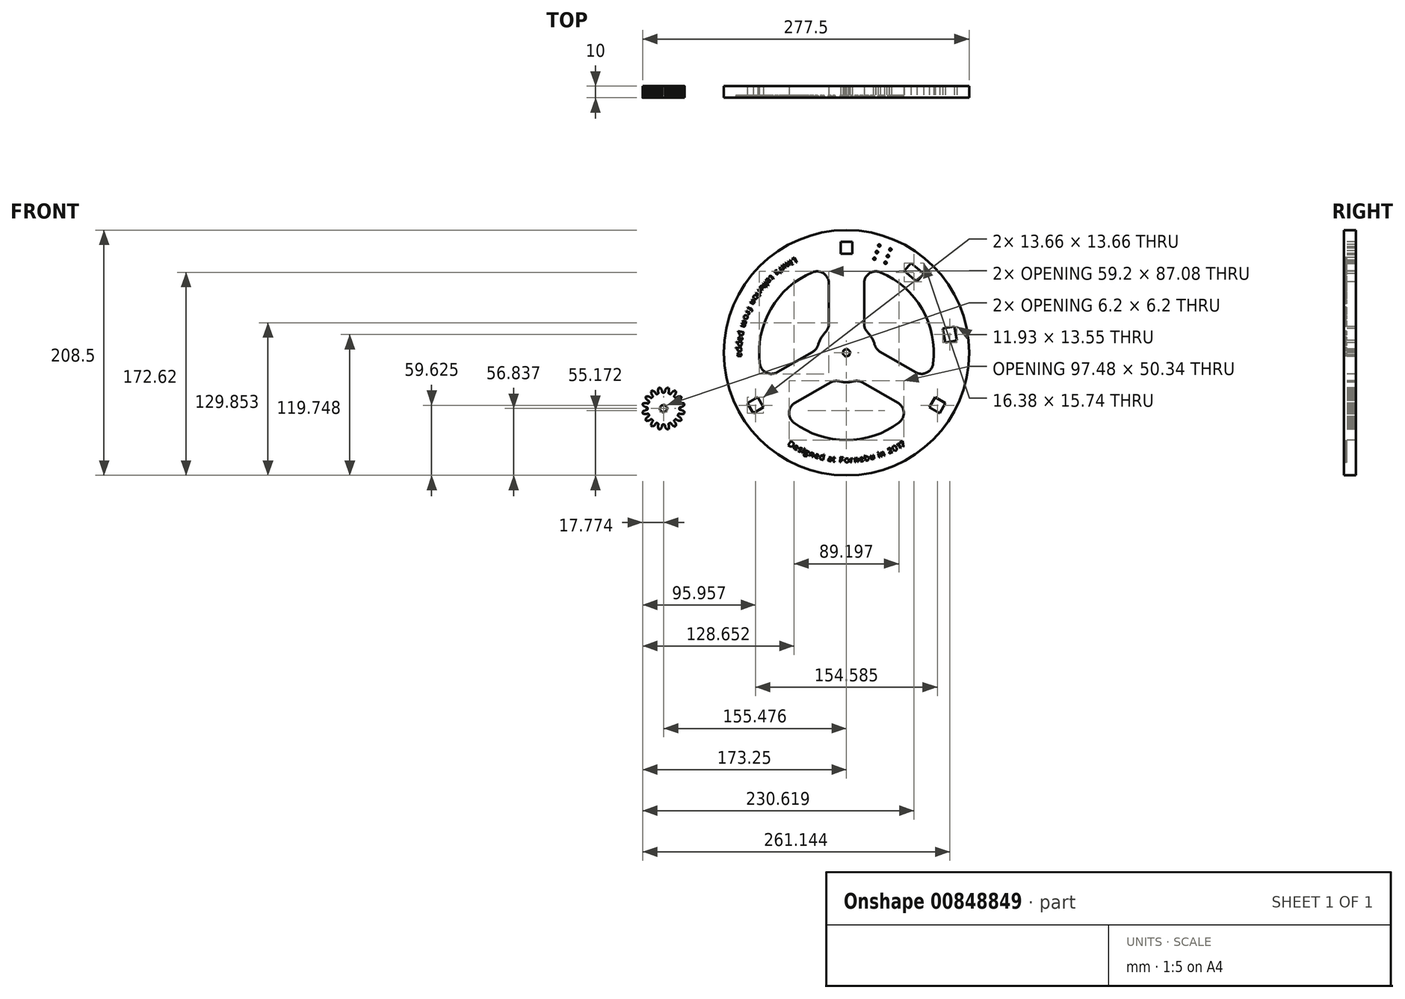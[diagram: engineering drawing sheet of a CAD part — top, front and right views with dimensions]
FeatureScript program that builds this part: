
annotation { "Feature Type Name" : "Feature", "Feature Type Description" : "" }
export const myFeature = defineFeature(function(context is Context, id is Id, definition is map)
    precondition{}
    {
        {
            var Q0;
            Q0=qCreatedBy(makeId("Front.planeOp"),FACE);
            var sketch = newSketch(context, id + "F0", { "sketchPlane" : qUnion([Q0])});
            skArc(sketch, "E0", {"start": v(15, 24.5) * mm, "mid": v(15.74, 20.72) * mm, "end": v(17.86, 17.5) * mm});
            skArc(sketch, "E1", {"start": v(24.08, 6.72) * mm, "mid": v(25.81, 3.28) * mm, "end": v(28.71, 0.74) * mm});
            skArc(sketch, "E2", {"start": v(28.9, 68.4) * mm, "mid": v(19.47, 67.52) * mm, "end": v(15, 59.19) * mm});
            skArc(sketch, "E3", {"start": v(58.76, -16.6) * mm, "mid": v(68.21, -16.9) * mm, "end": v(73.68, -9.18) * mm});
            skArc(sketch, "E4", {"start": v(-43.76, -42.58) * mm, "mid": v(-48.74, -50.62) * mm, "end": v(-44.79, -59.22) * mm});
            skArc(sketch, "E5", {"start": v(44.79, -59.22) * mm, "mid": v(48.74, -50.62) * mm, "end": v(43.76, -42.58) * mm});
            skArc(sketch, "E6", {"start": v(-6.22, -24.21) * mm, "mid": v(-10.07, -24) * mm, "end": v(-13.71, -25.24) * mm});
            skArc(sketch, "E7", {"start": v(-15, 59.19) * mm, "mid": v(-19.47, 67.52) * mm, "end": v(-28.9, 68.4) * mm});
            skArc(sketch, "E8", {"start": v(-17.86, 17.5) * mm, "mid": v(-15.74, 20.72) * mm, "end": v(-15, 24.5) * mm});
            skArc(sketch, "E9", {"start": v(-28.71, 0.74) * mm, "mid": v(-25.81, 3.28) * mm, "end": v(-24.08, 6.72) * mm});
            skArc(sketch, "E10", {"start": v(-73.68, -9.18) * mm, "mid": v(-68.21, -16.9) * mm, "end": v(-58.76, -16.6) * mm});
            skArc(sketch, "E11", {"start": v(-44.79, -59.22) * mm, "mid": v(0, -74.25) * mm, "end": v(44.79, -59.22) * mm});
            skArc(sketch, "E12", {"start": v(73.68, -9.18) * mm, "mid": v(64.3, 37.12) * mm, "end": v(28.9, 68.4) * mm});
            skArc(sketch, "E13", {"start": v(-3.1, 0) * mm, "mid": v(-3, -0.8) * mm, "end": v(-2.68, -1.55) * mm});
            skArc(sketch, "E14", {"start": v(-1.55, -2.68) * mm, "mid": v(-0.8, -3) * mm, "end": v(0, -3.1) * mm});
            skArc(sketch, "E15", {"start": v(1.55, -2.68) * mm, "mid": v(2.2, -2.2) * mm, "end": v(2.68, -1.55) * mm});
            skArc(sketch, "E16", {"start": v(3.1, 0) * mm, "mid": v(3, 0.8) * mm, "end": v(2.68, 1.55) * mm});
            skArc(sketch, "E17", {"start": v(2.51, 1.45) * mm, "mid": v(2.05, 2.05) * mm, "end": v(1.45, 2.51) * mm});
            skArc(sketch, "E18", {"start": v(0, -2.9) * mm, "mid": v(0.75, -2.8) * mm, "end": v(1.45, -2.51) * mm});
            skArc(sketch, "E19", {"start": v(1.55, 2.68) * mm, "mid": v(0.8, 3) * mm, "end": v(0, 3.1) * mm});
            skArc(sketch, "E20", {"start": v(-2.51, 1.45) * mm, "mid": v(-2.8, 0.75) * mm, "end": v(-2.9, 0) * mm});
            skArc(sketch, "E21", {"start": v(-2.51, -1.45) * mm, "mid": v(-2.05, -2.05) * mm, "end": v(-1.45, -2.51) * mm});
            skArc(sketch, "E22", {"start": v(2.51, -1.45) * mm, "mid": v(2.8, -0.75) * mm, "end": v(2.9, 0) * mm});
            skLineSegment(sketch, "E23", {"start": v(1.45, 2.51) * mm, "end": v(1.55, 2.68) * mm});
            skLineSegment(sketch, "E24", {"start": v(2.51, 1.45) * mm, "end": v(2.68, 1.55) * mm});
            skLineSegment(sketch, "E25", {"start": v(2.9, 0) * mm, "end": v(3.1, 0) * mm});
            skLineSegment(sketch, "E26", {"start": v(1.45, -2.51) * mm, "end": v(1.55, -2.68) * mm});
            skLineSegment(sketch, "E27", {"start": v(13.71, -25.24) * mm, "end": v(43.76, -42.58) * mm});
            skLineSegment(sketch, "E28", {"start": v(-13.71, -25.24) * mm, "end": v(-43.76, -42.58) * mm});
            skLineSegment(sketch, "E29", {"start": v(-28.71, 0.74) * mm, "end": v(-58.76, -16.6) * mm});
            skCircle(sketch, "E30", {"center": v(27.88, 91.22) * mm, "radius": 1 * mm});
            skLineSegment(sketch, "E31", {"start": v(70.46, -46.46) * mm, "end": v(75.46, -37.8) * mm});
            skLineSegment(sketch, "E32", {"start": v(70.46, -46.46) * mm, "end": v(79.12, -51.46) * mm});
            skLineSegment(sketch, "E33", {"start": v(75.46, -37.8) * mm, "end": v(84.12, -42.8) * mm});
            skCircle(sketch, "E34", {"center": v(37.28, 87.8) * mm, "radius": 1 * mm});
            skLineSegment(sketch, "E35", {"start": v(79.12, -51.46) * mm, "end": v(84.12, -42.8) * mm});
            skLineSegment(sketch, "E36", {"start": v(-70.46, -46.46) * mm, "end": v(-79.12, -51.46) * mm});
            skLineSegment(sketch, "E37", {"start": v(2.51, -1.45) * mm, "end": v(2.68, -1.55) * mm});
            skCircle(sketch, "E38", {"center": v(35.22, 82.16) * mm, "radius": 1 * mm});
            skLineSegment(sketch, "E39", {"start": v(-75.46, -37.8) * mm, "end": v(-84.12, -42.8) * mm});
            skLineSegment(sketch, "E40", {"start": v(-84.12, -42.8) * mm, "end": v(-79.12, -51.46) * mm});
            skLineSegment(sketch, "E41", {"start": v(-5, 84.25) * mm, "end": v(-5, 94.25) * mm});
            skArc(sketch, "E42", {"start": v(13.71, -25.24) * mm, "mid": v(10.07, -24) * mm, "end": v(6.22, -24.21) * mm});
            skCircle(sketch, "E43", {"center": v(33.17, 76.52) * mm, "radius": 1 * mm});
            skArc(sketch, "E44", {"start": v(-1.55, 2.68) * mm, "mid": v(-2.2, 2.2) * mm, "end": v(-2.68, 1.55) * mm});
            skCircle(sketch, "E45", {"center": v(0, 0) * mm, "radius": 104.25 * mm});
            skLineSegment(sketch, "E46", {"start": v(28.71, 0.74) * mm, "end": v(58.76, -16.6) * mm});
            skArc(sketch, "E47", {"start": v(-17.86, 17.5) * mm, "mid": v(-21.65, 12.5) * mm, "end": v(-24.08, 6.72) * mm});
            skArc(sketch, "E48", {"start": v(-28.9, 68.4) * mm, "mid": v(-64.3, 37.12) * mm, "end": v(-73.68, -9.18) * mm});
            skArc(sketch, "E49", {"start": v(0, 2.9) * mm, "mid": v(-0.75, 2.8) * mm, "end": v(-1.45, 2.51) * mm});
            skLineSegment(sketch, "E50", {"start": v(-75.46, -37.8) * mm, "end": v(-70.46, -46.46) * mm});
            skCircle(sketch, "E51", {"center": v(23.77, 79.94) * mm, "radius": 1 * mm});
            skLineSegment(sketch, "E52", {"start": v(15, 24.5) * mm, "end": v(15, 59.19) * mm});
            skLineSegment(sketch, "E53", {"start": v(-15, 24.5) * mm, "end": v(-15, 59.19) * mm});
            skLineSegment(sketch, "E54", {"start": v(5, 84.25) * mm, "end": v(-5, 84.25) * mm});
            skCircle(sketch, "E55", {"center": v(25.83, 85.58) * mm, "radius": 1 * mm});
            skLineSegment(sketch, "E56", {"start": v(5, 94.25) * mm, "end": v(-5, 94.25) * mm});
            skLineSegment(sketch, "E57", {"start": v(5, 84.25) * mm, "end": v(5, 94.25) * mm});
            skLineSegment(sketch, "E58", {"start": v(59.9, 60.5) * mm, "end": v(49.18, 69.5) * mm});
            skLineSegment(sketch, "E59", {"start": v(49.18, 69.5) * mm, "end": v(54.83, 76.24) * mm});
            skLineSegment(sketch, "E60", {"start": v(54.83, 76.24) * mm, "end": v(65.56, 67.24) * mm});
            skLineSegment(sketch, "E61", {"start": v(65.56, 67.24) * mm, "end": v(59.9, 60.5) * mm});
            skLineSegment(sketch, "E62", {"start": v(81.93, 20.54) * mm, "end": v(84.01, 8.72) * mm});
            skLineSegment(sketch, "E63", {"start": v(84.01, 8.72) * mm, "end": v(93.86, 10.46) * mm});
            skLineSegment(sketch, "E64", {"start": v(93.86, 10.46) * mm, "end": v(91.78, 22.28) * mm});
            skLineSegment(sketch, "E65", {"start": v(91.78, 22.28) * mm, "end": v(81.93, 20.54) * mm});
            skArc(sketch, "E66", {"start": v(-6.22, -24.21) * mm, "mid": v(0, -25) * mm, "end": v(6.22, -24.21) * mm});
            skArc(sketch, "E67", {"start": v(24.08, 6.72) * mm, "mid": v(21.65, 12.5) * mm, "end": v(17.86, 17.5) * mm});
            skLineSegment(sketch, "E68", {"start": v(0, 2.9) * mm, "end": v(0, 3.1) * mm});
            skLineSegment(sketch, "E69", {"start": v(-1.45, 2.51) * mm, "end": v(-1.55, 2.68) * mm});
            skLineSegment(sketch, "E70", {"start": v(-2.51, 1.45) * mm, "end": v(-2.68, 1.55) * mm});
            skLineSegment(sketch, "E71", {"start": v(-2.9, 0) * mm, "end": v(-3.1, 0) * mm});
            skLineSegment(sketch, "E72", {"start": v(-2.51, -1.45) * mm, "end": v(-2.68, -1.55) * mm});
            skLineSegment(sketch, "E73", {"start": v(-1.45, -2.51) * mm, "end": v(-1.55, -2.68) * mm});
            skLineSegment(sketch, "E74", {"start": v(0, -2.9) * mm, "end": v(0, -3.1) * mm});
            skLineSegment(sketch, "E75", {"start": v(-165.23, -35.88) * mm, "end": v(-165.3, -35.76) * mm});
            skLineSegment(sketch, "E76", {"start": v(-165.08, -36.06) * mm, "end": v(-165.23, -35.88) * mm});
            skLineSegment(sketch, "E77", {"start": v(-164.7, -36.5) * mm, "end": v(-165.08, -36.06) * mm});
            skArc(sketch, "E78", {"start": v(-164.92, -32.09) * mm, "mid": v(-165.48, -32.45) * mm, "end": v(-166.02, -32.83) * mm});
            skLineSegment(sketch, "E79", {"start": v(-164.03, -32.56) * mm, "end": v(-164.92, -32.09) * mm});
            skLineSegment(sketch, "E80", {"start": v(-163.29, -33.08) * mm, "end": v(-164.03, -32.56) * mm});
            skLineSegment(sketch, "E81", {"start": v(-163.08, -33.24) * mm, "end": v(-163.29, -33.08) * mm});
            skLineSegment(sketch, "E82", {"start": v(-162.9, -33.41) * mm, "end": v(-163.08, -33.24) * mm});
            skLineSegment(sketch, "E83", {"start": v(-162.74, -33.57) * mm, "end": v(-162.9, -33.41) * mm});
            skLineSegment(sketch, "E84", {"start": v(-162.6, -33.73) * mm, "end": v(-162.74, -33.57) * mm});
            skLineSegment(sketch, "E85", {"start": v(-162.48, -33.87) * mm, "end": v(-162.6, -33.73) * mm});
            skLineSegment(sketch, "E86", {"start": v(-162.4, -34) * mm, "end": v(-162.48, -33.87) * mm});
            skLineSegment(sketch, "E87", {"start": v(-162.29, -34.2) * mm, "end": v(-162.4, -34) * mm});
            skLineSegment(sketch, "E88", {"start": v(-162.02, -34.7) * mm, "end": v(-162.29, -34.2) * mm});
            skArc(sketch, "E89", {"start": v(-162.02, -34.7) * mm, "mid": v(-161.57, -35.1) * mm, "end": v(-160.97, -35.08) * mm});
            skArc(sketch, "E90", {"start": v(-160.31, -34.8) * mm, "mid": v(-160.64, -34.94) * mm, "end": v(-160.97, -35.08) * mm});
            skArc(sketch, "E91", {"start": v(-160.31, -34.8) * mm, "mid": v(-159.87, -34.4) * mm, "end": v(-159.83, -33.8) * mm});
            skLineSegment(sketch, "E92", {"start": v(-159.93, -30.86) * mm, "end": v(-159.64, -29.9) * mm});
            skLineSegment(sketch, "E93", {"start": v(-160.1, -31.75) * mm, "end": v(-159.93, -30.86) * mm});
            skLineSegment(sketch, "E94", {"start": v(-160.11, -32.01) * mm, "end": v(-160.1, -31.75) * mm});
            skLineSegment(sketch, "E95", {"start": v(-160.13, -32.26) * mm, "end": v(-160.11, -32.01) * mm});
            skLineSegment(sketch, "E96", {"start": v(-160.13, -32.5) * mm, "end": v(-160.13, -32.26) * mm});
            skLineSegment(sketch, "E97", {"start": v(-160.12, -32.7) * mm, "end": v(-160.13, -32.5) * mm});
            skLineSegment(sketch, "E98", {"start": v(-160.1, -32.88) * mm, "end": v(-160.12, -32.7) * mm});
            skLineSegment(sketch, "E99", {"start": v(-160.07, -33.03) * mm, "end": v(-160.1, -32.88) * mm});
            skLineSegment(sketch, "E100", {"start": v(-160, -33.25) * mm, "end": v(-160.07, -33.03) * mm});
            skLineSegment(sketch, "E101", {"start": v(-159.83, -33.8) * mm, "end": v(-160, -33.25) * mm});
            skArc(sketch, "E102", {"start": v(-158.33, -29.64) * mm, "mid": v(-158.99, -29.76) * mm, "end": v(-159.64, -29.9) * mm});
            skLineSegment(sketch, "E103", {"start": v(-157.7, -30.42) * mm, "end": v(-158.33, -29.64) * mm});
            skLineSegment(sketch, "E104", {"start": v(-157.2, -31.18) * mm, "end": v(-157.7, -30.42) * mm});
            skLineSegment(sketch, "E105", {"start": v(-157.08, -31.41) * mm, "end": v(-157.2, -31.18) * mm});
            skLineSegment(sketch, "E106", {"start": v(-156.98, -31.63) * mm, "end": v(-157.08, -31.41) * mm});
            skLineSegment(sketch, "E107", {"start": v(-156.89, -31.85) * mm, "end": v(-156.98, -31.63) * mm});
            skLineSegment(sketch, "E108", {"start": v(-156.82, -32.04) * mm, "end": v(-156.89, -31.85) * mm});
            skLineSegment(sketch, "E109", {"start": v(-156.77, -32.22) * mm, "end": v(-156.82, -32.04) * mm});
            skLineSegment(sketch, "E110", {"start": v(-156.74, -32.36) * mm, "end": v(-156.77, -32.22) * mm});
            skLineSegment(sketch, "E111", {"start": v(-156.71, -32.6) * mm, "end": v(-156.74, -32.36) * mm});
            skLineSegment(sketch, "E112", {"start": v(-156.66, -33.17) * mm, "end": v(-156.71, -32.6) * mm});
            skArc(sketch, "E113", {"start": v(-156.66, -33.17) * mm, "mid": v(-156.4, -33.7) * mm, "end": v(-155.83, -33.92) * mm});
            skArc(sketch, "E114", {"start": v(-155.12, -33.92) * mm, "mid": v(-155.48, -33.91) * mm, "end": v(-155.83, -33.92) * mm});
            skArc(sketch, "E115", {"start": v(-155.12, -33.92) * mm, "mid": v(-154.56, -33.7) * mm, "end": v(-154.29, -33.17) * mm});
            skLineSegment(sketch, "E116", {"start": v(-153.26, -30.42) * mm, "end": v(-152.62, -29.64) * mm});
            skLineSegment(sketch, "E117", {"start": v(-153.75, -31.18) * mm, "end": v(-153.26, -30.42) * mm});
            skLineSegment(sketch, "E118", {"start": v(-153.87, -31.41) * mm, "end": v(-153.75, -31.18) * mm});
            skLineSegment(sketch, "E119", {"start": v(-153.97, -31.63) * mm, "end": v(-153.87, -31.41) * mm});
            skLineSegment(sketch, "E120", {"start": v(-154.06, -31.85) * mm, "end": v(-153.97, -31.63) * mm});
            skLineSegment(sketch, "E121", {"start": v(-154.13, -32.04) * mm, "end": v(-154.06, -31.85) * mm});
            skLineSegment(sketch, "E122", {"start": v(-154.18, -32.22) * mm, "end": v(-154.13, -32.04) * mm});
            skLineSegment(sketch, "E123", {"start": v(-154.22, -32.36) * mm, "end": v(-154.18, -32.22) * mm});
            skLineSegment(sketch, "E124", {"start": v(-154.24, -32.6) * mm, "end": v(-154.22, -32.36) * mm});
            skLineSegment(sketch, "E125", {"start": v(-154.29, -33.17) * mm, "end": v(-154.24, -32.6) * mm});
            skArc(sketch, "E126", {"start": v(-151.31, -29.9) * mm, "mid": v(-151.96, -29.76) * mm, "end": v(-152.62, -29.64) * mm});
            skLineSegment(sketch, "E127", {"start": v(-151.02, -30.86) * mm, "end": v(-151.31, -29.9) * mm});
            skLineSegment(sketch, "E128", {"start": v(-150.86, -31.75) * mm, "end": v(-151.02, -30.86) * mm});
            skLineSegment(sketch, "E129", {"start": v(-150.84, -32.01) * mm, "end": v(-150.86, -31.75) * mm});
            skLineSegment(sketch, "E130", {"start": v(-150.82, -32.26) * mm, "end": v(-150.84, -32.01) * mm});
            skLineSegment(sketch, "E131", {"start": v(-150.82, -32.5) * mm, "end": v(-150.82, -32.26) * mm});
            skLineSegment(sketch, "E132", {"start": v(-150.84, -32.7) * mm, "end": v(-150.82, -32.5) * mm});
            skLineSegment(sketch, "E133", {"start": v(-150.86, -32.88) * mm, "end": v(-150.84, -32.7) * mm});
            skLineSegment(sketch, "E134", {"start": v(-150.88, -33.03) * mm, "end": v(-150.86, -32.88) * mm});
            skLineSegment(sketch, "E135", {"start": v(-138.93, -51.87) * mm, "end": v(-137.96, -51.57) * mm});
            skArc(sketch, "E136", {"start": v(-137.96, -51.57) * mm, "mid": v(-137.82, -50.92) * mm, "end": v(-137.7, -50.27) * mm});
            skLineSegment(sketch, "E137", {"start": v(-141.23, -48.6) * mm, "end": v(-140.65, -48.65) * mm});
            skLineSegment(sketch, "E138", {"start": v(-140.65, -48.65) * mm, "end": v(-140.43, -48.67) * mm});
            skLineSegment(sketch, "E139", {"start": v(-140.43, -48.67) * mm, "end": v(-140.28, -48.7) * mm});
            skLineSegment(sketch, "E140", {"start": v(-140.28, -48.7) * mm, "end": v(-140.1, -48.76) * mm});
            skLineSegment(sketch, "E141", {"start": v(-140.1, -48.76) * mm, "end": v(-139.9, -48.83) * mm});
            skLineSegment(sketch, "E142", {"start": v(-139.9, -48.83) * mm, "end": v(-139.7, -48.91) * mm});
            skLineSegment(sketch, "E143", {"start": v(-139.7, -48.91) * mm, "end": v(-139.47, -49.02) * mm});
            skLineSegment(sketch, "E144", {"start": v(-139.47, -49.02) * mm, "end": v(-139.24, -49.14) * mm});
            skLineSegment(sketch, "E145", {"start": v(-139.24, -49.14) * mm, "end": v(-138.48, -49.63) * mm});
            skLineSegment(sketch, "E146", {"start": v(-138.48, -49.63) * mm, "end": v(-137.7, -50.27) * mm});
            skArc(sketch, "E147", {"start": v(-141.98, -47.77) * mm, "mid": v(-141.77, -48.33) * mm, "end": v(-141.23, -48.6) * mm});
            skArc(sketch, "E148", {"start": v(-141.98, -47.77) * mm, "mid": v(-141.98, -47.41) * mm, "end": v(-141.98, -47.06) * mm});
            skArc(sketch, "E149", {"start": v(-141.23, -46.23) * mm, "mid": v(-141.77, -46.5) * mm, "end": v(-141.98, -47.06) * mm});
            skLineSegment(sketch, "E150", {"start": v(-141.23, -46.23) * mm, "end": v(-140.65, -46.18) * mm});
            skLineSegment(sketch, "E151", {"start": v(-140.65, -46.18) * mm, "end": v(-140.43, -46.15) * mm});
            skLineSegment(sketch, "E152", {"start": v(-140.43, -46.15) * mm, "end": v(-140.28, -46.12) * mm});
            skLineSegment(sketch, "E153", {"start": v(-140.28, -46.12) * mm, "end": v(-140.1, -46.07) * mm});
            skLineSegment(sketch, "E154", {"start": v(-140.1, -46.07) * mm, "end": v(-139.9, -46) * mm});
            skLineSegment(sketch, "E155", {"start": v(-139.9, -46) * mm, "end": v(-139.7, -45.91) * mm});
            skLineSegment(sketch, "E156", {"start": v(-139.7, -45.91) * mm, "end": v(-139.47, -45.8) * mm});
            skLineSegment(sketch, "E157", {"start": v(-139.47, -45.8) * mm, "end": v(-139.24, -45.68) * mm});
            skLineSegment(sketch, "E158", {"start": v(-139.24, -45.68) * mm, "end": v(-138.48, -45.2) * mm});
            skLineSegment(sketch, "E159", {"start": v(-138.48, -45.2) * mm, "end": v(-137.7, -44.56) * mm});
            skArc(sketch, "E160", {"start": v(-137.7, -44.56) * mm, "mid": v(-137.82, -43.9) * mm, "end": v(-137.96, -43.25) * mm});
            skLineSegment(sketch, "E161", {"start": v(-141.86, -43.06) * mm, "end": v(-141.3, -42.88) * mm});
            skLineSegment(sketch, "E162", {"start": v(-141.3, -42.88) * mm, "end": v(-141.1, -42.82) * mm});
            skLineSegment(sketch, "E163", {"start": v(-141.1, -42.82) * mm, "end": v(-140.94, -42.8) * mm});
            skLineSegment(sketch, "E164", {"start": v(-140.94, -42.8) * mm, "end": v(-140.76, -42.77) * mm});
            skLineSegment(sketch, "E165", {"start": v(-140.76, -42.77) * mm, "end": v(-140.55, -42.76) * mm});
            skLineSegment(sketch, "E166", {"start": v(-140.55, -42.76) * mm, "end": v(-140.32, -42.76) * mm});
            skLineSegment(sketch, "E167", {"start": v(-140.32, -42.76) * mm, "end": v(-140.08, -42.77) * mm});
            skLineSegment(sketch, "E168", {"start": v(-140.08, -42.77) * mm, "end": v(-139.82, -42.8) * mm});
            skLineSegment(sketch, "E169", {"start": v(-139.82, -42.8) * mm, "end": v(-138.93, -42.96) * mm});
            skLineSegment(sketch, "E170", {"start": v(-138.93, -42.96) * mm, "end": v(-137.96, -43.25) * mm});
            skArc(sketch, "E171", {"start": v(-142.87, -42.58) * mm, "mid": v(-142.46, -43.02) * mm, "end": v(-141.86, -43.06) * mm});
            skArc(sketch, "E172", {"start": v(-142.87, -42.58) * mm, "mid": v(-143, -42.25) * mm, "end": v(-143.14, -41.92) * mm});
            skArc(sketch, "E173", {"start": v(-142.77, -40.87) * mm, "mid": v(-143.17, -41.32) * mm, "end": v(-143.14, -41.92) * mm});
            skLineSegment(sketch, "E174", {"start": v(-142.77, -40.87) * mm, "end": v(-142.25, -40.6) * mm});
            skLineSegment(sketch, "E175", {"start": v(-142.25, -40.6) * mm, "end": v(-142.05, -40.5) * mm});
            skLineSegment(sketch, "E176", {"start": v(-142.05, -40.5) * mm, "end": v(-141.93, -40.4) * mm});
            skLineSegment(sketch, "E177", {"start": v(-141.93, -40.4) * mm, "end": v(-141.8, -40.3) * mm});
            skLineSegment(sketch, "E178", {"start": v(-141.8, -40.3) * mm, "end": v(-141.64, -40.15) * mm});
            skLineSegment(sketch, "E179", {"start": v(-141.64, -40.15) * mm, "end": v(-141.47, -39.99) * mm});
            skLineSegment(sketch, "E180", {"start": v(-141.47, -39.99) * mm, "end": v(-141.3, -39.8) * mm});
            skLineSegment(sketch, "E181", {"start": v(-141.3, -39.8) * mm, "end": v(-141.14, -39.6) * mm});
            skLineSegment(sketch, "E182", {"start": v(-141.14, -39.6) * mm, "end": v(-140.62, -38.86) * mm});
            skLineSegment(sketch, "E183", {"start": v(-140.62, -38.86) * mm, "end": v(-140.15, -37.97) * mm});
            skArc(sketch, "E184", {"start": v(-140.15, -37.97) * mm, "mid": v(-140.5, -37.41) * mm, "end": v(-140.89, -36.87) * mm});
            skLineSegment(sketch, "E185", {"start": v(-144.57, -38.18) * mm, "end": v(-144.12, -37.8) * mm});
            skLineSegment(sketch, "E186", {"start": v(-144.12, -37.8) * mm, "end": v(-143.94, -37.66) * mm});
            skLineSegment(sketch, "E187", {"start": v(-143.94, -37.66) * mm, "end": v(-143.82, -37.58) * mm});
            skLineSegment(sketch, "E188", {"start": v(-143.82, -37.58) * mm, "end": v(-143.66, -37.5) * mm});
            skLineSegment(sketch, "E189", {"start": v(-143.66, -37.5) * mm, "end": v(-143.47, -37.4) * mm});
            skLineSegment(sketch, "E190", {"start": v(-143.47, -37.4) * mm, "end": v(-143.26, -37.32) * mm});
            skLineSegment(sketch, "E191", {"start": v(-143.26, -37.32) * mm, "end": v(-143.02, -37.23) * mm});
            skLineSegment(sketch, "E192", {"start": v(-143.02, -37.23) * mm, "end": v(-142.77, -37.16) * mm});
            skLineSegment(sketch, "E193", {"start": v(-142.77, -37.16) * mm, "end": v(-141.9, -36.96) * mm});
            skLineSegment(sketch, "E194", {"start": v(-141.9, -36.96) * mm, "end": v(-140.89, -36.87) * mm});
            skArc(sketch, "E195", {"start": v(-145.68, -38.12) * mm, "mid": v(-145.14, -38.37) * mm, "end": v(-144.57, -38.18) * mm});
            skArc(sketch, "E196", {"start": v(-145.68, -38.12) * mm, "mid": v(-145.93, -37.87) * mm, "end": v(-146.18, -37.62) * mm});
            skArc(sketch, "E197", {"start": v(-146.24, -36.5) * mm, "mid": v(-146.44, -37.07) * mm, "end": v(-146.18, -37.62) * mm});
            skLineSegment(sketch, "E198", {"start": v(-146.24, -36.5) * mm, "end": v(-145.87, -36.06) * mm});
            skLineSegment(sketch, "E199", {"start": v(-145.87, -36.06) * mm, "end": v(-145.73, -35.88) * mm});
            skLineSegment(sketch, "E200", {"start": v(-145.73, -35.88) * mm, "end": v(-145.65, -35.76) * mm});
            skLineSegment(sketch, "E201", {"start": v(-145.65, -35.76) * mm, "end": v(-145.56, -35.6) * mm});
            skLineSegment(sketch, "E202", {"start": v(-145.56, -35.6) * mm, "end": v(-145.47, -35.4) * mm});
            skLineSegment(sketch, "E203", {"start": v(-145.47, -35.4) * mm, "end": v(-145.38, -35.2) * mm});
            skLineSegment(sketch, "E204", {"start": v(-145.38, -35.2) * mm, "end": v(-145.3, -34.96) * mm});
            skLineSegment(sketch, "E205", {"start": v(-145.3, -34.96) * mm, "end": v(-145.22, -34.71) * mm});
            skLineSegment(sketch, "E206", {"start": v(-145.22, -34.71) * mm, "end": v(-145.03, -33.83) * mm});
            skLineSegment(sketch, "E207", {"start": v(-145.03, -33.83) * mm, "end": v(-144.93, -32.83) * mm});
            skArc(sketch, "E208", {"start": v(-144.93, -32.83) * mm, "mid": v(-145.48, -32.45) * mm, "end": v(-146.04, -32.09) * mm});
            skLineSegment(sketch, "E209", {"start": v(-148.93, -34.7) * mm, "end": v(-148.66, -34.2) * mm});
            skLineSegment(sketch, "E210", {"start": v(-148.66, -34.2) * mm, "end": v(-148.55, -34) * mm});
            skLineSegment(sketch, "E211", {"start": v(-148.55, -34) * mm, "end": v(-148.47, -33.87) * mm});
            skLineSegment(sketch, "E212", {"start": v(-148.47, -33.87) * mm, "end": v(-148.35, -33.73) * mm});
            skLineSegment(sketch, "E213", {"start": v(-148.35, -33.73) * mm, "end": v(-148.21, -33.57) * mm});
            skLineSegment(sketch, "E214", {"start": v(-148.21, -33.57) * mm, "end": v(-148.05, -33.41) * mm});
            skLineSegment(sketch, "E215", {"start": v(-148.05, -33.41) * mm, "end": v(-147.87, -33.24) * mm});
            skLineSegment(sketch, "E216", {"start": v(-147.87, -33.24) * mm, "end": v(-147.67, -33.08) * mm});
            skLineSegment(sketch, "E217", {"start": v(-147.67, -33.08) * mm, "end": v(-146.92, -32.56) * mm});
            skLineSegment(sketch, "E218", {"start": v(-146.92, -32.56) * mm, "end": v(-146.04, -32.09) * mm});
            skArc(sketch, "E219", {"start": v(-149.98, -35.08) * mm, "mid": v(-149.38, -35.1) * mm, "end": v(-148.93, -34.7) * mm});
            skArc(sketch, "E220", {"start": v(-149.98, -35.08) * mm, "mid": v(-150.3, -34.94) * mm, "end": v(-150.64, -34.8) * mm});
            skArc(sketch, "E221", {"start": v(-151.12, -33.8) * mm, "mid": v(-151.08, -34.4) * mm, "end": v(-150.64, -34.8) * mm});
            skLineSegment(sketch, "E222", {"start": v(-151.12, -33.8) * mm, "end": v(-150.94, -33.25) * mm});
            skLineSegment(sketch, "E223", {"start": v(-150.94, -33.25) * mm, "end": v(-150.88, -33.03) * mm});
            skLineSegment(sketch, "E224", {"start": v(-165.57, -35.2) * mm, "end": v(-165.65, -34.96) * mm});
            skLineSegment(sketch, "E225", {"start": v(-165.65, -34.96) * mm, "end": v(-165.73, -34.71) * mm});
            skLineSegment(sketch, "E226", {"start": v(-165.73, -34.71) * mm, "end": v(-165.92, -33.83) * mm});
            skLineSegment(sketch, "E227", {"start": v(-165.92, -33.83) * mm, "end": v(-166.02, -32.83) * mm});
            skArc(sketch, "E228", {"start": v(-164.77, -37.62) * mm, "mid": v(-164.52, -37.07) * mm, "end": v(-164.7, -36.5) * mm});
            skArc(sketch, "E229", {"start": v(-164.77, -37.62) * mm, "mid": v(-165.02, -37.87) * mm, "end": v(-165.27, -38.12) * mm});
            skArc(sketch, "E230", {"start": v(-166.39, -38.18) * mm, "mid": v(-165.82, -38.37) * mm, "end": v(-165.27, -38.12) * mm});
            skLineSegment(sketch, "E231", {"start": v(-166.39, -38.18) * mm, "end": v(-166.83, -37.8) * mm});
            skLineSegment(sketch, "E232", {"start": v(-166.83, -37.8) * mm, "end": v(-167, -37.66) * mm});
            skLineSegment(sketch, "E233", {"start": v(-167, -37.66) * mm, "end": v(-167.13, -37.58) * mm});
            skLineSegment(sketch, "E234", {"start": v(-167.13, -37.58) * mm, "end": v(-167.3, -37.5) * mm});
            skLineSegment(sketch, "E235", {"start": v(-167.3, -37.5) * mm, "end": v(-167.48, -37.4) * mm});
            skLineSegment(sketch, "E236", {"start": v(-167.48, -37.4) * mm, "end": v(-167.7, -37.32) * mm});
            skLineSegment(sketch, "E237", {"start": v(-167.7, -37.32) * mm, "end": v(-167.93, -37.23) * mm});
            skLineSegment(sketch, "E238", {"start": v(-167.93, -37.23) * mm, "end": v(-168.18, -37.16) * mm});
            skLineSegment(sketch, "E239", {"start": v(-168.18, -37.16) * mm, "end": v(-169.06, -36.96) * mm});
            skLineSegment(sketch, "E240", {"start": v(-169.06, -36.96) * mm, "end": v(-170.06, -36.87) * mm});
            skArc(sketch, "E241", {"start": v(-170.06, -36.87) * mm, "mid": v(-170.44, -37.41) * mm, "end": v(-170.8, -37.97) * mm});
            skLineSegment(sketch, "E242", {"start": v(-168.18, -40.87) * mm, "end": v(-168.7, -40.6) * mm});
            skLineSegment(sketch, "E243", {"start": v(-168.7, -40.6) * mm, "end": v(-168.9, -40.5) * mm});
            skLineSegment(sketch, "E244", {"start": v(-168.9, -40.5) * mm, "end": v(-169.02, -40.4) * mm});
            skLineSegment(sketch, "E245", {"start": v(-169.02, -40.4) * mm, "end": v(-169.16, -40.3) * mm});
            skLineSegment(sketch, "E246", {"start": v(-169.16, -40.3) * mm, "end": v(-169.32, -40.15) * mm});
            skLineSegment(sketch, "E247", {"start": v(-169.32, -40.15) * mm, "end": v(-169.48, -39.99) * mm});
            skLineSegment(sketch, "E248", {"start": v(-169.48, -39.99) * mm, "end": v(-169.64, -39.8) * mm});
            skLineSegment(sketch, "E249", {"start": v(-169.64, -39.8) * mm, "end": v(-169.81, -39.6) * mm});
            skLineSegment(sketch, "E250", {"start": v(-169.81, -39.6) * mm, "end": v(-170.33, -38.86) * mm});
            skLineSegment(sketch, "E251", {"start": v(-170.33, -38.86) * mm, "end": v(-170.8, -37.97) * mm});
            skArc(sketch, "E252", {"start": v(-167.8, -41.92) * mm, "mid": v(-167.78, -41.32) * mm, "end": v(-168.18, -40.87) * mm});
            skArc(sketch, "E253", {"start": v(-167.8, -41.92) * mm, "mid": v(-167.95, -42.25) * mm, "end": v(-168.08, -42.58) * mm});
            skArc(sketch, "E254", {"start": v(-169.09, -43.06) * mm, "mid": v(-168.49, -43.02) * mm, "end": v(-168.08, -42.58) * mm});
            skLineSegment(sketch, "E255", {"start": v(-169.09, -43.06) * mm, "end": v(-169.64, -42.88) * mm});
            skLineSegment(sketch, "E256", {"start": v(-169.64, -42.88) * mm, "end": v(-169.86, -42.82) * mm});
            skLineSegment(sketch, "E257", {"start": v(-169.86, -42.82) * mm, "end": v(-170, -42.8) * mm});
            skLineSegment(sketch, "E258", {"start": v(-170, -42.8) * mm, "end": v(-170.19, -42.77) * mm});
            skLineSegment(sketch, "E259", {"start": v(-170.19, -42.77) * mm, "end": v(-170.4, -42.76) * mm});
            skLineSegment(sketch, "E260", {"start": v(-170.4, -42.76) * mm, "end": v(-170.63, -42.76) * mm});
            skLineSegment(sketch, "E261", {"start": v(-170.63, -42.76) * mm, "end": v(-170.87, -42.77) * mm});
            skLineSegment(sketch, "E262", {"start": v(-170.87, -42.77) * mm, "end": v(-171.13, -42.8) * mm});
            skArc(sketch, "E263", {"start": v(-170.8, -56.85) * mm, "mid": v(-170.44, -57.41) * mm, "end": v(-170.06, -57.96) * mm});
            skLineSegment(sketch, "E264", {"start": v(-154.24, -62.24) * mm, "end": v(-154.22, -62.46) * mm});
            skLineSegment(sketch, "E265", {"start": v(-166.39, -56.65) * mm, "end": v(-166.83, -57.02) * mm});
            skLineSegment(sketch, "E266", {"start": v(-154.22, -62.46) * mm, "end": v(-154.18, -62.6) * mm});
            skLineSegment(sketch, "E267", {"start": v(-166.83, -57.02) * mm, "end": v(-167, -57.16) * mm});
            skLineSegment(sketch, "E268", {"start": v(-154.18, -62.6) * mm, "end": v(-154.13, -62.78) * mm});
            skLineSegment(sketch, "E269", {"start": v(-167, -57.16) * mm, "end": v(-167.13, -57.24) * mm});
            skLineSegment(sketch, "E270", {"start": v(-154.13, -62.78) * mm, "end": v(-154.06, -62.98) * mm});
            skLineSegment(sketch, "E271", {"start": v(-167.13, -57.24) * mm, "end": v(-167.3, -57.33) * mm});
            skLineSegment(sketch, "E272", {"start": v(-154.06, -62.98) * mm, "end": v(-153.97, -63.2) * mm});
            skLineSegment(sketch, "E273", {"start": v(-167.3, -57.33) * mm, "end": v(-167.48, -57.42) * mm});
            skLineSegment(sketch, "E274", {"start": v(-153.97, -63.2) * mm, "end": v(-153.87, -63.41) * mm});
            skLineSegment(sketch, "E275", {"start": v(-167.48, -57.42) * mm, "end": v(-167.7, -57.5) * mm});
            skLineSegment(sketch, "E276", {"start": v(-153.87, -63.41) * mm, "end": v(-153.75, -63.65) * mm});
            skLineSegment(sketch, "E277", {"start": v(-167.7, -57.5) * mm, "end": v(-167.93, -57.6) * mm});
            skLineSegment(sketch, "E278", {"start": v(-153.75, -63.65) * mm, "end": v(-153.26, -64.4) * mm});
            skLineSegment(sketch, "E279", {"start": v(-167.93, -57.6) * mm, "end": v(-168.18, -57.67) * mm});
            skLineSegment(sketch, "E280", {"start": v(-153.26, -64.4) * mm, "end": v(-152.62, -65.19) * mm});
            skLineSegment(sketch, "E281", {"start": v(-168.18, -57.67) * mm, "end": v(-169.06, -57.86) * mm});
            skArc(sketch, "E282", {"start": v(-152.62, -65.19) * mm, "mid": v(-151.96, -65.07) * mm, "end": v(-151.31, -64.93) * mm});
            skLineSegment(sketch, "E283", {"start": v(-169.06, -57.86) * mm, "end": v(-170.06, -57.96) * mm});
            skLineSegment(sketch, "E284", {"start": v(-151.12, -61.03) * mm, "end": v(-150.94, -61.58) * mm});
            skArc(sketch, "E285", {"start": v(-165.27, -56.7) * mm, "mid": v(-165.82, -56.45) * mm, "end": v(-166.39, -56.65) * mm});
            skLineSegment(sketch, "E286", {"start": v(-150.94, -61.58) * mm, "end": v(-150.88, -61.8) * mm});
            skArc(sketch, "E287", {"start": v(-165.27, -56.7) * mm, "mid": v(-165.02, -56.96) * mm, "end": v(-164.77, -57.2) * mm});
            skLineSegment(sketch, "E288", {"start": v(-150.88, -61.8) * mm, "end": v(-150.86, -61.94) * mm});
            skLineSegment(sketch, "E289", {"start": v(-150.86, -61.94) * mm, "end": v(-150.84, -62.13) * mm});
            skLineSegment(sketch, "E290", {"start": v(-150.84, -62.13) * mm, "end": v(-150.82, -62.34) * mm});
            skLineSegment(sketch, "E291", {"start": v(-150.82, -62.34) * mm, "end": v(-150.82, -62.57) * mm});
            skLineSegment(sketch, "E292", {"start": v(-150.82, -62.57) * mm, "end": v(-150.84, -62.81) * mm});
            skLineSegment(sketch, "E293", {"start": v(-150.84, -62.81) * mm, "end": v(-150.86, -63.07) * mm});
            skLineSegment(sketch, "E294", {"start": v(-150.86, -63.07) * mm, "end": v(-151.02, -63.96) * mm});
            skLineSegment(sketch, "E295", {"start": v(-151.02, -63.96) * mm, "end": v(-151.31, -64.93) * mm});
            skArc(sketch, "E296", {"start": v(-150.64, -60.02) * mm, "mid": v(-151.08, -60.43) * mm, "end": v(-151.12, -61.03) * mm});
            skArc(sketch, "E297", {"start": v(-150.64, -60.02) * mm, "mid": v(-150.3, -59.89) * mm, "end": v(-149.98, -59.75) * mm});
            skArc(sketch, "E298", {"start": v(-148.93, -60.12) * mm, "mid": v(-149.38, -59.72) * mm, "end": v(-149.98, -59.75) * mm});
            skArc(sketch, "E299", {"start": v(-157.99, -48.86) * mm, "mid": v(-157.53, -49.46) * mm, "end": v(-156.93, -49.92) * mm});
            skLineSegment(sketch, "E300", {"start": v(-148.93, -60.12) * mm, "end": v(-148.66, -60.63) * mm});
            skArc(sketch, "E301", {"start": v(-146.04, -62.74) * mm, "mid": v(-145.48, -62.38) * mm, "end": v(-144.93, -62) * mm});
            skLineSegment(sketch, "E302", {"start": v(-146.92, -62.26) * mm, "end": v(-146.04, -62.74) * mm});
            skLineSegment(sketch, "E303", {"start": v(-147.67, -61.75) * mm, "end": v(-146.92, -62.26) * mm});
            skLineSegment(sketch, "E304", {"start": v(-147.87, -61.58) * mm, "end": v(-147.67, -61.75) * mm});
            skLineSegment(sketch, "E305", {"start": v(-148.05, -61.42) * mm, "end": v(-147.87, -61.58) * mm});
            skLineSegment(sketch, "E306", {"start": v(-148.21, -61.25) * mm, "end": v(-148.05, -61.42) * mm});
            skLineSegment(sketch, "E307", {"start": v(-148.35, -61.1) * mm, "end": v(-148.21, -61.25) * mm});
            skLineSegment(sketch, "E308", {"start": v(-148.47, -60.96) * mm, "end": v(-148.35, -61.1) * mm});
            skLineSegment(sketch, "E309", {"start": v(-148.55, -60.83) * mm, "end": v(-148.47, -60.96) * mm});
            skLineSegment(sketch, "E310", {"start": v(-148.66, -60.63) * mm, "end": v(-148.55, -60.83) * mm});
            skLineSegment(sketch, "E311", {"start": v(-170.33, -55.96) * mm, "end": v(-170.8, -56.85) * mm});
            skLineSegment(sketch, "E312", {"start": v(-154.29, -61.66) * mm, "end": v(-154.24, -62.24) * mm});
            skLineSegment(sketch, "E313", {"start": v(-169.81, -55.22) * mm, "end": v(-170.33, -55.96) * mm});
            skArc(sketch, "E314", {"start": v(-154.29, -61.66) * mm, "mid": v(-154.56, -61.12) * mm, "end": v(-155.12, -60.9) * mm});
            skLineSegment(sketch, "E315", {"start": v(-169.64, -55.02) * mm, "end": v(-169.81, -55.22) * mm});
            skArc(sketch, "E316", {"start": v(-155.83, -60.9) * mm, "mid": v(-155.48, -60.91) * mm, "end": v(-155.12, -60.9) * mm});
            skLineSegment(sketch, "E317", {"start": v(-169.48, -54.84) * mm, "end": v(-169.64, -55.02) * mm});
            skArc(sketch, "E318", {"start": v(-155.83, -60.9) * mm, "mid": v(-156.4, -61.12) * mm, "end": v(-156.66, -61.66) * mm});
            skLineSegment(sketch, "E319", {"start": v(-169.32, -54.68) * mm, "end": v(-169.48, -54.84) * mm});
            skLineSegment(sketch, "E320", {"start": v(-169.16, -54.54) * mm, "end": v(-169.32, -54.68) * mm});
            skLineSegment(sketch, "E321", {"start": v(-169.02, -54.42) * mm, "end": v(-169.16, -54.54) * mm});
            skLineSegment(sketch, "E322", {"start": v(-168.9, -54.34) * mm, "end": v(-169.02, -54.42) * mm});
            skLineSegment(sketch, "E323", {"start": v(-168.7, -54.23) * mm, "end": v(-168.9, -54.34) * mm});
            skLineSegment(sketch, "E324", {"start": v(-168.18, -53.96) * mm, "end": v(-168.7, -54.23) * mm});
            skArc(sketch, "E325", {"start": v(-168.18, -53.96) * mm, "mid": v(-167.78, -53.5) * mm, "end": v(-167.8, -52.9) * mm});
            skArc(sketch, "E326", {"start": v(-168.08, -52.25) * mm, "mid": v(-167.95, -52.58) * mm, "end": v(-167.8, -52.9) * mm});
            skArc(sketch, "E327", {"start": v(-168.08, -52.25) * mm, "mid": v(-168.49, -51.8) * mm, "end": v(-169.09, -51.77) * mm});
            skLineSegment(sketch, "E328", {"start": v(-172.02, -51.87) * mm, "end": v(-172.99, -51.57) * mm});
            skLineSegment(sketch, "E329", {"start": v(-171.13, -52.03) * mm, "end": v(-172.02, -51.87) * mm});
            skLineSegment(sketch, "E330", {"start": v(-170.87, -52.05) * mm, "end": v(-171.13, -52.03) * mm});
            skLineSegment(sketch, "E331", {"start": v(-170.63, -52.06) * mm, "end": v(-170.87, -52.05) * mm});
            skLineSegment(sketch, "E332", {"start": v(-170.4, -52.06) * mm, "end": v(-170.63, -52.06) * mm});
            skLineSegment(sketch, "E333", {"start": v(-170.19, -52.05) * mm, "end": v(-170.4, -52.06) * mm});
            skLineSegment(sketch, "E334", {"start": v(-170, -52.03) * mm, "end": v(-170.19, -52.05) * mm});
            skLineSegment(sketch, "E335", {"start": v(-169.86, -52) * mm, "end": v(-170, -52.03) * mm});
            skLineSegment(sketch, "E336", {"start": v(-169.64, -51.94) * mm, "end": v(-169.86, -52) * mm});
            skLineSegment(sketch, "E337", {"start": v(-169.09, -51.77) * mm, "end": v(-169.64, -51.94) * mm});
            skArc(sketch, "E338", {"start": v(-173.25, -50.27) * mm, "mid": v(-173.13, -50.92) * mm, "end": v(-172.99, -51.57) * mm});
            skLineSegment(sketch, "E339", {"start": v(-172.47, -49.63) * mm, "end": v(-173.25, -50.27) * mm});
            skLineSegment(sketch, "E340", {"start": v(-171.7, -49.14) * mm, "end": v(-172.47, -49.63) * mm});
            skLineSegment(sketch, "E341", {"start": v(-157.7, -64.4) * mm, "end": v(-158.33, -65.19) * mm});
            skLineSegment(sketch, "E342", {"start": v(-139.82, -52.03) * mm, "end": v(-138.93, -51.87) * mm});
            skLineSegment(sketch, "E343", {"start": v(-157.2, -63.65) * mm, "end": v(-157.7, -64.4) * mm});
            skLineSegment(sketch, "E344", {"start": v(-140.08, -52.05) * mm, "end": v(-139.82, -52.03) * mm});
            skLineSegment(sketch, "E345", {"start": v(-157.08, -63.41) * mm, "end": v(-157.2, -63.65) * mm});
            skLineSegment(sketch, "E346", {"start": v(-140.32, -52.06) * mm, "end": v(-140.08, -52.05) * mm});
            skLineSegment(sketch, "E347", {"start": v(-156.98, -63.2) * mm, "end": v(-157.08, -63.41) * mm});
            skLineSegment(sketch, "E348", {"start": v(-140.55, -52.06) * mm, "end": v(-140.32, -52.06) * mm});
            skLineSegment(sketch, "E349", {"start": v(-143.02, -57.6) * mm, "end": v(-142.77, -57.67) * mm});
            skLineSegment(sketch, "E350", {"start": v(-163.29, -61.75) * mm, "end": v(-164.03, -62.26) * mm});
            skLineSegment(sketch, "E351", {"start": v(-170.84, -48.76) * mm, "end": v(-171.04, -48.83) * mm});
            skLineSegment(sketch, "E352", {"start": v(-156.89, -62.98) * mm, "end": v(-156.98, -63.2) * mm});
            skLineSegment(sketch, "E353", {"start": v(-140.76, -52.05) * mm, "end": v(-140.55, -52.06) * mm});
            skLineSegment(sketch, "E354", {"start": v(-143.26, -57.5) * mm, "end": v(-143.02, -57.6) * mm});
            skLineSegment(sketch, "E355", {"start": v(-163.08, -61.58) * mm, "end": v(-163.29, -61.75) * mm});
            skLineSegment(sketch, "E356", {"start": v(-170.67, -48.7) * mm, "end": v(-170.84, -48.76) * mm});
            skLineSegment(sketch, "E357", {"start": v(-156.82, -62.78) * mm, "end": v(-156.89, -62.98) * mm});
            skLineSegment(sketch, "E358", {"start": v(-140.94, -52.03) * mm, "end": v(-140.76, -52.05) * mm});
            skLineSegment(sketch, "E359", {"start": v(-143.47, -57.42) * mm, "end": v(-143.26, -57.5) * mm});
            skLineSegment(sketch, "E360", {"start": v(-162.9, -61.42) * mm, "end": v(-163.08, -61.58) * mm});
            skLineSegment(sketch, "E361", {"start": v(-170.52, -48.67) * mm, "end": v(-170.67, -48.7) * mm});
            skLineSegment(sketch, "E362", {"start": v(-156.77, -62.6) * mm, "end": v(-156.82, -62.78) * mm});
            skLineSegment(sketch, "E363", {"start": v(-141.1, -52) * mm, "end": v(-140.94, -52.03) * mm});
            skLineSegment(sketch, "E364", {"start": v(-143.66, -57.33) * mm, "end": v(-143.47, -57.42) * mm});
            skLineSegment(sketch, "E365", {"start": v(-162.74, -61.25) * mm, "end": v(-162.9, -61.42) * mm});
            skLineSegment(sketch, "E366", {"start": v(-170.3, -48.65) * mm, "end": v(-170.52, -48.67) * mm});
            skLineSegment(sketch, "E367", {"start": v(-156.74, -62.46) * mm, "end": v(-156.77, -62.6) * mm});
            skLineSegment(sketch, "E368", {"start": v(-141.3, -51.94) * mm, "end": v(-141.1, -52) * mm});
            skLineSegment(sketch, "E369", {"start": v(-143.82, -57.24) * mm, "end": v(-143.66, -57.33) * mm});
            skLineSegment(sketch, "E370", {"start": v(-162.6, -61.1) * mm, "end": v(-162.74, -61.25) * mm});
            skLineSegment(sketch, "E371", {"start": v(-169.72, -48.6) * mm, "end": v(-170.3, -48.65) * mm});
            skLineSegment(sketch, "E372", {"start": v(-156.71, -62.24) * mm, "end": v(-156.74, -62.46) * mm});
            skLineSegment(sketch, "E373", {"start": v(-141.86, -51.77) * mm, "end": v(-141.3, -51.94) * mm});
            skLineSegment(sketch, "E374", {"start": v(-143.94, -57.16) * mm, "end": v(-143.82, -57.24) * mm});
            skLineSegment(sketch, "E375", {"start": v(-162.48, -60.96) * mm, "end": v(-162.6, -61.1) * mm});
            skArc(sketch, "E376", {"start": v(-169.72, -48.6) * mm, "mid": v(-169.18, -48.33) * mm, "end": v(-168.97, -47.77) * mm});
            skLineSegment(sketch, "E377", {"start": v(-156.66, -61.66) * mm, "end": v(-156.71, -62.24) * mm});
            skArc(sketch, "E378", {"start": v(-141.86, -51.77) * mm, "mid": v(-142.46, -51.8) * mm, "end": v(-142.87, -52.25) * mm});
            skLineSegment(sketch, "E379", {"start": v(-144.12, -57.02) * mm, "end": v(-143.94, -57.16) * mm});
            skLineSegment(sketch, "E380", {"start": v(-162.4, -60.83) * mm, "end": v(-162.48, -60.96) * mm});
            skArc(sketch, "E381", {"start": v(-168.97, -47.06) * mm, "mid": v(-168.98, -47.41) * mm, "end": v(-168.97, -47.77) * mm});
            skArc(sketch, "E382", {"start": v(-159.64, -64.93) * mm, "mid": v(-158.99, -65.07) * mm, "end": v(-158.33, -65.19) * mm});
            skArc(sketch, "E383", {"start": v(-143.14, -52.9) * mm, "mid": v(-143, -52.58) * mm, "end": v(-142.87, -52.25) * mm});
            skLineSegment(sketch, "E384", {"start": v(-144.57, -56.65) * mm, "end": v(-144.12, -57.02) * mm});
            skLineSegment(sketch, "E385", {"start": v(-162.29, -60.63) * mm, "end": v(-162.4, -60.83) * mm});
            skArc(sketch, "E386", {"start": v(-168.97, -47.06) * mm, "mid": v(-169.18, -46.5) * mm, "end": v(-169.72, -46.23) * mm});
            skLineSegment(sketch, "E387", {"start": v(-159.93, -63.96) * mm, "end": v(-159.64, -64.93) * mm});
            skArc(sketch, "E388", {"start": v(-143.14, -52.9) * mm, "mid": v(-143.17, -53.5) * mm, "end": v(-142.77, -53.96) * mm});
            skArc(sketch, "E389", {"start": v(-144.57, -56.65) * mm, "mid": v(-145.14, -56.45) * mm, "end": v(-145.68, -56.7) * mm});
            skLineSegment(sketch, "E390", {"start": v(-162.02, -60.12) * mm, "end": v(-162.29, -60.63) * mm});
            skLineSegment(sketch, "E391", {"start": v(-172.47, -45.2) * mm, "end": v(-173.25, -44.56) * mm});
            skLineSegment(sketch, "E392", {"start": v(-160.1, -63.07) * mm, "end": v(-159.93, -63.96) * mm});
            skLineSegment(sketch, "E393", {"start": v(-140.62, -55.96) * mm, "end": v(-140.15, -56.85) * mm});
            skArc(sketch, "E394", {"start": v(-166.02, -62) * mm, "mid": v(-165.48, -62.38) * mm, "end": v(-164.92, -62.74) * mm});
            skLineSegment(sketch, "E395", {"start": v(-171.7, -45.68) * mm, "end": v(-172.47, -45.2) * mm});
            skLineSegment(sketch, "E396", {"start": v(-160.11, -62.81) * mm, "end": v(-160.1, -63.07) * mm});
            skLineSegment(sketch, "E397", {"start": v(-141.14, -55.22) * mm, "end": v(-140.62, -55.96) * mm});
            skArc(sketch, "E398", {"start": v(-146.18, -57.2) * mm, "mid": v(-145.93, -56.96) * mm, "end": v(-145.68, -56.7) * mm});
            skLineSegment(sketch, "E399", {"start": v(-165.92, -61) * mm, "end": v(-166.02, -62) * mm});
            skLineSegment(sketch, "E400", {"start": v(-171.48, -45.8) * mm, "end": v(-171.7, -45.68) * mm});
            skLineSegment(sketch, "E401", {"start": v(-160.13, -62.57) * mm, "end": v(-160.11, -62.81) * mm});
            skLineSegment(sketch, "E402", {"start": v(-141.3, -55.02) * mm, "end": v(-141.14, -55.22) * mm});
            skArc(sketch, "E403", {"start": v(-146.18, -57.2) * mm, "mid": v(-146.44, -57.75) * mm, "end": v(-146.24, -58.32) * mm});
            skLineSegment(sketch, "E404", {"start": v(-165.73, -60.11) * mm, "end": v(-165.92, -61) * mm});
            skLineSegment(sketch, "E405", {"start": v(-171.25, -45.91) * mm, "end": v(-171.48, -45.8) * mm});
            skLineSegment(sketch, "E406", {"start": v(-160.13, -62.34) * mm, "end": v(-160.13, -62.57) * mm});
            skLineSegment(sketch, "E407", {"start": v(-141.47, -54.84) * mm, "end": v(-141.3, -55.02) * mm});
            skLineSegment(sketch, "E408", {"start": v(-145.03, -61) * mm, "end": v(-144.93, -62) * mm});
            skLineSegment(sketch, "E409", {"start": v(-165.65, -59.86) * mm, "end": v(-165.73, -60.11) * mm});
            skLineSegment(sketch, "E410", {"start": v(-171.04, -46) * mm, "end": v(-171.25, -45.91) * mm});
            skLineSegment(sketch, "E411", {"start": v(-160.12, -62.13) * mm, "end": v(-160.13, -62.34) * mm});
            skLineSegment(sketch, "E412", {"start": v(-141.64, -54.68) * mm, "end": v(-141.47, -54.84) * mm});
            skLineSegment(sketch, "E413", {"start": v(-165.48, -35.4) * mm, "end": v(-165.57, -35.2) * mm});
            skLineSegment(sketch, "E414", {"start": v(-145.22, -60.11) * mm, "end": v(-145.03, -61) * mm});
            skLineSegment(sketch, "E415", {"start": v(-165.57, -59.63) * mm, "end": v(-165.65, -59.86) * mm});
            skLineSegment(sketch, "E416", {"start": v(-170.84, -46.07) * mm, "end": v(-171.04, -46) * mm});
            skLineSegment(sketch, "E417", {"start": v(-160.1, -61.94) * mm, "end": v(-160.12, -62.13) * mm});
            skLineSegment(sketch, "E418", {"start": v(-141.8, -54.54) * mm, "end": v(-141.64, -54.68) * mm});
            skLineSegment(sketch, "E419", {"start": v(-165.4, -35.6) * mm, "end": v(-165.48, -35.4) * mm});
            skLineSegment(sketch, "E420", {"start": v(-145.3, -59.86) * mm, "end": v(-145.22, -60.11) * mm});
            skLineSegment(sketch, "E421", {"start": v(-165.48, -59.42) * mm, "end": v(-165.57, -59.63) * mm});
            skLineSegment(sketch, "E422", {"start": v(-170.67, -46.12) * mm, "end": v(-170.84, -46.07) * mm});
            skLineSegment(sketch, "E423", {"start": v(-160.07, -61.8) * mm, "end": v(-160.1, -61.94) * mm});
            skLineSegment(sketch, "E424", {"start": v(-141.93, -54.42) * mm, "end": v(-141.8, -54.54) * mm});
            skLineSegment(sketch, "E425", {"start": v(-165.3, -35.76) * mm, "end": v(-165.4, -35.6) * mm});
            skLineSegment(sketch, "E426", {"start": v(-145.38, -59.63) * mm, "end": v(-145.3, -59.86) * mm});
            skLineSegment(sketch, "E427", {"start": v(-165.4, -59.23) * mm, "end": v(-165.48, -59.42) * mm});
            skLineSegment(sketch, "E428", {"start": v(-170.52, -46.15) * mm, "end": v(-170.67, -46.12) * mm});
            skLineSegment(sketch, "E429", {"start": v(-160, -61.58) * mm, "end": v(-160.07, -61.8) * mm});
            skLineSegment(sketch, "E430", {"start": v(-142.05, -54.34) * mm, "end": v(-141.93, -54.42) * mm});
            skLineSegment(sketch, "E431", {"start": v(-145.47, -59.42) * mm, "end": v(-145.38, -59.63) * mm});
            skLineSegment(sketch, "E432", {"start": v(-165.3, -59.07) * mm, "end": v(-165.4, -59.23) * mm});
            skLineSegment(sketch, "E433", {"start": v(-170.3, -46.18) * mm, "end": v(-170.52, -46.15) * mm});
            skLineSegment(sketch, "E434", {"start": v(-159.83, -61.03) * mm, "end": v(-160, -61.58) * mm});
            skLineSegment(sketch, "E435", {"start": v(-142.25, -54.23) * mm, "end": v(-142.05, -54.34) * mm});
            skLineSegment(sketch, "E436", {"start": v(-145.56, -59.23) * mm, "end": v(-145.47, -59.42) * mm});
            skLineSegment(sketch, "E437", {"start": v(-165.23, -58.95) * mm, "end": v(-165.3, -59.07) * mm});
            skLineSegment(sketch, "E438", {"start": v(-169.72, -46.23) * mm, "end": v(-170.3, -46.18) * mm});
            skArc(sketch, "E439", {"start": v(-159.83, -61.03) * mm, "mid": v(-159.87, -60.43) * mm, "end": v(-160.31, -60.02) * mm});
            skLineSegment(sketch, "E440", {"start": v(-142.77, -53.96) * mm, "end": v(-142.25, -54.23) * mm});
            skLineSegment(sketch, "E441", {"start": v(-145.65, -59.07) * mm, "end": v(-145.56, -59.23) * mm});
            skLineSegment(sketch, "E442", {"start": v(-165.08, -58.77) * mm, "end": v(-165.23, -58.95) * mm});
            skArc(sketch, "E443", {"start": v(-172.99, -43.25) * mm, "mid": v(-173.13, -43.9) * mm, "end": v(-173.25, -44.56) * mm});
            skArc(sketch, "E444", {"start": v(-160.97, -59.75) * mm, "mid": v(-160.64, -59.89) * mm, "end": v(-160.31, -60.02) * mm});
            skArc(sketch, "E445", {"start": v(-140.89, -57.96) * mm, "mid": v(-140.5, -57.41) * mm, "end": v(-140.15, -56.85) * mm});
            skLineSegment(sketch, "E446", {"start": v(-145.73, -58.95) * mm, "end": v(-145.65, -59.07) * mm});
            skLineSegment(sketch, "E447", {"start": v(-164.7, -58.32) * mm, "end": v(-165.08, -58.77) * mm});
            skLineSegment(sketch, "E448", {"start": v(-172.02, -42.96) * mm, "end": v(-172.99, -43.25) * mm});
            skArc(sketch, "E449", {"start": v(-160.97, -59.75) * mm, "mid": v(-161.57, -59.72) * mm, "end": v(-162.02, -60.12) * mm});
            skLineSegment(sketch, "E450", {"start": v(-141.9, -57.86) * mm, "end": v(-140.89, -57.96) * mm});
            skLineSegment(sketch, "E451", {"start": v(-145.87, -58.77) * mm, "end": v(-145.73, -58.95) * mm});
            skArc(sketch, "E452", {"start": v(-164.7, -58.32) * mm, "mid": v(-164.52, -57.75) * mm, "end": v(-164.77, -57.2) * mm});
            skLineSegment(sketch, "E453", {"start": v(-171.13, -42.8) * mm, "end": v(-172.02, -42.96) * mm});
            skLineSegment(sketch, "E454", {"start": v(-164.03, -62.26) * mm, "end": v(-164.92, -62.74) * mm});
            skLineSegment(sketch, "E455", {"start": v(-142.77, -57.67) * mm, "end": v(-141.9, -57.86) * mm});
            skLineSegment(sketch, "E456", {"start": v(-146.24, -58.32) * mm, "end": v(-145.87, -58.77) * mm});
            skLineSegment(sketch, "E457", {"start": v(-171.48, -49.02) * mm, "end": v(-171.7, -49.14) * mm});
            skLineSegment(sketch, "E458", {"start": v(-171.25, -48.91) * mm, "end": v(-171.48, -49.02) * mm});
            skLineSegment(sketch, "E459", {"start": v(-171.04, -48.83) * mm, "end": v(-171.25, -48.91) * mm});
            skLineSegment(sketch, "E460", {"start": v(-155.48, -50.31) * mm, "end": v(-155.48, -50.51) * mm});
            skLineSegment(sketch, "E461", {"start": v(-154.03, -49.92) * mm, "end": v(-153.93, -50.1) * mm});
            skLineSegment(sketch, "E462", {"start": v(-152.96, -48.86) * mm, "end": v(-152.8, -48.96) * mm});
            skLineSegment(sketch, "E463", {"start": v(-152.58, -47.41) * mm, "end": v(-152.38, -47.41) * mm});
            skLineSegment(sketch, "E464", {"start": v(-152.96, -45.96) * mm, "end": v(-152.8, -45.86) * mm});
            skLineSegment(sketch, "E465", {"start": v(-154.03, -44.9) * mm, "end": v(-153.93, -44.73) * mm});
            skArc(sketch, "E466", {"start": v(-152.96, -45.96) * mm, "mid": v(-153.43, -45.36) * mm, "end": v(-154.03, -44.9) * mm});
            skArc(sketch, "E467", {"start": v(-152.38, -47.41) * mm, "mid": v(-152.48, -46.61) * mm, "end": v(-152.8, -45.86) * mm});
            skArc(sketch, "E468", {"start": v(-152.96, -48.86) * mm, "mid": v(-152.67, -48.16) * mm, "end": v(-152.58, -47.41) * mm});
            skArc(sketch, "E469", {"start": v(-153.93, -50.1) * mm, "mid": v(-153.28, -49.6) * mm, "end": v(-152.8, -48.96) * mm});
            skArc(sketch, "E470", {"start": v(-155.48, -50.31) * mm, "mid": v(-154.73, -50.21) * mm, "end": v(-154.03, -49.92) * mm});
            skArc(sketch, "E471", {"start": v(-157.03, -50.1) * mm, "mid": v(-156.28, -50.4) * mm, "end": v(-155.48, -50.51) * mm});
            skArc(sketch, "E472", {"start": v(-158.58, -47.41) * mm, "mid": v(-158.47, -48.22) * mm, "end": v(-158.16, -48.96) * mm});
            skArc(sketch, "E473", {"start": v(-157.03, -44.73) * mm, "mid": v(-157.67, -45.22) * mm, "end": v(-158.16, -45.86) * mm});
            skArc(sketch, "E474", {"start": v(-157.99, -45.96) * mm, "mid": v(-158.28, -46.66) * mm, "end": v(-158.38, -47.41) * mm});
            skArc(sketch, "E475", {"start": v(-153.93, -44.73) * mm, "mid": v(-154.67, -44.42) * mm, "end": v(-155.48, -44.31) * mm});
            skArc(sketch, "E476", {"start": v(-155.48, -44.51) * mm, "mid": v(-156.23, -44.61) * mm, "end": v(-156.93, -44.9) * mm});
            skLineSegment(sketch, "E477", {"start": v(-155.48, -44.51) * mm, "end": v(-155.48, -44.31) * mm});
            skLineSegment(sketch, "E478", {"start": v(-156.93, -44.9) * mm, "end": v(-157.03, -44.73) * mm});
            skLineSegment(sketch, "E479", {"start": v(-157.99, -45.96) * mm, "end": v(-158.16, -45.86) * mm});
            skLineSegment(sketch, "E480", {"start": v(-158.38, -47.41) * mm, "end": v(-158.58, -47.41) * mm});
            skLineSegment(sketch, "E481", {"start": v(-157.99, -48.86) * mm, "end": v(-158.16, -48.96) * mm});
            skLineSegment(sketch, "E482", {"start": v(-156.93, -49.92) * mm, "end": v(-157.03, -50.1) * mm});
            skSolve(sketch);
        }
        {
            var Q0;
            Q0 = qSketchRegion(id + "F0", true);
            extrude(context, id + "F1", {"entities" : qUnion([Q0]), "oppositeDirection" : true, "depth" : 10 * mm, "offsetDistance" : 25 * mm});
        }
        {
            var Q0;
            Q0=qCreatedBy(makeId("Front.planeOp"),FACE);
            var sketch = newSketch(context, id + "F2", { "sketchPlane" : qUnion([Q0])});
            skLineSegment(sketch, "E483", {"start": v(-21.75, -87.57) * mm, "end": v(-21.17, -87.32) * mm});
            skLineSegment(sketch, "E484", {"start": v(-22.1, -87.97) * mm, "end": v(-21.75, -87.57) * mm});
            skLineSegment(sketch, "E485", {"start": v(-22.4, -88.73) * mm, "end": v(-22.1, -87.97) * mm});
            skLineSegment(sketch, "E486", {"start": v(-22.48, -89.38) * mm, "end": v(-22.4, -88.73) * mm});
            skLineSegment(sketch, "E487", {"start": v(-22.34, -90.06) * mm, "end": v(-22.48, -89.38) * mm});
            skLineSegment(sketch, "E488", {"start": v(-22.04, -90.44) * mm, "end": v(-22.34, -90.06) * mm});
            skLineSegment(sketch, "E489", {"start": v(-21.45, -90.73) * mm, "end": v(-22.04, -90.44) * mm});
            skLineSegment(sketch, "E490", {"start": v(-20.9, -90.76) * mm, "end": v(-21.45, -90.73) * mm});
            skLineSegment(sketch, "E491", {"start": v(-20.31, -90.48) * mm, "end": v(-20.9, -90.76) * mm});
            skLineSegment(sketch, "E492", {"start": v(-20.31, -90.48) * mm, "end": v(-20.28, -90.48) * mm});
            skLineSegment(sketch, "E493", {"start": v(-20.28, -90.48) * mm, "end": v(-20.32, -90.93) * mm});
            skLineSegment(sketch, "E494", {"start": v(-20.32, -90.93) * mm, "end": v(-19.92, -91.03) * mm});
            skLineSegment(sketch, "E495", {"start": v(-19.92, -91.03) * mm, "end": v(-18.83, -86.4) * mm});
            skLineSegment(sketch, "E496", {"start": v(-24.85, -89.32) * mm, "end": v(-24.36, -89.3) * mm});
            skLineSegment(sketch, "E497", {"start": v(-25.45, -89.22) * mm, "end": v(-24.85, -89.32) * mm});
            skLineSegment(sketch, "E498", {"start": v(-25.82, -89.05) * mm, "end": v(-25.45, -89.22) * mm});
            skLineSegment(sketch, "E499", {"start": v(-26.12, -88.7) * mm, "end": v(-25.82, -89.05) * mm});
            skLineSegment(sketch, "E500", {"start": v(-26.22, -88.34) * mm, "end": v(-26.12, -88.7) * mm});
            skLineSegment(sketch, "E501", {"start": v(-26.16, -87.76) * mm, "end": v(-26.22, -88.34) * mm});
            skLineSegment(sketch, "E502", {"start": v(-26.16, -87.76) * mm, "end": v(-23.95, -88.4) * mm});
            skLineSegment(sketch, "E503", {"start": v(-23.95, -88.4) * mm, "end": v(-23.86, -88.1) * mm});
            skLineSegment(sketch, "E504", {"start": v(-23.78, -87.55) * mm, "end": v(-23.86, -88.1) * mm});
            skLineSegment(sketch, "E505", {"start": v(-23.9, -86.95) * mm, "end": v(-23.78, -87.55) * mm});
            skLineSegment(sketch, "E506", {"start": v(-24.19, -86.57) * mm, "end": v(-23.9, -86.95) * mm});
            skLineSegment(sketch, "E507", {"start": v(-24.75, -86.27) * mm, "end": v(-24.19, -86.57) * mm});
            skLineSegment(sketch, "E508", {"start": v(-25.3, -86.21) * mm, "end": v(-24.75, -86.27) * mm});
            skLineSegment(sketch, "E509", {"start": v(-25.9, -86.43) * mm, "end": v(-25.3, -86.21) * mm});
            skLineSegment(sketch, "E510", {"start": v(-26.3, -86.82) * mm, "end": v(-25.9, -86.43) * mm});
            skLineSegment(sketch, "E511", {"start": v(-26.65, -87.56) * mm, "end": v(-26.3, -86.82) * mm});
            skLineSegment(sketch, "E512", {"start": v(-26.75, -88.2) * mm, "end": v(-26.65, -87.56) * mm});
            skLineSegment(sketch, "E513", {"start": v(-26.59, -88.88) * mm, "end": v(-26.75, -88.2) * mm});
            skLineSegment(sketch, "E514", {"start": v(-26.25, -89.3) * mm, "end": v(-26.59, -88.88) * mm});
            skLineSegment(sketch, "E515", {"start": v(-25.59, -89.64) * mm, "end": v(-26.25, -89.3) * mm});
            skLineSegment(sketch, "E516", {"start": v(-25.32, -89.7) * mm, "end": v(-25.59, -89.64) * mm});
            skLineSegment(sketch, "E517", {"start": v(-25.02, -89.75) * mm, "end": v(-25.32, -89.7) * mm});
            skLineSegment(sketch, "E518", {"start": v(-24.8, -89.76) * mm, "end": v(-25.02, -89.75) * mm});
            skLineSegment(sketch, "E519", {"start": v(-24.48, -89.73) * mm, "end": v(-24.8, -89.76) * mm});
            skLineSegment(sketch, "E520", {"start": v(-24.48, -89.73) * mm, "end": v(-24.36, -89.3) * mm});
            skLineSegment(sketch, "E521", {"start": v(-56.9, 72.66) * mm, "end": v(-57.3, 72.35) * mm});
            skLineSegment(sketch, "E522", {"start": v(-57.3, 72.35) * mm, "end": v(-55.23, 69.72) * mm});
            skLineSegment(sketch, "E523", {"start": v(-55.23, 69.72) * mm, "end": v(-54.84, 70.03) * mm});
            skLineSegment(sketch, "E524", {"start": v(-54.84, 70.03) * mm, "end": v(-56.9, 72.66) * mm});
            skLineSegment(sketch, "E525", {"start": v(-56.8, 69.1) * mm, "end": v(-55.87, 67.77) * mm});
            skLineSegment(sketch, "E526", {"start": v(-55.87, 67.77) * mm, "end": v(-55.43, 68.13) * mm});
            skLineSegment(sketch, "E527", {"start": v(-55.43, 68.13) * mm, "end": v(-56.54, 69.3) * mm});
            skLineSegment(sketch, "E528", {"start": v(-56.54, 69.3) * mm, "end": v(-56.8, 69.1) * mm});
            skLineSegment(sketch, "E529", {"start": v(-47.87, 78.88) * mm, "end": v(-48.3, 78.61) * mm});
            skLineSegment(sketch, "E530", {"start": v(-48.3, 78.61) * mm, "end": v(-46.56, 75.76) * mm});
            skLineSegment(sketch, "E531", {"start": v(-46.56, 75.76) * mm, "end": v(-46.13, 76.02) * mm});
            skLineSegment(sketch, "E532", {"start": v(-46.13, 76.02) * mm, "end": v(-47.87, 78.88) * mm});
            skLineSegment(sketch, "E533", {"start": v(-53.64, 73.42) * mm, "end": v(-55.2, 73.96) * mm});
            skLineSegment(sketch, "E534", {"start": v(-55.2, 73.96) * mm, "end": v(-55.66, 73.63) * mm});
            skLineSegment(sketch, "E535", {"start": v(-55.66, 73.63) * mm, "end": v(-53.66, 72.96) * mm});
            skLineSegment(sketch, "E536", {"start": v(-53.66, 72.96) * mm, "end": v(-53.64, 70.96) * mm});
            skLineSegment(sketch, "E537", {"start": v(-53.64, 70.96) * mm, "end": v(-53.18, 71.3) * mm});
            skLineSegment(sketch, "E538", {"start": v(-53.18, 71.3) * mm, "end": v(-53.22, 72.85) * mm});
            skLineSegment(sketch, "E539", {"start": v(-53.22, 72.85) * mm, "end": v(-51.75, 72.33) * mm});
            skLineSegment(sketch, "E540", {"start": v(-51.75, 72.33) * mm, "end": v(-51.29, 72.67) * mm});
            skLineSegment(sketch, "E541", {"start": v(-51.29, 72.67) * mm, "end": v(-53.19, 73.3) * mm});
            skLineSegment(sketch, "E542", {"start": v(-53.19, 73.3) * mm, "end": v(-53.2, 75.41) * mm});
            skLineSegment(sketch, "E543", {"start": v(-53.2, 75.41) * mm, "end": v(-53.67, 75.07) * mm});
            skLineSegment(sketch, "E544", {"start": v(-53.67, 75.07) * mm, "end": v(-53.64, 73.42) * mm});
            skLineSegment(sketch, "E545", {"start": v(-73.05, 51.95) * mm, "end": v(-72.51, 51.64) * mm});
            skLineSegment(sketch, "E546", {"start": v(-72.51, 51.64) * mm, "end": v(-72.27, 51.98) * mm});
            skLineSegment(sketch, "E547", {"start": v(-72.27, 51.98) * mm, "end": v(-75, 53.92) * mm});
            skLineSegment(sketch, "E548", {"start": v(-75, 53.92) * mm, "end": v(-75.3, 53.5) * mm});
            skLineSegment(sketch, "E549", {"start": v(-75.3, 53.5) * mm, "end": v(-73.83, 52.47) * mm});
            skLineSegment(sketch, "E550", {"start": v(-73.53, 52.19) * mm, "end": v(-73.83, 52.47) * mm});
            skLineSegment(sketch, "E551", {"start": v(-73.33, 51.76) * mm, "end": v(-73.53, 52.19) * mm});
            skLineSegment(sketch, "E552", {"start": v(-73.3, 51.4) * mm, "end": v(-73.33, 51.76) * mm});
            skLineSegment(sketch, "E553", {"start": v(-73.46, 51) * mm, "end": v(-73.3, 51.4) * mm});
            skLineSegment(sketch, "E554", {"start": v(-73.55, 50.88) * mm, "end": v(-73.46, 51) * mm});
            skLineSegment(sketch, "E555", {"start": v(-73.7, 50.73) * mm, "end": v(-73.55, 50.88) * mm});
            skLineSegment(sketch, "E556", {"start": v(-73.7, 50.73) * mm, "end": v(-73.37, 50.4) * mm});
            skLineSegment(sketch, "E557", {"start": v(-73.25, 50.52) * mm, "end": v(-73.37, 50.4) * mm});
            skLineSegment(sketch, "E558", {"start": v(-73.1, 50.7) * mm, "end": v(-73.25, 50.52) * mm});
            skLineSegment(sketch, "E559", {"start": v(-72.98, 50.94) * mm, "end": v(-73.1, 50.7) * mm});
            skLineSegment(sketch, "E560", {"start": v(-72.92, 51.28) * mm, "end": v(-72.98, 50.94) * mm});
            skLineSegment(sketch, "E561", {"start": v(-72.94, 51.56) * mm, "end": v(-72.92, 51.28) * mm});
            skLineSegment(sketch, "E562", {"start": v(-73.07, 51.93) * mm, "end": v(-72.94, 51.56) * mm});
            skLineSegment(sketch, "E563", {"start": v(-73.07, 51.93) * mm, "end": v(-73.05, 51.95) * mm});
            skLineSegment(sketch, "E564", {"start": v(-76.94, 51.12) * mm, "end": v(-77.23, 50.7) * mm});
            skLineSegment(sketch, "E565", {"start": v(-77.23, 50.7) * mm, "end": v(-74.44, 48.84) * mm});
            skLineSegment(sketch, "E566", {"start": v(-74.44, 48.84) * mm, "end": v(-74.16, 49.26) * mm});
            skLineSegment(sketch, "E567", {"start": v(-74.16, 49.26) * mm, "end": v(-76.94, 51.12) * mm});
            skLineSegment(sketch, "E568", {"start": v(-67.98, 61.81) * mm, "end": v(-68.18, 61.37) * mm});
            skLineSegment(sketch, "E569", {"start": v(-67.62, 62.3) * mm, "end": v(-67.98, 61.81) * mm});
            skLineSegment(sketch, "E570", {"start": v(-67.3, 62.56) * mm, "end": v(-67.62, 62.3) * mm});
            skLineSegment(sketch, "E571", {"start": v(-66.86, 62.68) * mm, "end": v(-67.3, 62.56) * mm});
            skLineSegment(sketch, "E572", {"start": v(-66.49, 62.6) * mm, "end": v(-66.86, 62.68) * mm});
            skLineSegment(sketch, "E573", {"start": v(-66, 62.28) * mm, "end": v(-66.49, 62.6) * mm});
            skLineSegment(sketch, "E574", {"start": v(-66, 62.28) * mm, "end": v(-67.57, 60.6) * mm});
            skLineSegment(sketch, "E575", {"start": v(-67.57, 60.6) * mm, "end": v(-67.33, 60.38) * mm});
            skLineSegment(sketch, "E576", {"start": v(-66.89, 60.06) * mm, "end": v(-67.33, 60.38) * mm});
            skLineSegment(sketch, "E577", {"start": v(-66.29, 59.9) * mm, "end": v(-66.89, 60.06) * mm});
            skLineSegment(sketch, "E578", {"start": v(-65.82, 59.98) * mm, "end": v(-66.29, 59.9) * mm});
            skLineSegment(sketch, "E579", {"start": v(-65.3, 60.35) * mm, "end": v(-65.82, 59.98) * mm});
            skLineSegment(sketch, "E580", {"start": v(-65, 60.8) * mm, "end": v(-65.3, 60.35) * mm});
            skLineSegment(sketch, "E581", {"start": v(-64.93, 61.46) * mm, "end": v(-65, 60.8) * mm});
            skLineSegment(sketch, "E582", {"start": v(-65.1, 61.99) * mm, "end": v(-64.93, 61.46) * mm});
            skLineSegment(sketch, "E583", {"start": v(-65.6, 62.63) * mm, "end": v(-65.1, 61.99) * mm});
            skLineSegment(sketch, "E584", {"start": v(-66.12, 63) * mm, "end": v(-65.6, 62.63) * mm});
            skLineSegment(sketch, "E585", {"start": v(-66.8, 63.17) * mm, "end": v(-66.12, 63) * mm});
            skLineSegment(sketch, "E586", {"start": v(-67.33, 63.06) * mm, "end": v(-66.8, 63.17) * mm});
            skLineSegment(sketch, "E587", {"start": v(-67.93, 62.62) * mm, "end": v(-67.33, 63.06) * mm});
            skLineSegment(sketch, "E588", {"start": v(-68.12, 62.4) * mm, "end": v(-67.93, 62.62) * mm});
            skLineSegment(sketch, "E589", {"start": v(-68.3, 62.16) * mm, "end": v(-68.12, 62.4) * mm});
            skLineSegment(sketch, "E590", {"start": v(-68.4, 61.96) * mm, "end": v(-68.3, 62.16) * mm});
            skLineSegment(sketch, "E591", {"start": v(-68.51, 61.67) * mm, "end": v(-68.4, 61.96) * mm});
            skLineSegment(sketch, "E592", {"start": v(-68.51, 61.67) * mm, "end": v(-68.18, 61.37) * mm});
            skLineSegment(sketch, "E593", {"start": v(-62.96, 63.42) * mm, "end": v(-63.65, 62.74) * mm});
            skLineSegment(sketch, "E594", {"start": v(-63.65, 62.74) * mm, "end": v(-63.37, 62.46) * mm});
            skLineSegment(sketch, "E595", {"start": v(-63.37, 62.46) * mm, "end": v(-62.68, 63.15) * mm});
            skLineSegment(sketch, "E596", {"start": v(-62.68, 63.15) * mm, "end": v(-62.13, 62.6) * mm});
            skLineSegment(sketch, "E597", {"start": v(-62.13, 62.6) * mm, "end": v(-61.93, 62.8) * mm});
            skLineSegment(sketch, "E598", {"start": v(-61.93, 62.8) * mm, "end": v(-62.28, 63.46) * mm});
            skLineSegment(sketch, "E599", {"start": v(-62.28, 63.46) * mm, "end": v(-62.08, 63.94) * mm});
            skLineSegment(sketch, "E600", {"start": v(-62.08, 63.94) * mm, "end": v(-62.26, 64.12) * mm});
            skLineSegment(sketch, "E601", {"start": v(-62.26, 64.12) * mm, "end": v(-62.6, 63.78) * mm});
            skLineSegment(sketch, "E602", {"start": v(-62.6, 63.78) * mm, "end": v(-64, 65.2) * mm});
            skLineSegment(sketch, "E603", {"start": v(-64.62, 65.56) * mm, "end": v(-64, 65.2) * mm});
            skLineSegment(sketch, "E604", {"start": v(-65.4, 65.24) * mm, "end": v(-64.62, 65.56) * mm});
            skLineSegment(sketch, "E605", {"start": v(-65.49, 65.15) * mm, "end": v(-65.4, 65.24) * mm});
            skLineSegment(sketch, "E606", {"start": v(-65.6, 65.02) * mm, "end": v(-65.49, 65.15) * mm});
            skLineSegment(sketch, "E607", {"start": v(-65.66, 64.9) * mm, "end": v(-65.6, 65.02) * mm});
            skLineSegment(sketch, "E608", {"start": v(-65.72, 64.8) * mm, "end": v(-65.66, 64.9) * mm});
            skLineSegment(sketch, "E609", {"start": v(-65.72, 64.8) * mm, "end": v(-65.45, 64.52) * mm});
            skLineSegment(sketch, "E610", {"start": v(-65.4, 64.59) * mm, "end": v(-65.45, 64.52) * mm});
            skLineSegment(sketch, "E611", {"start": v(-65.33, 64.7) * mm, "end": v(-65.4, 64.59) * mm});
            skLineSegment(sketch, "E612", {"start": v(-65.26, 64.78) * mm, "end": v(-65.33, 64.7) * mm});
            skLineSegment(sketch, "E613", {"start": v(-65.16, 64.89) * mm, "end": v(-65.26, 64.78) * mm});
            skLineSegment(sketch, "E614", {"start": v(-65, 65) * mm, "end": v(-65.16, 64.89) * mm});
            skLineSegment(sketch, "E615", {"start": v(-64.77, 65.05) * mm, "end": v(-65, 65) * mm});
            skLineSegment(sketch, "E616", {"start": v(-64.58, 65) * mm, "end": v(-64.77, 65.05) * mm});
            skLineSegment(sketch, "E617", {"start": v(-64.34, 64.82) * mm, "end": v(-64.58, 65) * mm});
            skLineSegment(sketch, "E618", {"start": v(-64.34, 64.82) * mm, "end": v(-62.96, 63.42) * mm});
            skLineSegment(sketch, "E619", {"start": v(-70.93, 59.12) * mm, "end": v(-71.26, 58.73) * mm});
            skLineSegment(sketch, "E620", {"start": v(-71.26, 58.73) * mm, "end": v(-67.62, 55.7) * mm});
            skLineSegment(sketch, "E621", {"start": v(-67.62, 55.7) * mm, "end": v(-67.3, 56.08) * mm});
            skLineSegment(sketch, "E622", {"start": v(-67.3, 56.08) * mm, "end": v(-70.93, 59.12) * mm});
            skLineSegment(sketch, "E623", {"start": v(-69.76, 60.5) * mm, "end": v(-70.1, 60.11) * mm});
            skLineSegment(sketch, "E624", {"start": v(-70.1, 60.11) * mm, "end": v(-66.5, 57) * mm});
            skLineSegment(sketch, "E625", {"start": v(-66.5, 57) * mm, "end": v(-66.18, 57.38) * mm});
            skLineSegment(sketch, "E626", {"start": v(-66.18, 57.38) * mm, "end": v(-69.76, 60.5) * mm});
            skLineSegment(sketch, "E627", {"start": v(-83, 34.11) * mm, "end": v(-82.4, 33.93) * mm});
            skLineSegment(sketch, "E628", {"start": v(-82.4, 33.93) * mm, "end": v(-82.24, 34.32) * mm});
            skLineSegment(sketch, "E629", {"start": v(-82.24, 34.32) * mm, "end": v(-85.33, 35.59) * mm});
            skLineSegment(sketch, "E630", {"start": v(-85.33, 35.59) * mm, "end": v(-85.52, 35.12) * mm});
            skLineSegment(sketch, "E631", {"start": v(-85.52, 35.12) * mm, "end": v(-83.86, 34.44) * mm});
            skLineSegment(sketch, "E632", {"start": v(-83.51, 34.23) * mm, "end": v(-83.86, 34.44) * mm});
            skLineSegment(sketch, "E633", {"start": v(-83.21, 33.86) * mm, "end": v(-83.51, 34.23) * mm});
            skLineSegment(sketch, "E634", {"start": v(-83.1, 33.52) * mm, "end": v(-83.21, 33.86) * mm});
            skLineSegment(sketch, "E635", {"start": v(-83.17, 33.1) * mm, "end": v(-83.1, 33.52) * mm});
            skLineSegment(sketch, "E636", {"start": v(-83.24, 32.96) * mm, "end": v(-83.17, 33.1) * mm});
            skLineSegment(sketch, "E637", {"start": v(-83.35, 32.77) * mm, "end": v(-83.24, 32.96) * mm});
            skLineSegment(sketch, "E638", {"start": v(-83.35, 32.77) * mm, "end": v(-82.95, 32.53) * mm});
            skLineSegment(sketch, "E639", {"start": v(-82.86, 32.67) * mm, "end": v(-82.95, 32.53) * mm});
            skLineSegment(sketch, "E640", {"start": v(-82.76, 32.88) * mm, "end": v(-82.86, 32.67) * mm});
            skLineSegment(sketch, "E641", {"start": v(-82.69, 33.14) * mm, "end": v(-82.76, 32.88) * mm});
            skLineSegment(sketch, "E642", {"start": v(-82.7, 33.48) * mm, "end": v(-82.69, 33.14) * mm});
            skLineSegment(sketch, "E643", {"start": v(-82.8, 33.75) * mm, "end": v(-82.7, 33.48) * mm});
            skLineSegment(sketch, "E644", {"start": v(-83, 34.09) * mm, "end": v(-82.8, 33.75) * mm});
            skLineSegment(sketch, "E645", {"start": v(-83, 34.09) * mm, "end": v(-83, 34.11) * mm});
            skLineSegment(sketch, "E646", {"start": v(-80.66, 36.55) * mm, "end": v(-80.94, 36.7) * mm});
            skLineSegment(sketch, "E647", {"start": v(-80.44, 36.33) * mm, "end": v(-80.66, 36.55) * mm});
            skLineSegment(sketch, "E648", {"start": v(-80.39, 36.14) * mm, "end": v(-80.44, 36.33) * mm});
            skLineSegment(sketch, "E649", {"start": v(-80.45, 35.86) * mm, "end": v(-80.39, 36.14) * mm});
            skLineSegment(sketch, "E650", {"start": v(-80.54, 35.69) * mm, "end": v(-80.45, 35.86) * mm});
            skLineSegment(sketch, "E651", {"start": v(-80.74, 35.45) * mm, "end": v(-80.54, 35.69) * mm});
            skLineSegment(sketch, "E652", {"start": v(-80.74, 35.45) * mm, "end": v(-80.42, 35.16) * mm});
            skLineSegment(sketch, "E653", {"start": v(-80.23, 35.4) * mm, "end": v(-80.42, 35.16) * mm});
            skLineSegment(sketch, "E654", {"start": v(-80.07, 35.68) * mm, "end": v(-80.23, 35.4) * mm});
            skLineSegment(sketch, "E655", {"start": v(-79.98, 36.45) * mm, "end": v(-80.07, 35.68) * mm});
            skLineSegment(sketch, "E656", {"start": v(-80.74, 37.17) * mm, "end": v(-79.98, 36.45) * mm});
            skLineSegment(sketch, "E657", {"start": v(-80.74, 37.17) * mm, "end": v(-80.91, 37.25) * mm});
            skLineSegment(sketch, "E658", {"start": v(-80.91, 37.25) * mm, "end": v(-80.83, 37.87) * mm});
            skLineSegment(sketch, "E659", {"start": v(-80.83, 37.87) * mm, "end": v(-81.04, 37.96) * mm});
            skLineSegment(sketch, "E660", {"start": v(-81.04, 37.96) * mm, "end": v(-81.29, 37.42) * mm});
            skLineSegment(sketch, "E661", {"start": v(-81.29, 37.42) * mm, "end": v(-83.97, 38.64) * mm});
            skLineSegment(sketch, "E662", {"start": v(-83.97, 38.64) * mm, "end": v(-84.18, 38.18) * mm});
            skLineSegment(sketch, "E663", {"start": v(-84.18, 38.18) * mm, "end": v(-81.5, 36.96) * mm});
            skLineSegment(sketch, "E664", {"start": v(-81.5, 36.96) * mm, "end": v(-81.85, 36.18) * mm});
            skLineSegment(sketch, "E665", {"start": v(-81.85, 36.18) * mm, "end": v(-81.5, 36.02) * mm});
            skLineSegment(sketch, "E666", {"start": v(-81.5, 36.02) * mm, "end": v(-81.14, 36.8) * mm});
            skLineSegment(sketch, "E667", {"start": v(-81.14, 36.8) * mm, "end": v(-80.94, 36.7) * mm});
            skLineSegment(sketch, "E668", {"start": v(-47.26, -74.98) * mm, "end": v(-49.58, -78.8) * mm});
            skLineSegment(sketch, "E669", {"start": v(-49.58, -78.8) * mm, "end": v(-48.52, -79.44) * mm});
            skLineSegment(sketch, "E670", {"start": v(-47.7, -79.8) * mm, "end": v(-48.52, -79.44) * mm});
            skLineSegment(sketch, "E671", {"start": v(-46.74, -79.83) * mm, "end": v(-47.7, -79.8) * mm});
            skLineSegment(sketch, "E672", {"start": v(-46.07, -79.52) * mm, "end": v(-46.74, -79.83) * mm});
            skLineSegment(sketch, "E673", {"start": v(-45.35, -78.7) * mm, "end": v(-46.07, -79.52) * mm});
            skLineSegment(sketch, "E674", {"start": v(-45.02, -77.94) * mm, "end": v(-45.35, -78.7) * mm});
            skLineSegment(sketch, "E675", {"start": v(-45, -77.03) * mm, "end": v(-45.02, -77.94) * mm});
            skLineSegment(sketch, "E676", {"start": v(-45.31, -76.38) * mm, "end": v(-45, -77.03) * mm});
            skLineSegment(sketch, "E677", {"start": v(-46.09, -75.7) * mm, "end": v(-45.31, -76.38) * mm});
            skLineSegment(sketch, "E678", {"start": v(-46.09, -75.7) * mm, "end": v(-47.26, -74.98) * mm});
            skLineSegment(sketch, "E679", {"start": v(-42.83, -82.16) * mm, "end": v(-42.34, -82.25) * mm});
            skLineSegment(sketch, "E680", {"start": v(-43.39, -81.94) * mm, "end": v(-42.83, -82.16) * mm});
            skLineSegment(sketch, "E681", {"start": v(-43.72, -81.7) * mm, "end": v(-43.39, -81.94) * mm});
            skLineSegment(sketch, "E682", {"start": v(-43.95, -81.3) * mm, "end": v(-43.72, -81.7) * mm});
            skLineSegment(sketch, "E683", {"start": v(-43.97, -80.92) * mm, "end": v(-43.95, -81.3) * mm});
            skLineSegment(sketch, "E684", {"start": v(-43.79, -80.37) * mm, "end": v(-43.97, -80.92) * mm});
            skLineSegment(sketch, "E685", {"start": v(-43.79, -80.37) * mm, "end": v(-41.76, -81.46) * mm});
            skLineSegment(sketch, "E686", {"start": v(-41.76, -81.46) * mm, "end": v(-41.6, -81.17) * mm});
            skLineSegment(sketch, "E687", {"start": v(-41.41, -80.66) * mm, "end": v(-41.6, -81.17) * mm});
            skLineSegment(sketch, "E688", {"start": v(-41.41, -80.04) * mm, "end": v(-41.41, -80.66) * mm});
            skLineSegment(sketch, "E689", {"start": v(-41.6, -79.61) * mm, "end": v(-41.41, -80.04) * mm});
            skLineSegment(sketch, "E690", {"start": v(-42.1, -79.2) * mm, "end": v(-41.6, -79.61) * mm});
            skLineSegment(sketch, "E691", {"start": v(-42.61, -79.03) * mm, "end": v(-42.1, -79.2) * mm});
            skLineSegment(sketch, "E692", {"start": v(-43.26, -79.12) * mm, "end": v(-42.61, -79.03) * mm});
            skLineSegment(sketch, "E693", {"start": v(-43.73, -79.42) * mm, "end": v(-43.26, -79.12) * mm});
            skLineSegment(sketch, "E694", {"start": v(-44.22, -80.06) * mm, "end": v(-43.73, -79.42) * mm});
            skLineSegment(sketch, "E695", {"start": v(-44.45, -80.66) * mm, "end": v(-44.22, -80.06) * mm});
            skLineSegment(sketch, "E696", {"start": v(-44.43, -81.37) * mm, "end": v(-44.45, -80.66) * mm});
            skLineSegment(sketch, "E697", {"start": v(-44.2, -81.85) * mm, "end": v(-44.43, -81.37) * mm});
            skLineSegment(sketch, "E698", {"start": v(-43.62, -82.32) * mm, "end": v(-44.2, -81.85) * mm});
            skLineSegment(sketch, "E699", {"start": v(-43.37, -82.45) * mm, "end": v(-43.62, -82.32) * mm});
            skLineSegment(sketch, "E700", {"start": v(-43.08, -82.55) * mm, "end": v(-43.37, -82.45) * mm});
            skLineSegment(sketch, "E701", {"start": v(-41.87, -80.29) * mm, "end": v(-41.87, -80.19) * mm});
            skLineSegment(sketch, "E702", {"start": v(-41.88, -80.4) * mm, "end": v(-41.87, -80.29) * mm});
            skLineSegment(sketch, "E703", {"start": v(-41.9, -80.5) * mm, "end": v(-41.88, -80.4) * mm});
            skLineSegment(sketch, "E704", {"start": v(-41.94, -80.6) * mm, "end": v(-41.9, -80.5) * mm});
            skLineSegment(sketch, "E705", {"start": v(-41.98, -80.72) * mm, "end": v(-41.94, -80.6) * mm});
            skLineSegment(sketch, "E706", {"start": v(-42.04, -80.84) * mm, "end": v(-41.98, -80.72) * mm});
            skLineSegment(sketch, "E707", {"start": v(-42.04, -80.84) * mm, "end": v(-43.58, -80.01) * mm});
            skLineSegment(sketch, "E708", {"start": v(-48.9, -78.68) * mm, "end": v(-47.05, -75.64) * mm});
            skLineSegment(sketch, "E709", {"start": v(-47.05, -75.64) * mm, "end": v(-46.4, -76.03) * mm});
            skLineSegment(sketch, "E710", {"start": v(-46.2, -76.16) * mm, "end": v(-46.4, -76.03) * mm});
            skLineSegment(sketch, "E711", {"start": v(-46.02, -76.3) * mm, "end": v(-46.2, -76.16) * mm});
            skLineSegment(sketch, "E712", {"start": v(-45.87, -76.45) * mm, "end": v(-46.02, -76.3) * mm});
            skLineSegment(sketch, "E713", {"start": v(-45.75, -76.6) * mm, "end": v(-45.87, -76.45) * mm});
            skLineSegment(sketch, "E714", {"start": v(-45.65, -76.76) * mm, "end": v(-45.75, -76.6) * mm});
            skLineSegment(sketch, "E715", {"start": v(-45.57, -76.92) * mm, "end": v(-45.65, -76.76) * mm});
            skLineSegment(sketch, "E716", {"start": v(-45.52, -77.08) * mm, "end": v(-45.57, -76.92) * mm});
            skLineSegment(sketch, "E717", {"start": v(-45.5, -77.26) * mm, "end": v(-45.52, -77.08) * mm});
            skLineSegment(sketch, "E718", {"start": v(-45.49, -77.45) * mm, "end": v(-45.5, -77.26) * mm});
            skLineSegment(sketch, "E719", {"start": v(-45.51, -77.64) * mm, "end": v(-45.49, -77.45) * mm});
            skLineSegment(sketch, "E720", {"start": v(-45.56, -77.83) * mm, "end": v(-45.51, -77.64) * mm});
            skLineSegment(sketch, "E721", {"start": v(-45.63, -78.03) * mm, "end": v(-45.56, -77.83) * mm});
            skLineSegment(sketch, "E722", {"start": v(-45.72, -78.23) * mm, "end": v(-45.63, -78.03) * mm});
            skLineSegment(sketch, "E723", {"start": v(-45.83, -78.43) * mm, "end": v(-45.72, -78.23) * mm});
            skLineSegment(sketch, "E724", {"start": v(-45.97, -78.64) * mm, "end": v(-45.83, -78.43) * mm});
            skLineSegment(sketch, "E725", {"start": v(-46.12, -78.83) * mm, "end": v(-45.97, -78.64) * mm});
            skLineSegment(sketch, "E726", {"start": v(-46.27, -78.99) * mm, "end": v(-46.12, -78.83) * mm});
            skLineSegment(sketch, "E727", {"start": v(-46.43, -79.11) * mm, "end": v(-46.27, -78.99) * mm});
            skLineSegment(sketch, "E728", {"start": v(-46.6, -79.21) * mm, "end": v(-46.43, -79.11) * mm});
            skLineSegment(sketch, "E729", {"start": v(-46.76, -79.3) * mm, "end": v(-46.6, -79.21) * mm});
            skLineSegment(sketch, "E730", {"start": v(-46.93, -79.34) * mm, "end": v(-46.76, -79.3) * mm});
            skLineSegment(sketch, "E731", {"start": v(-47.12, -79.37) * mm, "end": v(-46.93, -79.34) * mm});
            skLineSegment(sketch, "E732", {"start": v(-47.32, -79.38) * mm, "end": v(-47.12, -79.37) * mm});
            skLineSegment(sketch, "E733", {"start": v(-47.52, -79.35) * mm, "end": v(-47.32, -79.38) * mm});
            skLineSegment(sketch, "E734", {"start": v(-47.72, -79.3) * mm, "end": v(-47.52, -79.35) * mm});
            skLineSegment(sketch, "E735", {"start": v(-47.93, -79.23) * mm, "end": v(-47.72, -79.3) * mm});
            skLineSegment(sketch, "E736", {"start": v(-48.14, -79.13) * mm, "end": v(-47.93, -79.23) * mm});
            skLineSegment(sketch, "E737", {"start": v(-48.36, -79) * mm, "end": v(-48.14, -79.13) * mm});
            skLineSegment(sketch, "E738", {"start": v(-48.36, -79) * mm, "end": v(-48.9, -78.68) * mm});
            skLineSegment(sketch, "E739", {"start": v(-91, -1.86) * mm, "end": v(-90.97, -2.36) * mm});
            skLineSegment(sketch, "E740", {"start": v(-90.97, -2.36) * mm, "end": v(-91.27, -2.37) * mm});
            skLineSegment(sketch, "E741", {"start": v(-91.4, -2.36) * mm, "end": v(-91.27, -2.37) * mm});
            skLineSegment(sketch, "E742", {"start": v(-91.52, -2.35) * mm, "end": v(-91.4, -2.36) * mm});
            skLineSegment(sketch, "E743", {"start": v(-91.64, -2.32) * mm, "end": v(-91.52, -2.35) * mm});
            skLineSegment(sketch, "E744", {"start": v(-91.74, -2.28) * mm, "end": v(-91.64, -2.32) * mm});
            skLineSegment(sketch, "E745", {"start": v(-91.83, -2.23) * mm, "end": v(-91.74, -2.28) * mm});
            skLineSegment(sketch, "E746", {"start": v(-91.92, -2.17) * mm, "end": v(-91.83, -2.23) * mm});
            skLineSegment(sketch, "E747", {"start": v(-92, -2.1) * mm, "end": v(-91.92, -2.17) * mm});
            skLineSegment(sketch, "E748", {"start": v(-92.07, -2.02) * mm, "end": v(-92, -2.1) * mm});
            skLineSegment(sketch, "E749", {"start": v(-92.13, -1.93) * mm, "end": v(-92.07, -2.02) * mm});
            skLineSegment(sketch, "E750", {"start": v(-92.18, -1.83) * mm, "end": v(-92.13, -1.93) * mm});
            skLineSegment(sketch, "E751", {"start": v(-92.21, -1.73) * mm, "end": v(-92.18, -1.83) * mm});
            skLineSegment(sketch, "E752", {"start": v(-92.24, -1.61) * mm, "end": v(-92.21, -1.73) * mm});
            skLineSegment(sketch, "E753", {"start": v(-92.26, -1.5) * mm, "end": v(-92.24, -1.61) * mm});
            skLineSegment(sketch, "E754", {"start": v(-92.26, -1.36) * mm, "end": v(-92.26, -1.5) * mm});
            skLineSegment(sketch, "E755", {"start": v(-92.26, -1.28) * mm, "end": v(-92.26, -1.36) * mm});
            skLineSegment(sketch, "E756", {"start": v(-92.25, -1.2) * mm, "end": v(-92.26, -1.28) * mm});
            skLineSegment(sketch, "E757", {"start": v(-92.24, -1.13) * mm, "end": v(-92.25, -1.2) * mm});
            skLineSegment(sketch, "E758", {"start": v(-92.21, -1.04) * mm, "end": v(-92.24, -1.13) * mm});
            skLineSegment(sketch, "E759", {"start": v(-92.17, -0.97) * mm, "end": v(-92.21, -1.04) * mm});
            skLineSegment(sketch, "E760", {"start": v(-92.13, -0.9) * mm, "end": v(-92.17, -0.97) * mm});
            skLineSegment(sketch, "E761", {"start": v(-92.08, -0.85) * mm, "end": v(-92.13, -0.9) * mm});
            skLineSegment(sketch, "E762", {"start": v(-92.03, -0.81) * mm, "end": v(-92.08, -0.85) * mm});
            skLineSegment(sketch, "E763", {"start": v(-91.98, -0.78) * mm, "end": v(-92.03, -0.81) * mm});
            skLineSegment(sketch, "E764", {"start": v(-91.9, -0.75) * mm, "end": v(-91.98, -0.78) * mm});
            skLineSegment(sketch, "E765", {"start": v(-91.8, -0.73) * mm, "end": v(-91.9, -0.75) * mm});
            skLineSegment(sketch, "E766", {"start": v(-91.71, -0.73) * mm, "end": v(-91.8, -0.73) * mm});
            skLineSegment(sketch, "E767", {"start": v(-91.61, -0.73) * mm, "end": v(-91.71, -0.73) * mm});
            skLineSegment(sketch, "E768", {"start": v(-91.52, -0.75) * mm, "end": v(-91.61, -0.73) * mm});
            skLineSegment(sketch, "E769", {"start": v(-91.44, -0.78) * mm, "end": v(-91.52, -0.75) * mm});
            skLineSegment(sketch, "E770", {"start": v(-91.37, -0.81) * mm, "end": v(-91.44, -0.78) * mm});
            skLineSegment(sketch, "E771", {"start": v(-91.3, -0.86) * mm, "end": v(-91.37, -0.81) * mm});
            skLineSegment(sketch, "E772", {"start": v(-91.24, -0.92) * mm, "end": v(-91.3, -0.86) * mm});
            skLineSegment(sketch, "E773", {"start": v(-91.2, -0.99) * mm, "end": v(-91.24, -0.92) * mm});
            skLineSegment(sketch, "E774", {"start": v(-91.14, -1.07) * mm, "end": v(-91.2, -0.99) * mm});
            skLineSegment(sketch, "E775", {"start": v(-91.1, -1.17) * mm, "end": v(-91.14, -1.07) * mm});
            skLineSegment(sketch, "E776", {"start": v(-91.07, -1.29) * mm, "end": v(-91.1, -1.17) * mm});
            skLineSegment(sketch, "E777", {"start": v(-91.04, -1.4) * mm, "end": v(-91.07, -1.29) * mm});
            skLineSegment(sketch, "E778", {"start": v(-91.02, -1.54) * mm, "end": v(-91.04, -1.4) * mm});
            skLineSegment(sketch, "E779", {"start": v(-91, -1.7) * mm, "end": v(-91.02, -1.54) * mm});
            skLineSegment(sketch, "E780", {"start": v(-91, -1.86) * mm, "end": v(-91, -1.7) * mm});
            skLineSegment(sketch, "E781", {"start": v(-92.2, 2.97) * mm, "end": v(-92.2, 2.82) * mm});
            skLineSegment(sketch, "E782", {"start": v(-92.17, 3.1) * mm, "end": v(-92.2, 2.97) * mm});
            skLineSegment(sketch, "E783", {"start": v(-92.13, 3.22) * mm, "end": v(-92.17, 3.1) * mm});
            skLineSegment(sketch, "E784", {"start": v(-92.08, 3.32) * mm, "end": v(-92.13, 3.22) * mm});
            skLineSegment(sketch, "E785", {"start": v(-92.02, 3.41) * mm, "end": v(-92.08, 3.32) * mm});
            skLineSegment(sketch, "E786", {"start": v(-91.95, 3.5) * mm, "end": v(-92.02, 3.41) * mm});
            skLineSegment(sketch, "E787", {"start": v(-91.87, 3.56) * mm, "end": v(-91.95, 3.5) * mm});
            skLineSegment(sketch, "E788", {"start": v(-91.77, 3.62) * mm, "end": v(-91.87, 3.56) * mm});
            skLineSegment(sketch, "E789", {"start": v(-91.66, 3.67) * mm, "end": v(-91.77, 3.62) * mm});
            skLineSegment(sketch, "E790", {"start": v(-91.52, 3.71) * mm, "end": v(-91.66, 3.67) * mm});
            skLineSegment(sketch, "E791", {"start": v(-91.38, 3.74) * mm, "end": v(-91.52, 3.71) * mm});
            skLineSegment(sketch, "E792", {"start": v(-91.22, 3.75) * mm, "end": v(-91.38, 3.74) * mm});
            skLineSegment(sketch, "E793", {"start": v(-91.05, 3.76) * mm, "end": v(-91.22, 3.75) * mm});
            skLineSegment(sketch, "E794", {"start": v(-90.86, 3.76) * mm, "end": v(-91.05, 3.76) * mm});
            skLineSegment(sketch, "E795", {"start": v(-90.86, 3.76) * mm, "end": v(-90.74, 3.76) * mm});
            skLineSegment(sketch, "E796", {"start": v(-90.57, 3.74) * mm, "end": v(-90.74, 3.76) * mm});
            skLineSegment(sketch, "E797", {"start": v(-90.41, 3.72) * mm, "end": v(-90.57, 3.74) * mm});
            skLineSegment(sketch, "E798", {"start": v(-90.27, 3.69) * mm, "end": v(-90.41, 3.72) * mm});
            skLineSegment(sketch, "E799", {"start": v(-90.14, 3.65) * mm, "end": v(-90.27, 3.69) * mm});
            skLineSegment(sketch, "E800", {"start": v(-90.03, 3.6) * mm, "end": v(-90.14, 3.65) * mm});
            skLineSegment(sketch, "E801", {"start": v(-89.93, 3.55) * mm, "end": v(-90.03, 3.6) * mm});
            skLineSegment(sketch, "E802", {"start": v(-92.13, -2.38) * mm, "end": v(-92.13, -2.4) * mm});
            skLineSegment(sketch, "E803", {"start": v(-92.13, -2.4) * mm, "end": v(-92.6, -2.51) * mm});
            skLineSegment(sketch, "E804", {"start": v(-92.6, -2.51) * mm, "end": v(-92.6, -2.89) * mm});
            skLineSegment(sketch, "E805", {"start": v(-92.6, -2.89) * mm, "end": v(-90.32, -2.86) * mm});
            skLineSegment(sketch, "E806", {"start": v(-89.87, -2.8) * mm, "end": v(-90.32, -2.86) * mm});
            skLineSegment(sketch, "E807", {"start": v(-89.47, -2.56) * mm, "end": v(-89.87, -2.8) * mm});
            skLineSegment(sketch, "E808", {"start": v(-89.3, -2.25) * mm, "end": v(-89.47, -2.56) * mm});
            skLineSegment(sketch, "E809", {"start": v(-89.22, -1.67) * mm, "end": v(-89.3, -2.25) * mm});
            skLineSegment(sketch, "E810", {"start": v(-89.18, 2.93) * mm, "end": v(-89.17, 2.65) * mm});
            skLineSegment(sketch, "E811", {"start": v(-89.27, 3.25) * mm, "end": v(-89.18, 2.93) * mm});
            skLineSegment(sketch, "E812", {"start": v(-89.4, 3.47) * mm, "end": v(-89.27, 3.25) * mm});
            skLineSegment(sketch, "E813", {"start": v(-89.65, 3.72) * mm, "end": v(-89.4, 3.47) * mm});
            skLineSegment(sketch, "E814", {"start": v(-89.65, 3.72) * mm, "end": v(-89.65, 3.74) * mm});
            skLineSegment(sketch, "E815", {"start": v(-89.65, 3.74) * mm, "end": v(-89.19, 3.8) * mm});
            skLineSegment(sketch, "E816", {"start": v(-89.19, 3.8) * mm, "end": v(-89.17, 4.2) * mm});
            skLineSegment(sketch, "E817", {"start": v(-89.17, 4.2) * mm, "end": v(-94.01, 4.38) * mm});
            skLineSegment(sketch, "E818", {"start": v(-94.01, 4.38) * mm, "end": v(-94.03, 3.88) * mm});
            skLineSegment(sketch, "E819", {"start": v(-94.03, 3.88) * mm, "end": v(-92.66, 3.83) * mm});
            skLineSegment(sketch, "E820", {"start": v(-92.42, 3.82) * mm, "end": v(-92.66, 3.83) * mm});
            skLineSegment(sketch, "E821", {"start": v(-92.1, 3.84) * mm, "end": v(-92.42, 3.82) * mm});
            skLineSegment(sketch, "E822", {"start": v(-92.1, 3.84) * mm, "end": v(-92.1, 3.8) * mm});
            skLineSegment(sketch, "E823", {"start": v(-92.3, 3.63) * mm, "end": v(-92.1, 3.8) * mm});
            skLineSegment(sketch, "E824", {"start": v(-92.49, 3.37) * mm, "end": v(-92.3, 3.63) * mm});
            skLineSegment(sketch, "E825", {"start": v(-92.58, 3.12) * mm, "end": v(-92.49, 3.37) * mm});
            skLineSegment(sketch, "E826", {"start": v(-92.63, 2.77) * mm, "end": v(-92.58, 3.12) * mm});
            skLineSegment(sketch, "E827", {"start": v(-92.56, 2.25) * mm, "end": v(-92.63, 2.77) * mm});
            skLineSegment(sketch, "E828", {"start": v(-92.21, 1.74) * mm, "end": v(-92.56, 2.25) * mm});
            skLineSegment(sketch, "E829", {"start": v(-91.75, 1.47) * mm, "end": v(-92.21, 1.74) * mm});
            skLineSegment(sketch, "E830", {"start": v(-90.95, 1.32) * mm, "end": v(-91.75, 1.47) * mm});
            skLineSegment(sketch, "E831", {"start": v(-90.3, 1.37) * mm, "end": v(-90.95, 1.32) * mm});
            skLineSegment(sketch, "E832", {"start": v(-89.66, 1.64) * mm, "end": v(-90.3, 1.37) * mm});
            skLineSegment(sketch, "E833", {"start": v(-89.33, 2) * mm, "end": v(-89.66, 1.64) * mm});
            skLineSegment(sketch, "E834", {"start": v(-89.17, 2.65) * mm, "end": v(-89.33, 2) * mm});
            skLineSegment(sketch, "E835", {"start": v(-88.88, 7.6) * mm, "end": v(-88.88, 7.31) * mm});
            skLineSegment(sketch, "E836", {"start": v(-88.95, 7.91) * mm, "end": v(-88.88, 7.6) * mm});
            skLineSegment(sketch, "E837", {"start": v(-89.07, 8.14) * mm, "end": v(-88.95, 7.91) * mm});
            skLineSegment(sketch, "E838", {"start": v(-89.3, 8.4) * mm, "end": v(-89.07, 8.14) * mm});
            skLineSegment(sketch, "E839", {"start": v(-89.3, 8.4) * mm, "end": v(-89.3, 8.43) * mm});
            skLineSegment(sketch, "E840", {"start": v(-89.3, 8.43) * mm, "end": v(-88.84, 8.46) * mm});
            skLineSegment(sketch, "E841", {"start": v(-88.84, 8.46) * mm, "end": v(-88.8, 8.87) * mm});
            skLineSegment(sketch, "E842", {"start": v(-88.8, 8.87) * mm, "end": v(-93.63, 9.3) * mm});
            skLineSegment(sketch, "E843", {"start": v(-93.63, 9.3) * mm, "end": v(-93.67, 8.8) * mm});
            skLineSegment(sketch, "E844", {"start": v(-93.67, 8.8) * mm, "end": v(-92.3, 8.67) * mm});
            skLineSegment(sketch, "E845", {"start": v(-92.07, 8.65) * mm, "end": v(-92.3, 8.67) * mm});
            skLineSegment(sketch, "E846", {"start": v(-91.75, 8.66) * mm, "end": v(-92.07, 8.65) * mm});
            skLineSegment(sketch, "E847", {"start": v(-91.75, 8.66) * mm, "end": v(-91.75, 8.62) * mm});
            skLineSegment(sketch, "E848", {"start": v(-91.96, 8.46) * mm, "end": v(-91.75, 8.62) * mm});
            skLineSegment(sketch, "E849", {"start": v(-92.16, 8.2) * mm, "end": v(-91.96, 8.46) * mm});
            skLineSegment(sketch, "E850", {"start": v(-92.27, 7.96) * mm, "end": v(-92.16, 8.2) * mm});
            skLineSegment(sketch, "E851", {"start": v(-92.33, 7.62) * mm, "end": v(-92.27, 7.96) * mm});
            skLineSegment(sketch, "E852", {"start": v(-92.3, 7.1) * mm, "end": v(-92.33, 7.62) * mm});
            skLineSegment(sketch, "E853", {"start": v(-91.97, 6.56) * mm, "end": v(-92.3, 7.1) * mm});
            skLineSegment(sketch, "E854", {"start": v(-91.52, 6.27) * mm, "end": v(-91.97, 6.56) * mm});
            skLineSegment(sketch, "E855", {"start": v(-90.73, 6.08) * mm, "end": v(-91.52, 6.27) * mm});
            skLineSegment(sketch, "E856", {"start": v(-90.07, 6.1) * mm, "end": v(-90.73, 6.08) * mm});
            skLineSegment(sketch, "E857", {"start": v(-89.42, 6.33) * mm, "end": v(-90.07, 6.1) * mm});
            skLineSegment(sketch, "E858", {"start": v(-89.08, 6.68) * mm, "end": v(-89.42, 6.33) * mm});
            skLineSegment(sketch, "E859", {"start": v(-88.88, 7.31) * mm, "end": v(-89.08, 6.68) * mm});
            skLineSegment(sketch, "E860", {"start": v(-88.37, 11.95) * mm, "end": v(-88.4, 11.7) * mm});
            skLineSegment(sketch, "E861", {"start": v(-88.39, 12.29) * mm, "end": v(-88.37, 11.95) * mm});
            skLineSegment(sketch, "E862", {"start": v(-88.43, 12.55) * mm, "end": v(-88.39, 12.29) * mm});
            skLineSegment(sketch, "E863", {"start": v(-88.52, 12.85) * mm, "end": v(-88.43, 12.55) * mm});
            skLineSegment(sketch, "E864", {"start": v(-88.52, 12.85) * mm, "end": v(-88.93, 12.75) * mm});
            skLineSegment(sketch, "E865", {"start": v(-88.81, 12.29) * mm, "end": v(-88.93, 12.75) * mm});
            skLineSegment(sketch, "E866", {"start": v(-88.8, 11.78) * mm, "end": v(-88.81, 12.29) * mm});
            skLineSegment(sketch, "E867", {"start": v(-88.88, 11.5) * mm, "end": v(-88.8, 11.78) * mm});
            skLineSegment(sketch, "E868", {"start": v(-89.06, 11.27) * mm, "end": v(-88.88, 11.5) * mm});
            skLineSegment(sketch, "E869", {"start": v(-89.28, 11.18) * mm, "end": v(-89.06, 11.27) * mm});
            skLineSegment(sketch, "E870", {"start": v(-89.66, 11.18) * mm, "end": v(-89.28, 11.18) * mm});
            skLineSegment(sketch, "E871", {"start": v(-89.66, 11.18) * mm, "end": v(-89.87, 11.2) * mm});
            skLineSegment(sketch, "E872", {"start": v(-89.87, 11.2) * mm, "end": v(-89.8, 11.77) * mm});
            skLineSegment(sketch, "E873", {"start": v(-89.88, 12.9) * mm, "end": v(-89.8, 11.77) * mm});
            skLineSegment(sketch, "E874", {"start": v(-90.64, 13.52) * mm, "end": v(-89.88, 12.9) * mm});
            skLineSegment(sketch, "E875", {"start": v(-91.02, 13.52) * mm, "end": v(-90.64, 13.52) * mm});
            skLineSegment(sketch, "E876", {"start": v(-91.4, 13.34) * mm, "end": v(-91.02, 13.52) * mm});
            skLineSegment(sketch, "E877", {"start": v(-91.61, 13.08) * mm, "end": v(-91.4, 13.34) * mm});
            skLineSegment(sketch, "E878", {"start": v(-91.76, 12.6) * mm, "end": v(-91.61, 13.08) * mm});
            skLineSegment(sketch, "E879", {"start": v(-91.78, 12.3) * mm, "end": v(-91.76, 12.6) * mm});
            skLineSegment(sketch, "E880", {"start": v(-91.74, 11.98) * mm, "end": v(-91.78, 12.3) * mm});
            skLineSegment(sketch, "E881", {"start": v(-91.63, 11.74) * mm, "end": v(-91.74, 11.98) * mm});
            skLineSegment(sketch, "E882", {"start": v(-91.38, 11.43) * mm, "end": v(-91.63, 11.74) * mm});
            skLineSegment(sketch, "E883", {"start": v(-91.38, 11.43) * mm, "end": v(-91.38, 11.4) * mm});
            skLineSegment(sketch, "E884", {"start": v(-91.38, 11.4) * mm, "end": v(-91.87, 11.37) * mm});
            skLineSegment(sketch, "E885", {"start": v(-91.87, 11.37) * mm, "end": v(-91.92, 11) * mm});
            skLineSegment(sketch, "E886", {"start": v(-91.92, 11) * mm, "end": v(-89.66, 10.68) * mm});
            skLineSegment(sketch, "E887", {"start": v(-89.2, 10.67) * mm, "end": v(-89.66, 10.68) * mm});
            skLineSegment(sketch, "E888", {"start": v(-88.78, 10.85) * mm, "end": v(-89.2, 10.67) * mm});
            skLineSegment(sketch, "E889", {"start": v(-88.56, 11.14) * mm, "end": v(-88.78, 10.85) * mm});
            skLineSegment(sketch, "E890", {"start": v(-88.4, 11.7) * mm, "end": v(-88.56, 11.14) * mm});
            skLineSegment(sketch, "E891", {"start": v(-87.67, 16.24) * mm, "end": v(-87.7, 15.96) * mm});
            skLineSegment(sketch, "E892", {"start": v(-87.7, 16.57) * mm, "end": v(-87.67, 16.24) * mm});
            skLineSegment(sketch, "E893", {"start": v(-87.8, 16.8) * mm, "end": v(-87.7, 16.57) * mm});
            skLineSegment(sketch, "E894", {"start": v(-88.01, 17.09) * mm, "end": v(-87.8, 16.8) * mm});
            skLineSegment(sketch, "E895", {"start": v(-88.01, 17.09) * mm, "end": v(-88, 17.11) * mm});
            skLineSegment(sketch, "E896", {"start": v(-88, 17.11) * mm, "end": v(-87.54, 17.1) * mm});
            skLineSegment(sketch, "E897", {"start": v(-87.54, 17.1) * mm, "end": v(-87.47, 17.5) * mm});
            skLineSegment(sketch, "E898", {"start": v(-87.47, 17.5) * mm, "end": v(-92.23, 18.4) * mm});
            skLineSegment(sketch, "E899", {"start": v(-92.23, 18.4) * mm, "end": v(-92.32, 17.9) * mm});
            skLineSegment(sketch, "E900", {"start": v(-92.32, 17.9) * mm, "end": v(-90.97, 17.65) * mm});
            skLineSegment(sketch, "E901", {"start": v(-90.73, 17.61) * mm, "end": v(-90.97, 17.65) * mm});
            skLineSegment(sketch, "E902", {"start": v(-90.42, 17.58) * mm, "end": v(-90.73, 17.61) * mm});
            skLineSegment(sketch, "E903", {"start": v(-90.42, 17.58) * mm, "end": v(-90.42, 17.54) * mm});
            skLineSegment(sketch, "E904", {"start": v(-90.65, 17.4) * mm, "end": v(-90.42, 17.54) * mm});
            skLineSegment(sketch, "E905", {"start": v(-90.87, 17.17) * mm, "end": v(-90.65, 17.4) * mm});
            skLineSegment(sketch, "E906", {"start": v(-91, 16.94) * mm, "end": v(-90.87, 17.17) * mm});
            skLineSegment(sketch, "E907", {"start": v(-91.1, 16.6) * mm, "end": v(-91, 16.94) * mm});
            skLineSegment(sketch, "E908", {"start": v(-91.11, 16.08) * mm, "end": v(-91.1, 16.6) * mm});
            skLineSegment(sketch, "E909", {"start": v(-90.84, 15.52) * mm, "end": v(-91.11, 16.08) * mm});
            skLineSegment(sketch, "E910", {"start": v(-90.42, 15.18) * mm, "end": v(-90.84, 15.52) * mm});
            skLineSegment(sketch, "E911", {"start": v(-89.65, 14.92) * mm, "end": v(-90.42, 15.18) * mm});
            skLineSegment(sketch, "E912", {"start": v(-89, 14.87) * mm, "end": v(-89.65, 14.92) * mm});
            skLineSegment(sketch, "E913", {"start": v(-88.33, 15.04) * mm, "end": v(-89, 14.87) * mm});
            skLineSegment(sketch, "E914", {"start": v(-87.96, 15.35) * mm, "end": v(-88.33, 15.04) * mm});
            skLineSegment(sketch, "E915", {"start": v(-87.7, 15.96) * mm, "end": v(-87.96, 15.35) * mm});
            skLineSegment(sketch, "E916", {"start": v(-86.04, 23.29) * mm, "end": v(-86.1, 22.99) * mm});
            skLineSegment(sketch, "E917", {"start": v(-86.06, 23.65) * mm, "end": v(-86.04, 23.29) * mm});
            skLineSegment(sketch, "E918", {"start": v(-86.15, 23.9) * mm, "end": v(-86.06, 23.65) * mm});
            skLineSegment(sketch, "E919", {"start": v(-86.34, 24.18) * mm, "end": v(-86.15, 23.9) * mm});
            skLineSegment(sketch, "E920", {"start": v(-86.34, 24.18) * mm, "end": v(-86.33, 24.2) * mm});
            skLineSegment(sketch, "E921", {"start": v(-85.87, 24.4) * mm, "end": v(-86.33, 24.2) * mm});
            skLineSegment(sketch, "E922", {"start": v(-85.5, 25.03) * mm, "end": v(-85.87, 24.4) * mm});
            skLineSegment(sketch, "E923", {"start": v(-85.45, 25.3) * mm, "end": v(-85.5, 25.03) * mm});
            skLineSegment(sketch, "E924", {"start": v(-85.47, 25.63) * mm, "end": v(-85.45, 25.3) * mm});
            skLineSegment(sketch, "E925", {"start": v(-85.55, 25.87) * mm, "end": v(-85.47, 25.63) * mm});
            skLineSegment(sketch, "E926", {"start": v(-85.73, 26.13) * mm, "end": v(-85.55, 25.87) * mm});
            skLineSegment(sketch, "E927", {"start": v(-85.73, 26.13) * mm, "end": v(-85.72, 26.15) * mm});
            skLineSegment(sketch, "E928", {"start": v(-85.72, 26.15) * mm, "end": v(-85.26, 26.1) * mm});
            skLineSegment(sketch, "E929", {"start": v(-85.26, 26.1) * mm, "end": v(-85.15, 26.5) * mm});
            skLineSegment(sketch, "E930", {"start": v(-85.15, 26.5) * mm, "end": v(-88.36, 27.42) * mm});
            skLineSegment(sketch, "E931", {"start": v(-88.36, 27.42) * mm, "end": v(-88.5, 26.94) * mm});
            skLineSegment(sketch, "E932", {"start": v(-88.5, 26.94) * mm, "end": v(-86.81, 26.45) * mm});
            skLineSegment(sketch, "E933", {"start": v(-86.34, 26.27) * mm, "end": v(-86.81, 26.45) * mm});
            skLineSegment(sketch, "E934", {"start": v(-85.98, 25.98) * mm, "end": v(-86.34, 26.27) * mm});
            skLineSegment(sketch, "E935", {"start": v(-85.86, 25.7) * mm, "end": v(-85.98, 25.98) * mm});
            skLineSegment(sketch, "E936", {"start": v(-85.9, 25.23) * mm, "end": v(-85.86, 25.7) * mm});
            skLineSegment(sketch, "E937", {"start": v(-86.01, 24.97) * mm, "end": v(-85.9, 25.23) * mm});
            skLineSegment(sketch, "E938", {"start": v(-86.23, 24.77) * mm, "end": v(-86.01, 24.97) * mm});
            skLineSegment(sketch, "E939", {"start": v(-86.47, 24.72) * mm, "end": v(-86.23, 24.77) * mm});
            skLineSegment(sketch, "E940", {"start": v(-86.86, 24.78) * mm, "end": v(-86.47, 24.72) * mm});
            skLineSegment(sketch, "E941", {"start": v(-86.86, 24.78) * mm, "end": v(-88.95, 25.38) * mm});
            skLineSegment(sketch, "E942", {"start": v(-88.95, 25.38) * mm, "end": v(-89.09, 24.9) * mm});
            skLineSegment(sketch, "E943", {"start": v(-89.09, 24.9) * mm, "end": v(-87.3, 24.37) * mm});
            skLineSegment(sketch, "E944", {"start": v(-86.88, 24.2) * mm, "end": v(-87.3, 24.37) * mm});
            skLineSegment(sketch, "E945", {"start": v(-86.55, 23.93) * mm, "end": v(-86.88, 24.2) * mm});
            skLineSegment(sketch, "E946", {"start": v(-86.44, 23.64) * mm, "end": v(-86.55, 23.93) * mm});
            skLineSegment(sketch, "E947", {"start": v(-86.49, 23.18) * mm, "end": v(-86.44, 23.64) * mm});
            skLineSegment(sketch, "E948", {"start": v(-86.6, 22.92) * mm, "end": v(-86.49, 23.18) * mm});
            skLineSegment(sketch, "E949", {"start": v(-86.83, 22.72) * mm, "end": v(-86.6, 22.92) * mm});
            skLineSegment(sketch, "E950", {"start": v(-87.06, 22.67) * mm, "end": v(-86.83, 22.72) * mm});
            skLineSegment(sketch, "E951", {"start": v(-87.45, 22.73) * mm, "end": v(-87.06, 22.67) * mm});
            skLineSegment(sketch, "E952", {"start": v(-87.45, 22.73) * mm, "end": v(-89.54, 23.33) * mm});
            skLineSegment(sketch, "E953", {"start": v(-89.54, 23.33) * mm, "end": v(-89.68, 22.84) * mm});
            skLineSegment(sketch, "E954", {"start": v(-89.68, 22.84) * mm, "end": v(-87.58, 22.24) * mm});
            skLineSegment(sketch, "E955", {"start": v(-87.1, 22.15) * mm, "end": v(-87.58, 22.24) * mm});
            skLineSegment(sketch, "E956", {"start": v(-86.6, 22.25) * mm, "end": v(-87.1, 22.15) * mm});
            skLineSegment(sketch, "E957", {"start": v(-86.33, 22.49) * mm, "end": v(-86.6, 22.25) * mm});
            skLineSegment(sketch, "E958", {"start": v(-86.1, 22.99) * mm, "end": v(-86.33, 22.49) * mm});
            skLineSegment(sketch, "E959", {"start": v(-85.5, 31.88) * mm, "end": v(-85.06, 31.76) * mm});
            skLineSegment(sketch, "E960", {"start": v(-86, 31.9) * mm, "end": v(-85.5, 31.88) * mm});
            skLineSegment(sketch, "E961", {"start": v(-86.36, 31.82) * mm, "end": v(-86, 31.9) * mm});
            skLineSegment(sketch, "E962", {"start": v(-86.75, 31.6) * mm, "end": v(-86.36, 31.82) * mm});
            skLineSegment(sketch, "E963", {"start": v(-87, 31.34) * mm, "end": v(-86.75, 31.6) * mm});
            skLineSegment(sketch, "E964", {"start": v(-87.21, 30.92) * mm, "end": v(-87, 31.34) * mm});
            skLineSegment(sketch, "E965", {"start": v(-87.33, 30.34) * mm, "end": v(-87.21, 30.92) * mm});
            skLineSegment(sketch, "E966", {"start": v(-87.17, 29.7) * mm, "end": v(-87.33, 30.34) * mm});
            skLineSegment(sketch, "E967", {"start": v(-86.82, 29.27) * mm, "end": v(-87.17, 29.7) * mm});
            skLineSegment(sketch, "E968", {"start": v(-86.1, 28.87) * mm, "end": v(-86.82, 29.27) * mm});
            skLineSegment(sketch, "E969", {"start": v(-85.48, 28.73) * mm, "end": v(-86.1, 28.87) * mm});
            skLineSegment(sketch, "E970", {"start": v(-84.78, 28.84) * mm, "end": v(-85.48, 28.73) * mm});
            skLineSegment(sketch, "E971", {"start": v(-84.33, 29.12) * mm, "end": v(-84.78, 28.84) * mm});
            skLineSegment(sketch, "E972", {"start": v(-83.96, 29.73) * mm, "end": v(-84.33, 29.12) * mm});
            skLineSegment(sketch, "E973", {"start": v(-83.85, 30.3) * mm, "end": v(-83.96, 29.73) * mm});
            skLineSegment(sketch, "E974", {"start": v(-84, 30.95) * mm, "end": v(-83.85, 30.3) * mm});
            skLineSegment(sketch, "E975", {"start": v(-84.35, 31.37) * mm, "end": v(-84, 30.95) * mm});
            skLineSegment(sketch, "E976", {"start": v(-85.06, 31.76) * mm, "end": v(-84.35, 31.37) * mm});
            skLineSegment(sketch, "E977", {"start": v(-78.25, 42.47) * mm, "end": v(-78.37, 42.2) * mm});
            skLineSegment(sketch, "E978", {"start": v(-78.18, 42.81) * mm, "end": v(-78.25, 42.47) * mm});
            skLineSegment(sketch, "E979", {"start": v(-78.2, 43.08) * mm, "end": v(-78.18, 42.81) * mm});
            skLineSegment(sketch, "E980", {"start": v(-78.31, 43.38) * mm, "end": v(-78.2, 43.08) * mm});
            skLineSegment(sketch, "E981", {"start": v(-78.31, 43.38) * mm, "end": v(-78.3, 43.4) * mm});
            skLineSegment(sketch, "E982", {"start": v(-78.3, 43.4) * mm, "end": v(-77.86, 43.25) * mm});
            skLineSegment(sketch, "E983", {"start": v(-77.86, 43.25) * mm, "end": v(-77.66, 43.62) * mm});
            skLineSegment(sketch, "E984", {"start": v(-77.66, 43.62) * mm, "end": v(-80.6, 45.22) * mm});
            skLineSegment(sketch, "E985", {"start": v(-80.6, 45.22) * mm, "end": v(-80.84, 44.78) * mm});
            skLineSegment(sketch, "E986", {"start": v(-80.84, 44.78) * mm, "end": v(-79.3, 43.93) * mm});
            skLineSegment(sketch, "E987", {"start": v(-78.88, 43.65) * mm, "end": v(-79.3, 43.93) * mm});
            skLineSegment(sketch, "E988", {"start": v(-78.6, 43.27) * mm, "end": v(-78.88, 43.65) * mm});
            skLineSegment(sketch, "E989", {"start": v(-78.55, 42.94) * mm, "end": v(-78.6, 43.27) * mm});
            skLineSegment(sketch, "E990", {"start": v(-78.71, 42.46) * mm, "end": v(-78.55, 42.94) * mm});
            skLineSegment(sketch, "E991", {"start": v(-78.9, 42.2) * mm, "end": v(-78.71, 42.46) * mm});
            skLineSegment(sketch, "E992", {"start": v(-79.17, 42.05) * mm, "end": v(-78.9, 42.2) * mm});
            skLineSegment(sketch, "E993", {"start": v(-79.42, 42.04) * mm, "end": v(-79.17, 42.05) * mm});
            skLineSegment(sketch, "E994", {"start": v(-79.8, 42.18) * mm, "end": v(-79.42, 42.04) * mm});
            skLineSegment(sketch, "E995", {"start": v(-79.8, 42.18) * mm, "end": v(-81.7, 43.21) * mm});
            skLineSegment(sketch, "E996", {"start": v(-81.7, 43.21) * mm, "end": v(-81.94, 42.77) * mm});
            skLineSegment(sketch, "E997", {"start": v(-81.94, 42.77) * mm, "end": v(-80.02, 41.72) * mm});
            skLineSegment(sketch, "E998", {"start": v(-79.56, 41.54) * mm, "end": v(-80.02, 41.72) * mm});
            skLineSegment(sketch, "E999", {"start": v(-79.06, 41.54) * mm, "end": v(-79.56, 41.54) * mm});
            skLineSegment(sketch, "E1000", {"start": v(-78.73, 41.73) * mm, "end": v(-79.06, 41.54) * mm});
            skLineSegment(sketch, "E1001", {"start": v(-78.37, 42.2) * mm, "end": v(-78.73, 41.73) * mm});
            skLineSegment(sketch, "E1002", {"start": v(-77, 48.8) * mm, "end": v(-76.61, 48.6) * mm});
            skLineSegment(sketch, "E1003", {"start": v(-77.5, 48.92) * mm, "end": v(-77, 48.8) * mm});
            skLineSegment(sketch, "E1004", {"start": v(-77.86, 48.91) * mm, "end": v(-77.5, 48.92) * mm});
            skLineSegment(sketch, "E1005", {"start": v(-78.3, 48.78) * mm, "end": v(-77.86, 48.91) * mm});
            skLineSegment(sketch, "E1006", {"start": v(-78.58, 48.58) * mm, "end": v(-78.3, 48.78) * mm});
            skLineSegment(sketch, "E1007", {"start": v(-78.89, 48.2) * mm, "end": v(-78.58, 48.58) * mm});
            skLineSegment(sketch, "E1008", {"start": v(-79.12, 47.67) * mm, "end": v(-78.89, 48.2) * mm});
            skLineSegment(sketch, "E1009", {"start": v(-79.1, 47) * mm, "end": v(-79.12, 47.67) * mm});
            skLineSegment(sketch, "E1010", {"start": v(-78.84, 46.51) * mm, "end": v(-79.1, 47) * mm});
            skLineSegment(sketch, "E1011", {"start": v(-78.22, 45.98) * mm, "end": v(-78.84, 46.51) * mm});
            skLineSegment(sketch, "E1012", {"start": v(-58.96, 67.15) * mm, "end": v(-58.64, 67.37) * mm});
            skLineSegment(sketch, "E1013", {"start": v(-58.64, 67.37) * mm, "end": v(-58.4, 67.62) * mm});
            skLineSegment(sketch, "E1014", {"start": v(-58.4, 67.62) * mm, "end": v(-58.3, 67.81) * mm});
            skLineSegment(sketch, "E1015", {"start": v(-58.3, 67.81) * mm, "end": v(-58.3, 68.02) * mm});
            skLineSegment(sketch, "E1016", {"start": v(-58.3, 68.02) * mm, "end": v(-58.37, 68.17) * mm});
            skLineSegment(sketch, "E1017", {"start": v(-58.37, 68.17) * mm, "end": v(-58.48, 68.26) * mm});
            skLineSegment(sketch, "E1018", {"start": v(-58.48, 68.26) * mm, "end": v(-58.57, 68.3) * mm});
            skLineSegment(sketch, "E1019", {"start": v(-46.13, 74.96) * mm, "end": v(-46.2, 75.11) * mm});
            skLineSegment(sketch, "E1020", {"start": v(-46.2, 75.11) * mm, "end": v(-46.2, 75.22) * mm});
            skLineSegment(sketch, "E1021", {"start": v(-46.2, 75.22) * mm, "end": v(-46.13, 75.34) * mm});
            skLineSegment(sketch, "E1022", {"start": v(-46.13, 75.34) * mm, "end": v(-46.05, 75.4) * mm});
            skLineSegment(sketch, "E1023", {"start": v(-46.05, 75.4) * mm, "end": v(-45.93, 75.45) * mm});
            skLineSegment(sketch, "E1024", {"start": v(-45.93, 75.45) * mm, "end": v(-45.83, 75.44) * mm});
            skLineSegment(sketch, "E1025", {"start": v(-45.83, 75.44) * mm, "end": v(-45.7, 75.37) * mm});
            skLineSegment(sketch, "E1026", {"start": v(-45.7, 75.37) * mm, "end": v(-45.62, 75.27) * mm});
            skLineSegment(sketch, "E1027", {"start": v(-45.62, 75.27) * mm, "end": v(-45.56, 75.11) * mm});
            skLineSegment(sketch, "E1028", {"start": v(-45.56, 75.11) * mm, "end": v(-45.56, 75) * mm});
            skLineSegment(sketch, "E1029", {"start": v(-45.56, 75) * mm, "end": v(-45.62, 74.9) * mm});
            skLineSegment(sketch, "E1030", {"start": v(-45.62, 74.9) * mm, "end": v(-45.7, 74.83) * mm});
            skLineSegment(sketch, "E1031", {"start": v(-45.7, 74.83) * mm, "end": v(-45.83, 74.78) * mm});
            skLineSegment(sketch, "E1032", {"start": v(-45.83, 74.78) * mm, "end": v(-45.93, 74.79) * mm});
            skLineSegment(sketch, "E1033", {"start": v(-45.93, 74.79) * mm, "end": v(-46.05, 74.85) * mm});
            skLineSegment(sketch, "E1034", {"start": v(-46.05, 74.85) * mm, "end": v(-46.13, 74.96) * mm});
            skLineSegment(sketch, "E1035", {"start": v(-49.15, 74.04) * mm, "end": v(-49.68, 73.8) * mm});
            skLineSegment(sketch, "E1036", {"start": v(-49.68, 73.8) * mm, "end": v(-50.07, 73.78) * mm});
            skLineSegment(sketch, "E1037", {"start": v(-50.07, 73.78) * mm, "end": v(-50.51, 74.01) * mm});
            skLineSegment(sketch, "E1038", {"start": v(-50.51, 74.01) * mm, "end": v(-50.83, 74.4) * mm});
            skLineSegment(sketch, "E1039", {"start": v(-52.03, 76.22) * mm, "end": v(-50.83, 74.4) * mm});
            skLineSegment(sketch, "E1040", {"start": v(-51.6, 76.5) * mm, "end": v(-52.03, 76.22) * mm});
            skLineSegment(sketch, "E1041", {"start": v(-50.42, 74.7) * mm, "end": v(-51.6, 76.5) * mm});
            skLineSegment(sketch, "E1042", {"start": v(-50.42, 74.7) * mm, "end": v(-50.16, 74.4) * mm});
            skLineSegment(sketch, "E1043", {"start": v(-50.16, 74.4) * mm, "end": v(-49.93, 74.28) * mm});
            skLineSegment(sketch, "E1044", {"start": v(-49.93, 74.28) * mm, "end": v(-49.61, 74.3) * mm});
            skLineSegment(sketch, "E1045", {"start": v(-49.61, 74.3) * mm, "end": v(-49.33, 74.43) * mm});
            skLineSegment(sketch, "E1046", {"start": v(-49.33, 74.43) * mm, "end": v(-48.96, 74.78) * mm});
            skLineSegment(sketch, "E1047", {"start": v(-48.96, 74.78) * mm, "end": v(-48.85, 75.1) * mm});
            skLineSegment(sketch, "E1048", {"start": v(-48.85, 75.1) * mm, "end": v(-48.92, 75.56) * mm});
            skLineSegment(sketch, "E1049", {"start": v(-48.92, 75.56) * mm, "end": v(-49.16, 76) * mm});
            skLineSegment(sketch, "E1050", {"start": v(-50.12, 77.48) * mm, "end": v(-49.16, 76) * mm});
            skLineSegment(sketch, "E1051", {"start": v(-49.7, 77.75) * mm, "end": v(-50.12, 77.48) * mm});
            skLineSegment(sketch, "E1052", {"start": v(-47.86, 74.96) * mm, "end": v(-49.7, 77.75) * mm});
            skLineSegment(sketch, "E1053", {"start": v(-48.2, 74.73) * mm, "end": v(-47.86, 74.96) * mm});
            skLineSegment(sketch, "E1054", {"start": v(-48.52, 75.07) * mm, "end": v(-48.2, 74.73) * mm});
            skLineSegment(sketch, "E1055", {"start": v(-48.54, 75.06) * mm, "end": v(-48.52, 75.07) * mm});
            skLineSegment(sketch, "E1056", {"start": v(-48.54, 75.06) * mm, "end": v(-48.59, 74.74) * mm});
            skLineSegment(sketch, "E1057", {"start": v(-48.59, 74.74) * mm, "end": v(-48.7, 74.5) * mm});
            skLineSegment(sketch, "E1058", {"start": v(-48.7, 74.5) * mm, "end": v(-48.92, 74.22) * mm});
            skLineSegment(sketch, "E1059", {"start": v(-48.92, 74.22) * mm, "end": v(-49.15, 74.04) * mm});
            skLineSegment(sketch, "E1060", {"start": v(-73.04, 56.62) * mm, "end": v(-72.6, 57.03) * mm});
            skLineSegment(sketch, "E1061", {"start": v(-72.6, 57.03) * mm, "end": v(-72.25, 57.16) * mm});
            skLineSegment(sketch, "E1062", {"start": v(-72.25, 57.16) * mm, "end": v(-71.76, 57.1) * mm});
            skLineSegment(sketch, "E1063", {"start": v(-71.76, 57.1) * mm, "end": v(-71.33, 56.83) * mm});
            skLineSegment(sketch, "E1064", {"start": v(-69.6, 55.49) * mm, "end": v(-71.33, 56.83) * mm});
            skLineSegment(sketch, "E1065", {"start": v(-69.92, 55.09) * mm, "end": v(-69.6, 55.49) * mm});
            skLineSegment(sketch, "E1066", {"start": v(-71.63, 56.42) * mm, "end": v(-69.92, 55.09) * mm});
            skLineSegment(sketch, "E1067", {"start": v(-71.63, 56.42) * mm, "end": v(-71.98, 56.61) * mm});
            skLineSegment(sketch, "E1068", {"start": v(-71.98, 56.61) * mm, "end": v(-72.23, 56.65) * mm});
            skLineSegment(sketch, "E1069", {"start": v(-72.23, 56.65) * mm, "end": v(-72.52, 56.53) * mm});
            skLineSegment(sketch, "E1070", {"start": v(-72.52, 56.53) * mm, "end": v(-72.74, 56.3) * mm});
            skLineSegment(sketch, "E1071", {"start": v(-72.74, 56.3) * mm, "end": v(-72.98, 55.86) * mm});
            skLineSegment(sketch, "E1072", {"start": v(-72.98, 55.86) * mm, "end": v(-72.99, 55.53) * mm});
            skLineSegment(sketch, "E1073", {"start": v(-72.99, 55.53) * mm, "end": v(-72.76, 55.1) * mm});
            skLineSegment(sketch, "E1074", {"start": v(-72.76, 55.1) * mm, "end": v(-72.4, 54.76) * mm});
            skLineSegment(sketch, "E1075", {"start": v(-71.01, 53.68) * mm, "end": v(-72.4, 54.76) * mm});
            skLineSegment(sketch, "E1076", {"start": v(-71.32, 53.28) * mm, "end": v(-71.01, 53.68) * mm});
            skLineSegment(sketch, "E1077", {"start": v(-73.96, 55.34) * mm, "end": v(-71.32, 53.28) * mm});
            skLineSegment(sketch, "E1078", {"start": v(-73.7, 55.67) * mm, "end": v(-73.96, 55.34) * mm});
            skLineSegment(sketch, "E1079", {"start": v(-73.3, 55.45) * mm, "end": v(-73.7, 55.67) * mm});
            skLineSegment(sketch, "E1080", {"start": v(-73.29, 55.47) * mm, "end": v(-73.3, 55.45) * mm});
            skLineSegment(sketch, "E1081", {"start": v(-73.29, 55.47) * mm, "end": v(-73.35, 55.79) * mm});
            skLineSegment(sketch, "E1082", {"start": v(-73.35, 55.79) * mm, "end": v(-73.32, 56.04) * mm});
            skLineSegment(sketch, "E1083", {"start": v(-73.32, 56.04) * mm, "end": v(-73.2, 56.37) * mm});
            skLineSegment(sketch, "E1084", {"start": v(-73.2, 56.37) * mm, "end": v(-73.04, 56.62) * mm});
            skLineSegment(sketch, "E1085", {"start": v(-73.72, 48.3) * mm, "end": v(-73.84, 48.41) * mm});
            skLineSegment(sketch, "E1086", {"start": v(-73.84, 48.41) * mm, "end": v(-73.88, 48.51) * mm});
            skLineSegment(sketch, "E1087", {"start": v(-73.88, 48.51) * mm, "end": v(-73.88, 48.64) * mm});
            skLineSegment(sketch, "E1088", {"start": v(-73.88, 48.64) * mm, "end": v(-73.83, 48.74) * mm});
            skLineSegment(sketch, "E1089", {"start": v(-73.83, 48.74) * mm, "end": v(-73.74, 48.83) * mm});
            skLineSegment(sketch, "E1090", {"start": v(-73.74, 48.83) * mm, "end": v(-73.64, 48.87) * mm});
            skLineSegment(sketch, "E1091", {"start": v(-73.64, 48.87) * mm, "end": v(-73.5, 48.86) * mm});
            skLineSegment(sketch, "E1092", {"start": v(-73.5, 48.86) * mm, "end": v(-73.38, 48.8) * mm});
            skLineSegment(sketch, "E1093", {"start": v(-73.38, 48.8) * mm, "end": v(-73.26, 48.68) * mm});
            skLineSegment(sketch, "E1094", {"start": v(-73.26, 48.68) * mm, "end": v(-73.22, 48.59) * mm});
            skLineSegment(sketch, "E1095", {"start": v(-73.22, 48.59) * mm, "end": v(-73.23, 48.46) * mm});
            skLineSegment(sketch, "E1096", {"start": v(-73.23, 48.46) * mm, "end": v(-73.27, 48.36) * mm});
            skLineSegment(sketch, "E1097", {"start": v(-73.27, 48.36) * mm, "end": v(-73.36, 48.27) * mm});
            skLineSegment(sketch, "E1098", {"start": v(-73.36, 48.27) * mm, "end": v(-73.46, 48.23) * mm});
            skLineSegment(sketch, "E1099", {"start": v(-73.46, 48.23) * mm, "end": v(-73.6, 48.24) * mm});
            skLineSegment(sketch, "E1100", {"start": v(-73.6, 48.24) * mm, "end": v(-73.72, 48.3) * mm});
            skLineSegment(sketch, "E1101", {"start": v(-76.61, 48.6) * mm, "end": v(-76, 48.06) * mm});
            skLineSegment(sketch, "E1102", {"start": v(-76, 48.06) * mm, "end": v(-75.74, 47.58) * mm});
            skLineSegment(sketch, "E1103", {"start": v(-75.74, 47.58) * mm, "end": v(-75.72, 46.91) * mm});
            skLineSegment(sketch, "E1104", {"start": v(-75.72, 46.91) * mm, "end": v(-75.95, 46.37) * mm});
            skLineSegment(sketch, "E1105", {"start": v(-75.95, 46.37) * mm, "end": v(-76.44, 45.86) * mm});
            skLineSegment(sketch, "E1106", {"start": v(-76.44, 45.86) * mm, "end": v(-76.93, 45.67) * mm});
            skLineSegment(sketch, "E1107", {"start": v(-76.93, 45.67) * mm, "end": v(-77.64, 45.71) * mm});
            skLineSegment(sketch, "E1108", {"start": v(-77.64, 45.71) * mm, "end": v(-78.22, 45.98) * mm});
            skLineSegment(sketch, "E1109", {"start": v(-92.13, -2.38) * mm, "end": v(-92.43, -2.1) * mm});
            skLineSegment(sketch, "E1110", {"start": v(-92.43, -2.1) * mm, "end": v(-92.57, -1.89) * mm});
            skLineSegment(sketch, "E1111", {"start": v(-92.57, -1.89) * mm, "end": v(-92.66, -1.57) * mm});
            skLineSegment(sketch, "E1112", {"start": v(-92.66, -1.57) * mm, "end": v(-92.68, -1.27) * mm});
            skLineSegment(sketch, "E1113", {"start": v(-92.68, -1.27) * mm, "end": v(-92.61, -0.78) * mm});
            skLineSegment(sketch, "E1114", {"start": v(-92.61, -0.78) * mm, "end": v(-92.44, -0.49) * mm});
            skLineSegment(sketch, "E1115", {"start": v(-86.88, 30.27) * mm, "end": v(-86.86, 30.16) * mm});
            skLineSegment(sketch, "E1116", {"start": v(-86.86, 30.16) * mm, "end": v(-86.82, 30.05) * mm});
            skLineSegment(sketch, "E1117", {"start": v(-86.82, 30.05) * mm, "end": v(-86.76, 29.94) * mm});
            skLineSegment(sketch, "E1118", {"start": v(-86.76, 29.94) * mm, "end": v(-86.69, 29.84) * mm});
            skLineSegment(sketch, "E1119", {"start": v(-86.69, 29.84) * mm, "end": v(-86.6, 29.75) * mm});
            skLineSegment(sketch, "E1120", {"start": v(-86.6, 29.75) * mm, "end": v(-86.5, 29.67) * mm});
            skLineSegment(sketch, "E1121", {"start": v(-86.5, 29.67) * mm, "end": v(-86.39, 29.58) * mm});
            skLineSegment(sketch, "E1122", {"start": v(-86.39, 29.58) * mm, "end": v(-86.25, 29.5) * mm});
            skLineSegment(sketch, "E1123", {"start": v(-86.25, 29.5) * mm, "end": v(-86.1, 29.43) * mm});
            skLineSegment(sketch, "E1124", {"start": v(-86.1, 29.43) * mm, "end": v(-85.93, 29.37) * mm});
            skLineSegment(sketch, "E1125", {"start": v(-90.67, 16.59) * mm, "end": v(-90.69, 16.47) * mm});
            skLineSegment(sketch, "E1126", {"start": v(-90.69, 16.47) * mm, "end": v(-90.69, 16.36) * mm});
            skLineSegment(sketch, "E1127", {"start": v(-90.69, 16.36) * mm, "end": v(-90.67, 16.25) * mm});
            skLineSegment(sketch, "E1128", {"start": v(-90.67, 16.25) * mm, "end": v(-90.64, 16.15) * mm});
            skLineSegment(sketch, "E1129", {"start": v(-90.64, 16.15) * mm, "end": v(-90.6, 16.04) * mm});
            skLineSegment(sketch, "E1130", {"start": v(-90.6, 16.04) * mm, "end": v(-90.53, 15.95) * mm});
            skLineSegment(sketch, "E1131", {"start": v(-90.53, 15.95) * mm, "end": v(-90.45, 15.85) * mm});
            skLineSegment(sketch, "E1132", {"start": v(-90.45, 15.85) * mm, "end": v(-90.33, 15.75) * mm});
            skLineSegment(sketch, "E1133", {"start": v(-90.33, 15.75) * mm, "end": v(-90.19, 15.65) * mm});
            skLineSegment(sketch, "E1134", {"start": v(-90.19, 15.65) * mm, "end": v(-90.02, 15.57) * mm});
            skLineSegment(sketch, "E1135", {"start": v(-90.02, 15.57) * mm, "end": v(-89.88, 15.52) * mm});
            skLineSegment(sketch, "E1136", {"start": v(-89.88, 15.52) * mm, "end": v(-89.72, 15.47) * mm});
            skLineSegment(sketch, "E1137", {"start": v(-89.72, 15.47) * mm, "end": v(-89.55, 15.43) * mm});
            skLineSegment(sketch, "E1138", {"start": v(-89.55, 15.43) * mm, "end": v(-89.33, 15.4) * mm});
            skLineSegment(sketch, "E1139", {"start": v(-89.33, 15.4) * mm, "end": v(-89.12, 15.39) * mm});
            skLineSegment(sketch, "E1140", {"start": v(-89.12, 15.39) * mm, "end": v(-88.94, 15.4) * mm});
            skLineSegment(sketch, "E1141", {"start": v(-88.94, 15.4) * mm, "end": v(-88.8, 15.42) * mm});
            skLineSegment(sketch, "E1142", {"start": v(-88.8, 15.42) * mm, "end": v(-88.68, 15.45) * mm});
            skLineSegment(sketch, "E1143", {"start": v(-88.68, 15.45) * mm, "end": v(-88.56, 15.5) * mm});
            skLineSegment(sketch, "E1144", {"start": v(-88.56, 15.5) * mm, "end": v(-88.46, 15.55) * mm});
            skLineSegment(sketch, "E1145", {"start": v(-88.46, 15.55) * mm, "end": v(-88.37, 15.62) * mm});
            skLineSegment(sketch, "E1146", {"start": v(-88.37, 15.62) * mm, "end": v(-88.3, 15.7) * mm});
            skLineSegment(sketch, "E1147", {"start": v(-88.3, 15.7) * mm, "end": v(-88.23, 15.78) * mm});
            skLineSegment(sketch, "E1148", {"start": v(-88.23, 15.78) * mm, "end": v(-88.18, 15.88) * mm});
            skLineSegment(sketch, "E1149", {"start": v(-88.18, 15.88) * mm, "end": v(-88.14, 16) * mm});
            skLineSegment(sketch, "E1150", {"start": v(-88.14, 16) * mm, "end": v(-88.1, 16.11) * mm});
            skLineSegment(sketch, "E1151", {"start": v(-88.1, 16.11) * mm, "end": v(-88.08, 16.25) * mm});
            skLineSegment(sketch, "E1152", {"start": v(-88.08, 16.25) * mm, "end": v(-88.08, 16.38) * mm});
            skLineSegment(sketch, "E1153", {"start": v(-88.08, 16.38) * mm, "end": v(-88.08, 16.5) * mm});
            skLineSegment(sketch, "E1154", {"start": v(-88.08, 16.5) * mm, "end": v(-88.1, 16.6) * mm});
            skLineSegment(sketch, "E1155", {"start": v(-88.1, 16.6) * mm, "end": v(-88.14, 16.71) * mm});
            skLineSegment(sketch, "E1156", {"start": v(-88.14, 16.71) * mm, "end": v(-88.18, 16.8) * mm});
            skLineSegment(sketch, "E1157", {"start": v(-88.18, 16.8) * mm, "end": v(-88.25, 16.9) * mm});
            skLineSegment(sketch, "E1158", {"start": v(-88.25, 16.9) * mm, "end": v(-88.32, 16.97) * mm});
            skLineSegment(sketch, "E1159", {"start": v(-88.32, 16.97) * mm, "end": v(-88.4, 17.04) * mm});
            skLineSegment(sketch, "E1160", {"start": v(-88.4, 17.04) * mm, "end": v(-88.5, 17.1) * mm});
            skLineSegment(sketch, "E1161", {"start": v(-88.5, 17.1) * mm, "end": v(-88.63, 17.16) * mm});
            skLineSegment(sketch, "E1162", {"start": v(-88.63, 17.16) * mm, "end": v(-88.77, 17.2) * mm});
            skLineSegment(sketch, "E1163", {"start": v(-88.77, 17.2) * mm, "end": v(-88.92, 17.25) * mm});
            skLineSegment(sketch, "E1164", {"start": v(-88.92, 17.25) * mm, "end": v(-89.09, 17.3) * mm});
            skLineSegment(sketch, "E1165", {"start": v(-89.2, 17.31) * mm, "end": v(-89.09, 17.3) * mm});
            skLineSegment(sketch, "E1166", {"start": v(-89.2, 17.31) * mm, "end": v(-89.39, 17.34) * mm});
            skLineSegment(sketch, "E1167", {"start": v(-89.39, 17.34) * mm, "end": v(-89.56, 17.36) * mm});
            skLineSegment(sketch, "E1168", {"start": v(-89.56, 17.36) * mm, "end": v(-89.72, 17.37) * mm});
            skLineSegment(sketch, "E1169", {"start": v(-89.72, 17.37) * mm, "end": v(-89.87, 17.36) * mm});
            skLineSegment(sketch, "E1170", {"start": v(-89.87, 17.36) * mm, "end": v(-90, 17.35) * mm});
            skLineSegment(sketch, "E1171", {"start": v(-90, 17.35) * mm, "end": v(-90.13, 17.31) * mm});
            skLineSegment(sketch, "E1172", {"start": v(-90.13, 17.31) * mm, "end": v(-90.23, 17.27) * mm});
            skLineSegment(sketch, "E1173", {"start": v(-90.23, 17.27) * mm, "end": v(-90.33, 17.21) * mm});
            skLineSegment(sketch, "E1174", {"start": v(-90.33, 17.21) * mm, "end": v(-90.4, 17.15) * mm});
            skLineSegment(sketch, "E1175", {"start": v(-90.4, 17.15) * mm, "end": v(-90.48, 17.06) * mm});
            skLineSegment(sketch, "E1176", {"start": v(-90.48, 17.06) * mm, "end": v(-90.54, 16.97) * mm});
            skLineSegment(sketch, "E1177", {"start": v(-90.54, 16.97) * mm, "end": v(-90.6, 16.86) * mm});
            skLineSegment(sketch, "E1178", {"start": v(-90.6, 16.86) * mm, "end": v(-90.64, 16.73) * mm});
            skLineSegment(sketch, "E1179", {"start": v(-90.64, 16.73) * mm, "end": v(-90.67, 16.59) * mm});
            skLineSegment(sketch, "E1180", {"start": v(-90.17, 11.78) * mm, "end": v(-90.16, 11.94) * mm});
            skLineSegment(sketch, "E1181", {"start": v(-90.16, 11.94) * mm, "end": v(-90.16, 12.09) * mm});
            skLineSegment(sketch, "E1182", {"start": v(-90.16, 12.09) * mm, "end": v(-90.16, 12.23) * mm});
            skLineSegment(sketch, "E1183", {"start": v(-90.16, 12.23) * mm, "end": v(-90.17, 12.35) * mm});
            skLineSegment(sketch, "E1184", {"start": v(-90.17, 12.35) * mm, "end": v(-90.18, 12.47) * mm});
            skLineSegment(sketch, "E1185", {"start": v(-90.18, 12.47) * mm, "end": v(-90.2, 12.57) * mm});
            skLineSegment(sketch, "E1186", {"start": v(-90.2, 12.57) * mm, "end": v(-90.24, 12.66) * mm});
            skLineSegment(sketch, "E1187", {"start": v(-90.24, 12.66) * mm, "end": v(-90.28, 12.74) * mm});
            skLineSegment(sketch, "E1188", {"start": v(-90.28, 12.74) * mm, "end": v(-90.33, 12.8) * mm});
            skLineSegment(sketch, "E1189", {"start": v(-90.33, 12.8) * mm, "end": v(-90.39, 12.86) * mm});
            skLineSegment(sketch, "E1190", {"start": v(-90.39, 12.86) * mm, "end": v(-90.45, 12.91) * mm});
            skLineSegment(sketch, "E1191", {"start": v(-90.45, 12.91) * mm, "end": v(-90.53, 12.95) * mm});
            skLineSegment(sketch, "E1192", {"start": v(-90.53, 12.95) * mm, "end": v(-90.62, 12.98) * mm});
            skLineSegment(sketch, "E1193", {"start": v(-90.62, 12.98) * mm, "end": v(-90.72, 13) * mm});
            skLineSegment(sketch, "E1194", {"start": v(-90.72, 13) * mm, "end": v(-90.82, 13) * mm});
            skLineSegment(sketch, "E1195", {"start": v(-90.82, 13) * mm, "end": v(-90.9, 13) * mm});
            skLineSegment(sketch, "E1196", {"start": v(-90.9, 13) * mm, "end": v(-90.99, 12.98) * mm});
            skLineSegment(sketch, "E1197", {"start": v(-90.99, 12.98) * mm, "end": v(-91.05, 12.96) * mm});
            skLineSegment(sketch, "E1198", {"start": v(-91.05, 12.96) * mm, "end": v(-91.1, 12.93) * mm});
            skLineSegment(sketch, "E1199", {"start": v(-91.1, 12.93) * mm, "end": v(-91.15, 12.9) * mm});
            skLineSegment(sketch, "E1200", {"start": v(-91.15, 12.9) * mm, "end": v(-91.21, 12.83) * mm});
            skLineSegment(sketch, "E1201", {"start": v(-91.21, 12.83) * mm, "end": v(-91.26, 12.76) * mm});
            skLineSegment(sketch, "E1202", {"start": v(-91.26, 12.76) * mm, "end": v(-91.3, 12.68) * mm});
            skLineSegment(sketch, "E1203", {"start": v(-91.3, 12.68) * mm, "end": v(-91.32, 12.61) * mm});
            skLineSegment(sketch, "E1204", {"start": v(-91.32, 12.61) * mm, "end": v(-91.34, 12.53) * mm});
            skLineSegment(sketch, "E1205", {"start": v(-91.34, 12.53) * mm, "end": v(-91.36, 12.45) * mm});
            skLineSegment(sketch, "E1206", {"start": v(-91.36, 12.45) * mm, "end": v(-91.37, 12.32) * mm});
            skLineSegment(sketch, "E1207", {"start": v(-91.37, 12.32) * mm, "end": v(-91.37, 12.2) * mm});
            skLineSegment(sketch, "E1208", {"start": v(-91.37, 12.2) * mm, "end": v(-91.36, 12.09) * mm});
            skLineSegment(sketch, "E1209", {"start": v(-91.36, 12.09) * mm, "end": v(-91.34, 11.98) * mm});
            skLineSegment(sketch, "E1210", {"start": v(-91.34, 11.98) * mm, "end": v(-91.3, 11.87) * mm});
            skLineSegment(sketch, "E1211", {"start": v(-91.3, 11.87) * mm, "end": v(-91.26, 11.77) * mm});
            skLineSegment(sketch, "E1212", {"start": v(-91.26, 11.77) * mm, "end": v(-91.2, 11.68) * mm});
            skLineSegment(sketch, "E1213", {"start": v(-91.2, 11.68) * mm, "end": v(-91.14, 11.6) * mm});
            skLineSegment(sketch, "E1214", {"start": v(-91.14, 11.6) * mm, "end": v(-91.06, 11.53) * mm});
            skLineSegment(sketch, "E1215", {"start": v(-91.06, 11.53) * mm, "end": v(-90.98, 11.47) * mm});
            skLineSegment(sketch, "E1216", {"start": v(-90.98, 11.47) * mm, "end": v(-90.88, 11.41) * mm});
            skLineSegment(sketch, "E1217", {"start": v(-91.03, 8.51) * mm, "end": v(-91.18, 8.5) * mm});
            skLineSegment(sketch, "E1218", {"start": v(-91.18, 8.5) * mm, "end": v(-91.31, 8.46) * mm});
            skLineSegment(sketch, "E1219", {"start": v(-91.31, 8.46) * mm, "end": v(-91.43, 8.42) * mm});
            skLineSegment(sketch, "E1220", {"start": v(-91.43, 8.42) * mm, "end": v(-91.54, 8.36) * mm});
            skLineSegment(sketch, "E1221", {"start": v(-91.54, 8.36) * mm, "end": v(-91.62, 8.3) * mm});
            skLineSegment(sketch, "E1222", {"start": v(-91.62, 8.3) * mm, "end": v(-91.7, 8.22) * mm});
            skLineSegment(sketch, "E1223", {"start": v(-91.7, 8.22) * mm, "end": v(-91.76, 8.14) * mm});
            skLineSegment(sketch, "E1224", {"start": v(-91.76, 8.14) * mm, "end": v(-91.81, 8.04) * mm});
            skLineSegment(sketch, "E1225", {"start": v(-91.81, 8.04) * mm, "end": v(-91.85, 7.92) * mm});
            skLineSegment(sketch, "E1226", {"start": v(-91.85, 7.92) * mm, "end": v(-91.89, 7.79) * mm});
            skLineSegment(sketch, "E1227", {"start": v(-91.89, 7.79) * mm, "end": v(-91.9, 7.64) * mm});
            skLineSegment(sketch, "E1228", {"start": v(-92.2, 2.82) * mm, "end": v(-92.2, 2.7) * mm});
            skLineSegment(sketch, "E1229", {"start": v(-92.2, 2.7) * mm, "end": v(-92.18, 2.6) * mm});
            skLineSegment(sketch, "E1230", {"start": v(-92.18, 2.6) * mm, "end": v(-92.15, 2.49) * mm});
            skLineSegment(sketch, "E1231", {"start": v(-92.15, 2.49) * mm, "end": v(-92.1, 2.4) * mm});
            skLineSegment(sketch, "E1232", {"start": v(-92.1, 2.4) * mm, "end": v(-92.05, 2.3) * mm});
            skLineSegment(sketch, "E1233", {"start": v(-92.05, 2.3) * mm, "end": v(-91.97, 2.2) * mm});
            skLineSegment(sketch, "E1234", {"start": v(-91.97, 2.2) * mm, "end": v(-91.88, 2.13) * mm});
            skLineSegment(sketch, "E1235", {"start": v(-91.88, 2.13) * mm, "end": v(-91.74, 2.04) * mm});
            skLineSegment(sketch, "E1236", {"start": v(-91.74, 2.04) * mm, "end": v(-91.58, 1.97) * mm});
            skLineSegment(sketch, "E1237", {"start": v(-91.58, 1.97) * mm, "end": v(-91.4, 1.91) * mm});
            skLineSegment(sketch, "E1238", {"start": v(-91.4, 1.91) * mm, "end": v(-91.26, 1.88) * mm});
            skLineSegment(sketch, "E1239", {"start": v(-91.26, 1.88) * mm, "end": v(-91.1, 1.86) * mm});
            skLineSegment(sketch, "E1240", {"start": v(-91.1, 1.86) * mm, "end": v(-90.92, 1.85) * mm});
            skLineSegment(sketch, "E1241", {"start": v(-89.63, 2.5) * mm, "end": v(-89.6, 2.61) * mm});
            skLineSegment(sketch, "E1242", {"start": v(-89.6, 2.61) * mm, "end": v(-89.6, 2.74) * mm});
            skLineSegment(sketch, "E1243", {"start": v(-89.6, 2.74) * mm, "end": v(-89.6, 2.87) * mm});
            skLineSegment(sketch, "E1244", {"start": v(-89.6, 2.87) * mm, "end": v(-89.6, 3) * mm});
            skLineSegment(sketch, "E1245", {"start": v(-89.6, 3) * mm, "end": v(-89.63, 3.12) * mm});
            skLineSegment(sketch, "E1246", {"start": v(-89.63, 3.12) * mm, "end": v(-89.66, 3.22) * mm});
            skLineSegment(sketch, "E1247", {"start": v(-89.85, 3.49) * mm, "end": v(-89.93, 3.55) * mm});
            skLineSegment(sketch, "E1248", {"start": v(-89.78, 3.41) * mm, "end": v(-89.85, 3.49) * mm});
            skLineSegment(sketch, "E1249", {"start": v(-89.71, 3.32) * mm, "end": v(-89.78, 3.41) * mm});
            skLineSegment(sketch, "E1250", {"start": v(-89.66, 3.22) * mm, "end": v(-89.71, 3.32) * mm});
            skLineSegment(sketch, "E1251", {"start": v(-89.67, 2.39) * mm, "end": v(-89.63, 2.5) * mm});
            skLineSegment(sketch, "E1252", {"start": v(-89.72, 2.3) * mm, "end": v(-89.67, 2.39) * mm});
            skLineSegment(sketch, "E1253", {"start": v(-89.79, 2.2) * mm, "end": v(-89.72, 2.3) * mm});
            skLineSegment(sketch, "E1254", {"start": v(-89.86, 2.13) * mm, "end": v(-89.79, 2.2) * mm});
            skLineSegment(sketch, "E1255", {"start": v(-89.95, 2.06) * mm, "end": v(-89.86, 2.13) * mm});
            skLineSegment(sketch, "E1256", {"start": v(-90.06, 2) * mm, "end": v(-89.95, 2.06) * mm});
            skLineSegment(sketch, "E1257", {"start": v(-90.18, 1.94) * mm, "end": v(-90.06, 2) * mm});
            skLineSegment(sketch, "E1258", {"start": v(-90.3, 1.9) * mm, "end": v(-90.18, 1.94) * mm});
            skLineSegment(sketch, "E1259", {"start": v(-90.45, 1.87) * mm, "end": v(-90.3, 1.9) * mm});
            skLineSegment(sketch, "E1260", {"start": v(-90.6, 1.86) * mm, "end": v(-90.45, 1.87) * mm});
            skLineSegment(sketch, "E1261", {"start": v(-90.75, 1.85) * mm, "end": v(-90.6, 1.86) * mm});
            skLineSegment(sketch, "E1262", {"start": v(-90.92, 1.85) * mm, "end": v(-90.75, 1.85) * mm});
            skLineSegment(sketch, "E1263", {"start": v(-90.87, 8.52) * mm, "end": v(-91.03, 8.51) * mm});
            skLineSegment(sketch, "E1264", {"start": v(-90.7, 8.52) * mm, "end": v(-90.87, 8.52) * mm});
            skLineSegment(sketch, "E1265", {"start": v(-90.51, 8.5) * mm, "end": v(-90.7, 8.52) * mm});
            skLineSegment(sketch, "E1266", {"start": v(-90.51, 8.5) * mm, "end": v(-90.4, 8.5) * mm});
            skLineSegment(sketch, "E1267", {"start": v(-90.23, 8.48) * mm, "end": v(-90.4, 8.5) * mm});
            skLineSegment(sketch, "E1268", {"start": v(-90.07, 8.45) * mm, "end": v(-90.23, 8.48) * mm});
            skLineSegment(sketch, "E1269", {"start": v(-89.92, 8.4) * mm, "end": v(-90.07, 8.45) * mm});
            skLineSegment(sketch, "E1270", {"start": v(-89.8, 8.36) * mm, "end": v(-89.92, 8.4) * mm});
            skLineSegment(sketch, "E1271", {"start": v(-89.7, 8.31) * mm, "end": v(-89.8, 8.36) * mm});
            skLineSegment(sketch, "E1272", {"start": v(-89.6, 8.25) * mm, "end": v(-89.7, 8.31) * mm});
            skLineSegment(sketch, "E1273", {"start": v(-89.52, 8.19) * mm, "end": v(-89.6, 8.25) * mm});
            skLineSegment(sketch, "E1274", {"start": v(-89.45, 8.1) * mm, "end": v(-89.52, 8.19) * mm});
            skLineSegment(sketch, "E1275", {"start": v(-89.4, 8.01) * mm, "end": v(-89.45, 8.1) * mm});
            skLineSegment(sketch, "E1276", {"start": v(-89.35, 7.91) * mm, "end": v(-89.4, 8.01) * mm});
            skLineSegment(sketch, "E1277", {"start": v(-89.32, 7.8) * mm, "end": v(-89.35, 7.91) * mm});
            skLineSegment(sketch, "E1278", {"start": v(-89.3, 7.69) * mm, "end": v(-89.32, 7.8) * mm});
            skLineSegment(sketch, "E1279", {"start": v(-89.3, 7.56) * mm, "end": v(-89.3, 7.69) * mm});
            skLineSegment(sketch, "E1280", {"start": v(-89.3, 7.42) * mm, "end": v(-89.3, 7.56) * mm});
            skLineSegment(sketch, "E1281", {"start": v(-89.32, 7.3) * mm, "end": v(-89.3, 7.42) * mm});
            skLineSegment(sketch, "E1282", {"start": v(-89.35, 7.18) * mm, "end": v(-89.32, 7.3) * mm});
            skLineSegment(sketch, "E1283", {"start": v(-89.4, 7.08) * mm, "end": v(-89.35, 7.18) * mm});
            skLineSegment(sketch, "E1284", {"start": v(-89.45, 6.98) * mm, "end": v(-89.4, 7.08) * mm});
            skLineSegment(sketch, "E1285", {"start": v(-89.52, 6.9) * mm, "end": v(-89.45, 6.98) * mm});
            skLineSegment(sketch, "E1286", {"start": v(-89.6, 6.83) * mm, "end": v(-89.52, 6.9) * mm});
            skLineSegment(sketch, "E1287", {"start": v(-89.7, 6.76) * mm, "end": v(-89.6, 6.83) * mm});
            skLineSegment(sketch, "E1288", {"start": v(-89.8, 6.7) * mm, "end": v(-89.7, 6.76) * mm});
            skLineSegment(sketch, "E1289", {"start": v(-89.93, 6.66) * mm, "end": v(-89.8, 6.7) * mm});
            skLineSegment(sketch, "E1290", {"start": v(-90.06, 6.63) * mm, "end": v(-89.93, 6.66) * mm});
            skLineSegment(sketch, "E1291", {"start": v(-90.2, 6.6) * mm, "end": v(-90.06, 6.63) * mm});
            skLineSegment(sketch, "E1292", {"start": v(-90.35, 6.6) * mm, "end": v(-90.2, 6.6) * mm});
            skLineSegment(sketch, "E1293", {"start": v(-90.5, 6.6) * mm, "end": v(-90.35, 6.6) * mm});
            skLineSegment(sketch, "E1294", {"start": v(-90.67, 6.6) * mm, "end": v(-90.5, 6.6) * mm});
            skLineSegment(sketch, "E1295", {"start": v(-90.85, 6.62) * mm, "end": v(-90.67, 6.6) * mm});
            skLineSegment(sketch, "E1296", {"start": v(-91, 6.65) * mm, "end": v(-90.85, 6.62) * mm});
            skLineSegment(sketch, "E1297", {"start": v(-91.16, 6.7) * mm, "end": v(-91, 6.65) * mm});
            skLineSegment(sketch, "E1298", {"start": v(-91.33, 6.76) * mm, "end": v(-91.16, 6.7) * mm});
            skLineSegment(sketch, "E1299", {"start": v(-91.48, 6.84) * mm, "end": v(-91.33, 6.76) * mm});
            skLineSegment(sketch, "E1300", {"start": v(-91.62, 6.93) * mm, "end": v(-91.48, 6.84) * mm});
            skLineSegment(sketch, "E1301", {"start": v(-91.7, 7.02) * mm, "end": v(-91.62, 6.93) * mm});
            skLineSegment(sketch, "E1302", {"start": v(-91.78, 7.1) * mm, "end": v(-91.7, 7.02) * mm});
            skLineSegment(sketch, "E1303", {"start": v(-91.83, 7.2) * mm, "end": v(-91.78, 7.1) * mm});
            skLineSegment(sketch, "E1304", {"start": v(-91.87, 7.3) * mm, "end": v(-91.83, 7.2) * mm});
            skLineSegment(sketch, "E1305", {"start": v(-91.9, 7.41) * mm, "end": v(-91.87, 7.3) * mm});
            skLineSegment(sketch, "E1306", {"start": v(-91.9, 7.52) * mm, "end": v(-91.9, 7.41) * mm});
            skLineSegment(sketch, "E1307", {"start": v(-91.9, 7.64) * mm, "end": v(-91.9, 7.52) * mm});
            skLineSegment(sketch, "E1308", {"start": v(-90.17, 11.78) * mm, "end": v(-90.22, 11.27) * mm});
            skLineSegment(sketch, "E1309", {"start": v(-90.22, 11.27) * mm, "end": v(-90.52, 11.31) * mm});
            skLineSegment(sketch, "E1310", {"start": v(-90.65, 11.34) * mm, "end": v(-90.52, 11.31) * mm});
            skLineSegment(sketch, "E1311", {"start": v(-90.77, 11.37) * mm, "end": v(-90.65, 11.34) * mm});
            skLineSegment(sketch, "E1312", {"start": v(-90.88, 11.41) * mm, "end": v(-90.77, 11.37) * mm});
            skLineSegment(sketch, "E1313", {"start": v(-86.9, 30.4) * mm, "end": v(-86.88, 30.27) * mm});
            skLineSegment(sketch, "E1314", {"start": v(-86.88, 30.51) * mm, "end": v(-86.9, 30.4) * mm});
            skLineSegment(sketch, "E1315", {"start": v(-86.86, 30.63) * mm, "end": v(-86.88, 30.51) * mm});
            skLineSegment(sketch, "E1316", {"start": v(-86.82, 30.76) * mm, "end": v(-86.86, 30.63) * mm});
            skLineSegment(sketch, "E1317", {"start": v(-86.76, 30.9) * mm, "end": v(-86.82, 30.76) * mm});
            skLineSegment(sketch, "E1318", {"start": v(-86.7, 31) * mm, "end": v(-86.76, 30.9) * mm});
            skLineSegment(sketch, "E1319", {"start": v(-86.63, 31.1) * mm, "end": v(-86.7, 31) * mm});
            skLineSegment(sketch, "E1320", {"start": v(-86.54, 31.2) * mm, "end": v(-86.63, 31.1) * mm});
            skLineSegment(sketch, "E1321", {"start": v(-86.46, 31.26) * mm, "end": v(-86.54, 31.2) * mm});
            skLineSegment(sketch, "E1322", {"start": v(-86.36, 31.32) * mm, "end": v(-86.46, 31.26) * mm});
            skLineSegment(sketch, "E1323", {"start": v(-86.25, 31.36) * mm, "end": v(-86.36, 31.32) * mm});
            skLineSegment(sketch, "E1324", {"start": v(-86.13, 31.39) * mm, "end": v(-86.25, 31.36) * mm});
            skLineSegment(sketch, "E1325", {"start": v(-86, 31.4) * mm, "end": v(-86.13, 31.39) * mm});
            skLineSegment(sketch, "E1326", {"start": v(-85.86, 31.4) * mm, "end": v(-86, 31.4) * mm});
            skLineSegment(sketch, "E1327", {"start": v(-85.71, 31.4) * mm, "end": v(-85.86, 31.4) * mm});
            skLineSegment(sketch, "E1328", {"start": v(-85.56, 31.36) * mm, "end": v(-85.71, 31.4) * mm});
            skLineSegment(sketch, "E1329", {"start": v(-85.4, 31.32) * mm, "end": v(-85.56, 31.36) * mm});
            skLineSegment(sketch, "E1330", {"start": v(-85.24, 31.27) * mm, "end": v(-85.4, 31.32) * mm});
            skLineSegment(sketch, "E1331", {"start": v(-85.07, 31.2) * mm, "end": v(-85.24, 31.27) * mm});
            skLineSegment(sketch, "E1332", {"start": v(-84.92, 31.13) * mm, "end": v(-85.07, 31.2) * mm});
            skLineSegment(sketch, "E1333", {"start": v(-84.78, 31.05) * mm, "end": v(-84.92, 31.13) * mm});
            skLineSegment(sketch, "E1334", {"start": v(-84.67, 30.97) * mm, "end": v(-84.78, 31.05) * mm});
            skLineSegment(sketch, "E1335", {"start": v(-84.57, 30.89) * mm, "end": v(-84.67, 30.97) * mm});
            skLineSegment(sketch, "E1336", {"start": v(-84.48, 30.8) * mm, "end": v(-84.57, 30.89) * mm});
            skLineSegment(sketch, "E1337", {"start": v(-84.41, 30.7) * mm, "end": v(-84.48, 30.8) * mm});
            skLineSegment(sketch, "E1338", {"start": v(-84.36, 30.6) * mm, "end": v(-84.41, 30.7) * mm});
            skLineSegment(sketch, "E1339", {"start": v(-84.32, 30.49) * mm, "end": v(-84.36, 30.6) * mm});
            skLineSegment(sketch, "E1340", {"start": v(-84.3, 30.37) * mm, "end": v(-84.32, 30.49) * mm});
            skLineSegment(sketch, "E1341", {"start": v(-84.29, 30.26) * mm, "end": v(-84.3, 30.37) * mm});
            skLineSegment(sketch, "E1342", {"start": v(-84.3, 30.14) * mm, "end": v(-84.29, 30.26) * mm});
            skLineSegment(sketch, "E1343", {"start": v(-84.32, 30.02) * mm, "end": v(-84.3, 30.14) * mm});
            skLineSegment(sketch, "E1344", {"start": v(-84.36, 29.89) * mm, "end": v(-84.32, 30.02) * mm});
            skLineSegment(sketch, "E1345", {"start": v(-84.41, 29.75) * mm, "end": v(-84.36, 29.89) * mm});
            skLineSegment(sketch, "E1346", {"start": v(-84.48, 29.64) * mm, "end": v(-84.41, 29.75) * mm});
            skLineSegment(sketch, "E1347", {"start": v(-84.55, 29.54) * mm, "end": v(-84.48, 29.64) * mm});
            skLineSegment(sketch, "E1348", {"start": v(-84.63, 29.45) * mm, "end": v(-84.55, 29.54) * mm});
            skLineSegment(sketch, "E1349", {"start": v(-84.72, 29.38) * mm, "end": v(-84.63, 29.45) * mm});
            skLineSegment(sketch, "E1350", {"start": v(-84.82, 29.33) * mm, "end": v(-84.72, 29.38) * mm});
            skLineSegment(sketch, "E1351", {"start": v(-84.93, 29.28) * mm, "end": v(-84.82, 29.33) * mm});
            skLineSegment(sketch, "E1352", {"start": v(-85.05, 29.25) * mm, "end": v(-84.93, 29.28) * mm});
            skLineSegment(sketch, "E1353", {"start": v(-85.18, 29.23) * mm, "end": v(-85.05, 29.25) * mm});
            skLineSegment(sketch, "E1354", {"start": v(-85.32, 29.23) * mm, "end": v(-85.18, 29.23) * mm});
            skLineSegment(sketch, "E1355", {"start": v(-85.46, 29.25) * mm, "end": v(-85.32, 29.23) * mm});
            skLineSegment(sketch, "E1356", {"start": v(-85.6, 29.27) * mm, "end": v(-85.46, 29.25) * mm});
            skLineSegment(sketch, "E1357", {"start": v(-85.76, 29.31) * mm, "end": v(-85.6, 29.27) * mm});
            skLineSegment(sketch, "E1358", {"start": v(-85.93, 29.37) * mm, "end": v(-85.76, 29.31) * mm});
            skLineSegment(sketch, "E1359", {"start": v(-78.1, 46.53) * mm, "end": v(-77.95, 46.43) * mm});
            skLineSegment(sketch, "E1360", {"start": v(-78.23, 46.63) * mm, "end": v(-78.1, 46.53) * mm});
            skLineSegment(sketch, "E1361", {"start": v(-78.35, 46.73) * mm, "end": v(-78.23, 46.63) * mm});
            skLineSegment(sketch, "E1362", {"start": v(-78.45, 46.84) * mm, "end": v(-78.35, 46.73) * mm});
            skLineSegment(sketch, "E1363", {"start": v(-78.53, 46.94) * mm, "end": v(-78.45, 46.84) * mm});
            skLineSegment(sketch, "E1364", {"start": v(-78.6, 47.05) * mm, "end": v(-78.53, 46.94) * mm});
            skLineSegment(sketch, "E1365", {"start": v(-78.64, 47.16) * mm, "end": v(-78.6, 47.05) * mm});
            skLineSegment(sketch, "E1366", {"start": v(-78.68, 47.27) * mm, "end": v(-78.64, 47.16) * mm});
            skLineSegment(sketch, "E1367", {"start": v(-78.7, 47.4) * mm, "end": v(-78.68, 47.27) * mm});
            skLineSegment(sketch, "E1368", {"start": v(-78.7, 47.51) * mm, "end": v(-78.7, 47.4) * mm});
            skLineSegment(sketch, "E1369", {"start": v(-78.68, 47.63) * mm, "end": v(-78.7, 47.51) * mm});
            skLineSegment(sketch, "E1370", {"start": v(-78.65, 47.74) * mm, "end": v(-78.68, 47.63) * mm});
            skLineSegment(sketch, "E1371", {"start": v(-78.6, 47.86) * mm, "end": v(-78.65, 47.74) * mm});
            skLineSegment(sketch, "E1372", {"start": v(-78.53, 47.98) * mm, "end": v(-78.6, 47.86) * mm});
            skLineSegment(sketch, "E1373", {"start": v(-78.45, 48.1) * mm, "end": v(-78.53, 47.98) * mm});
            skLineSegment(sketch, "E1374", {"start": v(-78.37, 48.2) * mm, "end": v(-78.45, 48.1) * mm});
            skLineSegment(sketch, "E1375", {"start": v(-78.27, 48.27) * mm, "end": v(-78.37, 48.2) * mm});
            skLineSegment(sketch, "E1376", {"start": v(-78.18, 48.34) * mm, "end": v(-78.27, 48.27) * mm});
            skLineSegment(sketch, "E1377", {"start": v(-78.07, 48.39) * mm, "end": v(-78.18, 48.34) * mm});
            skLineSegment(sketch, "E1378", {"start": v(-77.97, 48.42) * mm, "end": v(-78.07, 48.39) * mm});
            skLineSegment(sketch, "E1379", {"start": v(-77.85, 48.44) * mm, "end": v(-77.97, 48.42) * mm});
            skLineSegment(sketch, "E1380", {"start": v(-77.73, 48.45) * mm, "end": v(-77.85, 48.44) * mm});
            skLineSegment(sketch, "E1381", {"start": v(-77.6, 48.43) * mm, "end": v(-77.73, 48.45) * mm});
            skLineSegment(sketch, "E1382", {"start": v(-77.46, 48.4) * mm, "end": v(-77.6, 48.43) * mm});
            skLineSegment(sketch, "E1383", {"start": v(-77.28, 48.35) * mm, "end": v(-77.46, 48.4) * mm});
            skLineSegment(sketch, "E1384", {"start": v(-77.09, 48.26) * mm, "end": v(-77.28, 48.35) * mm});
            skLineSegment(sketch, "E1385", {"start": v(-76.89, 48.15) * mm, "end": v(-77.09, 48.26) * mm});
            skLineSegment(sketch, "E1386", {"start": v(-76.73, 48.05) * mm, "end": v(-76.89, 48.15) * mm});
            skLineSegment(sketch, "E1387", {"start": v(-76.6, 47.94) * mm, "end": v(-76.73, 48.05) * mm});
            skLineSegment(sketch, "E1388", {"start": v(-76.48, 47.84) * mm, "end": v(-76.6, 47.94) * mm});
            skLineSegment(sketch, "E1389", {"start": v(-76.38, 47.74) * mm, "end": v(-76.48, 47.84) * mm});
            skLineSegment(sketch, "E1390", {"start": v(-76.3, 47.63) * mm, "end": v(-76.38, 47.74) * mm});
            skLineSegment(sketch, "E1391", {"start": v(-76.24, 47.53) * mm, "end": v(-76.3, 47.63) * mm});
            skLineSegment(sketch, "E1392", {"start": v(-76.2, 47.42) * mm, "end": v(-76.24, 47.53) * mm});
            skLineSegment(sketch, "E1393", {"start": v(-76.16, 47.3) * mm, "end": v(-76.2, 47.42) * mm});
            skLineSegment(sketch, "E1394", {"start": v(-76.14, 47.2) * mm, "end": v(-76.16, 47.3) * mm});
            skLineSegment(sketch, "E1395", {"start": v(-76.14, 47.07) * mm, "end": v(-76.14, 47.2) * mm});
            skLineSegment(sketch, "E1396", {"start": v(-76.16, 46.96) * mm, "end": v(-76.14, 47.07) * mm});
            skLineSegment(sketch, "E1397", {"start": v(-76.2, 46.85) * mm, "end": v(-76.16, 46.96) * mm});
            skLineSegment(sketch, "E1398", {"start": v(-76.24, 46.73) * mm, "end": v(-76.2, 46.85) * mm});
            skLineSegment(sketch, "E1399", {"start": v(-76.3, 46.61) * mm, "end": v(-76.24, 46.73) * mm});
            skLineSegment(sketch, "E1400", {"start": v(-76.39, 46.5) * mm, "end": v(-76.3, 46.61) * mm});
            skLineSegment(sketch, "E1401", {"start": v(-76.47, 46.4) * mm, "end": v(-76.39, 46.5) * mm});
            skLineSegment(sketch, "E1402", {"start": v(-76.57, 46.3) * mm, "end": v(-76.47, 46.4) * mm});
            skLineSegment(sketch, "E1403", {"start": v(-76.66, 46.24) * mm, "end": v(-76.57, 46.3) * mm});
            skLineSegment(sketch, "E1404", {"start": v(-76.77, 46.2) * mm, "end": v(-76.66, 46.24) * mm});
            skLineSegment(sketch, "E1405", {"start": v(-76.87, 46.16) * mm, "end": v(-76.77, 46.2) * mm});
            skLineSegment(sketch, "E1406", {"start": v(-76.99, 46.14) * mm, "end": v(-76.87, 46.16) * mm});
            skLineSegment(sketch, "E1407", {"start": v(-77.11, 46.13) * mm, "end": v(-76.99, 46.14) * mm});
            skLineSegment(sketch, "E1408", {"start": v(-77.24, 46.14) * mm, "end": v(-77.11, 46.13) * mm});
            skLineSegment(sketch, "E1409", {"start": v(-77.38, 46.17) * mm, "end": v(-77.24, 46.14) * mm});
            skLineSegment(sketch, "E1410", {"start": v(-77.56, 46.23) * mm, "end": v(-77.38, 46.17) * mm});
            skLineSegment(sketch, "E1411", {"start": v(-77.75, 46.31) * mm, "end": v(-77.56, 46.23) * mm});
            skLineSegment(sketch, "E1412", {"start": v(-77.95, 46.43) * mm, "end": v(-77.75, 46.31) * mm});
            skLineSegment(sketch, "E1413", {"start": v(-65.62, 61.9) * mm, "end": v(-65.7, 62) * mm});
            skLineSegment(sketch, "E1414", {"start": v(-65.55, 61.8) * mm, "end": v(-65.62, 61.9) * mm});
            skLineSegment(sketch, "E1415", {"start": v(-65.49, 61.69) * mm, "end": v(-65.55, 61.8) * mm});
            skLineSegment(sketch, "E1416", {"start": v(-65.44, 61.6) * mm, "end": v(-65.49, 61.69) * mm});
            skLineSegment(sketch, "E1417", {"start": v(-65.4, 61.5) * mm, "end": v(-65.44, 61.6) * mm});
            skLineSegment(sketch, "E1418", {"start": v(-65.38, 61.4) * mm, "end": v(-65.4, 61.5) * mm});
            skLineSegment(sketch, "E1419", {"start": v(-65.37, 61.3) * mm, "end": v(-65.38, 61.4) * mm});
            skLineSegment(sketch, "E1420", {"start": v(-65.37, 61.2) * mm, "end": v(-65.37, 61.3) * mm});
            skLineSegment(sketch, "E1421", {"start": v(-65.38, 61.1) * mm, "end": v(-65.37, 61.2) * mm});
            skLineSegment(sketch, "E1422", {"start": v(-65.4, 61) * mm, "end": v(-65.38, 61.1) * mm});
            skLineSegment(sketch, "E1423", {"start": v(-65.44, 60.9) * mm, "end": v(-65.4, 61) * mm});
            skLineSegment(sketch, "E1424", {"start": v(-65.48, 60.82) * mm, "end": v(-65.44, 60.9) * mm});
            skLineSegment(sketch, "E1425", {"start": v(-65.54, 60.73) * mm, "end": v(-65.48, 60.82) * mm});
            skLineSegment(sketch, "E1426", {"start": v(-65.61, 60.65) * mm, "end": v(-65.54, 60.73) * mm});
            skLineSegment(sketch, "E1427", {"start": v(-65.7, 60.57) * mm, "end": v(-65.61, 60.65) * mm});
            skLineSegment(sketch, "E1428", {"start": v(-65.78, 60.5) * mm, "end": v(-65.7, 60.57) * mm});
            skLineSegment(sketch, "E1429", {"start": v(-65.86, 60.45) * mm, "end": v(-65.78, 60.5) * mm});
            skLineSegment(sketch, "E1430", {"start": v(-65.95, 60.41) * mm, "end": v(-65.86, 60.45) * mm});
            skLineSegment(sketch, "E1431", {"start": v(-66.03, 60.39) * mm, "end": v(-65.95, 60.41) * mm});
            skLineSegment(sketch, "E1432", {"start": v(-66.12, 60.37) * mm, "end": v(-66.03, 60.39) * mm});
            skLineSegment(sketch, "E1433", {"start": v(-66.22, 60.37) * mm, "end": v(-66.12, 60.37) * mm});
            skLineSegment(sketch, "E1434", {"start": v(-66.31, 60.38) * mm, "end": v(-66.22, 60.37) * mm});
            skLineSegment(sketch, "E1435", {"start": v(-66.41, 60.4) * mm, "end": v(-66.31, 60.38) * mm});
            skLineSegment(sketch, "E1436", {"start": v(-66.51, 60.45) * mm, "end": v(-66.41, 60.4) * mm});
            skLineSegment(sketch, "E1437", {"start": v(-66.6, 60.5) * mm, "end": v(-66.51, 60.45) * mm});
            skLineSegment(sketch, "E1438", {"start": v(-66.7, 60.56) * mm, "end": v(-66.6, 60.5) * mm});
            skLineSegment(sketch, "E1439", {"start": v(-66.8, 60.63) * mm, "end": v(-66.7, 60.56) * mm});
            skLineSegment(sketch, "E1440", {"start": v(-66.9, 60.72) * mm, "end": v(-66.8, 60.63) * mm});
            skLineSegment(sketch, "E1441", {"start": v(-66.9, 60.72) * mm, "end": v(-65.7, 62) * mm});
            skLineSegment(sketch, "E1442", {"start": v(-35.33, -81.4) * mm, "end": v(-35.37, -81.53) * mm});
            skLineSegment(sketch, "E1443", {"start": v(-35.35, -81.27) * mm, "end": v(-35.33, -81.4) * mm});
            skLineSegment(sketch, "E1444", {"start": v(-35.4, -81.18) * mm, "end": v(-35.35, -81.27) * mm});
            skLineSegment(sketch, "E1445", {"start": v(-35.5, -81.1) * mm, "end": v(-35.4, -81.18) * mm});
            skLineSegment(sketch, "E1446", {"start": v(-35.6, -81.08) * mm, "end": v(-35.5, -81.1) * mm});
            skLineSegment(sketch, "E1447", {"start": v(-35.74, -81.1) * mm, "end": v(-35.6, -81.08) * mm});
            skLineSegment(sketch, "E1448", {"start": v(-35.83, -81.15) * mm, "end": v(-35.74, -81.1) * mm});
            skLineSegment(sketch, "E1449", {"start": v(-35.92, -81.3) * mm, "end": v(-35.83, -81.15) * mm});
            skLineSegment(sketch, "E1450", {"start": v(-35.96, -81.42) * mm, "end": v(-35.92, -81.3) * mm});
            skLineSegment(sketch, "E1451", {"start": v(-35.94, -81.56) * mm, "end": v(-35.96, -81.42) * mm});
            skLineSegment(sketch, "E1452", {"start": v(-35.89, -81.65) * mm, "end": v(-35.94, -81.56) * mm});
            skLineSegment(sketch, "E1453", {"start": v(-35.78, -81.72) * mm, "end": v(-35.89, -81.65) * mm});
            skLineSegment(sketch, "E1454", {"start": v(-35.68, -81.75) * mm, "end": v(-35.78, -81.72) * mm});
            skLineSegment(sketch, "E1455", {"start": v(-35.55, -81.73) * mm, "end": v(-35.68, -81.75) * mm});
            skLineSegment(sketch, "E1456", {"start": v(-35.46, -81.67) * mm, "end": v(-35.55, -81.73) * mm});
            skLineSegment(sketch, "E1457", {"start": v(-35.37, -81.53) * mm, "end": v(-35.46, -81.67) * mm});
            skLineSegment(sketch, "E1458", {"start": v(-39.61, -81.59) * mm, "end": v(-39.6, -81.7) * mm});
            skLineSegment(sketch, "E1459", {"start": v(-39.57, -81.45) * mm, "end": v(-39.61, -81.59) * mm});
            skLineSegment(sketch, "E1460", {"start": v(-39.47, -81.33) * mm, "end": v(-39.57, -81.45) * mm});
            skLineSegment(sketch, "E1461", {"start": v(-39.27, -81.25) * mm, "end": v(-39.47, -81.33) * mm});
            skLineSegment(sketch, "E1462", {"start": v(-39.06, -81.27) * mm, "end": v(-39.27, -81.25) * mm});
            skLineSegment(sketch, "E1463", {"start": v(-38.73, -81.39) * mm, "end": v(-39.06, -81.27) * mm});
            skLineSegment(sketch, "E1464", {"start": v(-38.41, -81.59) * mm, "end": v(-38.73, -81.39) * mm});
            skLineSegment(sketch, "E1465", {"start": v(-38, -81.97) * mm, "end": v(-38.41, -81.59) * mm});
            skLineSegment(sketch, "E1466", {"start": v(-38, -81.97) * mm, "end": v(-37.66, -81.67) * mm});
            skLineSegment(sketch, "E1467", {"start": v(-38, -81.34) * mm, "end": v(-37.66, -81.67) * mm});
            skLineSegment(sketch, "E1468", {"start": v(-38.52, -81.02) * mm, "end": v(-38, -81.34) * mm});
            skLineSegment(sketch, "E1469", {"start": v(-38.95, -80.86) * mm, "end": v(-38.52, -81.02) * mm});
            skLineSegment(sketch, "E1470", {"start": v(-39.44, -80.84) * mm, "end": v(-38.95, -80.86) * mm});
            skLineSegment(sketch, "E1471", {"start": v(-39.75, -80.96) * mm, "end": v(-39.44, -80.84) * mm});
            skLineSegment(sketch, "E1472", {"start": v(-40.02, -81.28) * mm, "end": v(-39.75, -80.96) * mm});
            skLineSegment(sketch, "E1473", {"start": v(-40.09, -81.45) * mm, "end": v(-40.02, -81.28) * mm});
            skLineSegment(sketch, "E1474", {"start": v(-40.1, -81.67) * mm, "end": v(-40.09, -81.45) * mm});
            skLineSegment(sketch, "E1475", {"start": v(-40.07, -81.84) * mm, "end": v(-40.1, -81.67) * mm});
            skLineSegment(sketch, "E1476", {"start": v(-39.97, -82.06) * mm, "end": v(-40.07, -81.84) * mm});
            skLineSegment(sketch, "E1477", {"start": v(-39.82, -82.27) * mm, "end": v(-39.97, -82.06) * mm});
            skLineSegment(sketch, "E1478", {"start": v(-39.5, -82.62) * mm, "end": v(-39.82, -82.27) * mm});
            skLineSegment(sketch, "E1479", {"start": v(-39.24, -82.93) * mm, "end": v(-39.5, -82.62) * mm});
            skLineSegment(sketch, "E1480", {"start": v(-39.05, -83.2) * mm, "end": v(-39.24, -82.93) * mm});
            skLineSegment(sketch, "E1481", {"start": v(-39, -83.38) * mm, "end": v(-39.05, -83.2) * mm});
            skLineSegment(sketch, "E1482", {"start": v(-39.04, -83.58) * mm, "end": v(-39, -83.38) * mm});
            skLineSegment(sketch, "E1483", {"start": v(-39.17, -83.75) * mm, "end": v(-39.04, -83.58) * mm});
            skLineSegment(sketch, "E1484", {"start": v(-39.4, -83.84) * mm, "end": v(-39.17, -83.75) * mm});
            skLineSegment(sketch, "E1485", {"start": v(-39.64, -83.82) * mm, "end": v(-39.4, -83.84) * mm});
            skLineSegment(sketch, "E1486", {"start": v(-40, -83.69) * mm, "end": v(-39.64, -83.82) * mm});
            skLineSegment(sketch, "E1487", {"start": v(-40.2, -83.58) * mm, "end": v(-40, -83.69) * mm});
            skLineSegment(sketch, "E1488", {"start": v(-40.45, -83.4) * mm, "end": v(-40.2, -83.58) * mm});
            skLineSegment(sketch, "E1489", {"start": v(-40.64, -83.23) * mm, "end": v(-40.45, -83.4) * mm});
            skLineSegment(sketch, "E1490", {"start": v(-40.84, -83) * mm, "end": v(-40.64, -83.23) * mm});
            skLineSegment(sketch, "E1491", {"start": v(-40.84, -83) * mm, "end": v(-41.04, -83.42) * mm});
            skLineSegment(sketch, "E1492", {"start": v(-40.76, -83.72) * mm, "end": v(-41.04, -83.42) * mm});
            skLineSegment(sketch, "E1493", {"start": v(-40.2, -84.06) * mm, "end": v(-40.76, -83.72) * mm});
            skLineSegment(sketch, "E1494", {"start": v(-39.73, -84.23) * mm, "end": v(-40.2, -84.06) * mm});
            skLineSegment(sketch, "E1495", {"start": v(-39.2, -84.25) * mm, "end": v(-39.73, -84.23) * mm});
            skLineSegment(sketch, "E1496", {"start": v(-38.88, -84.12) * mm, "end": v(-39.2, -84.25) * mm});
            skLineSegment(sketch, "E1497", {"start": v(-38.58, -83.75) * mm, "end": v(-38.88, -84.12) * mm});
            skLineSegment(sketch, "E1498", {"start": v(-38.5, -83.5) * mm, "end": v(-38.58, -83.75) * mm});
            skLineSegment(sketch, "E1499", {"start": v(-38.53, -83.17) * mm, "end": v(-38.5, -83.5) * mm});
            skLineSegment(sketch, "E1500", {"start": v(-38.68, -82.88) * mm, "end": v(-38.53, -83.17) * mm});
            skLineSegment(sketch, "E1501", {"start": v(-39.07, -82.42) * mm, "end": v(-38.68, -82.88) * mm});
            skLineSegment(sketch, "E1502", {"start": v(-39.3, -82.17) * mm, "end": v(-39.07, -82.42) * mm});
            skLineSegment(sketch, "E1503", {"start": v(-39.49, -81.95) * mm, "end": v(-39.3, -82.17) * mm});
            skLineSegment(sketch, "E1504", {"start": v(-39.56, -81.83) * mm, "end": v(-39.49, -81.95) * mm});
            skLineSegment(sketch, "E1505", {"start": v(-39.6, -81.7) * mm, "end": v(-39.56, -81.83) * mm});
            skLineSegment(sketch, "E1506", {"start": v(-89.24, -1.41) * mm, "end": v(-89.22, -1.67) * mm});
            skLineSegment(sketch, "E1507", {"start": v(-89.3, -1.08) * mm, "end": v(-89.24, -1.41) * mm});
            skLineSegment(sketch, "E1508", {"start": v(-89.38, -0.83) * mm, "end": v(-89.3, -1.08) * mm});
            skLineSegment(sketch, "E1509", {"start": v(-89.52, -0.54) * mm, "end": v(-89.38, -0.83) * mm});
            skLineSegment(sketch, "E1510", {"start": v(-89.52, -0.54) * mm, "end": v(-89.9, -0.7) * mm});
            skLineSegment(sketch, "E1511", {"start": v(-89.72, -1.15) * mm, "end": v(-89.9, -0.7) * mm});
            skLineSegment(sketch, "E1512", {"start": v(-89.64, -1.65) * mm, "end": v(-89.72, -1.15) * mm});
            skLineSegment(sketch, "E1513", {"start": v(-89.67, -1.94) * mm, "end": v(-89.64, -1.65) * mm});
            skLineSegment(sketch, "E1514", {"start": v(-89.82, -2.2) * mm, "end": v(-89.67, -1.94) * mm});
            skLineSegment(sketch, "E1515", {"start": v(-90.02, -2.3) * mm, "end": v(-89.82, -2.2) * mm});
            skLineSegment(sketch, "E1516", {"start": v(-90.4, -2.37) * mm, "end": v(-90.02, -2.3) * mm});
            skLineSegment(sketch, "E1517", {"start": v(-90.4, -2.37) * mm, "end": v(-90.6, -2.37) * mm});
            skLineSegment(sketch, "E1518", {"start": v(-90.6, -2.37) * mm, "end": v(-90.63, -1.8) * mm});
            skLineSegment(sketch, "E1519", {"start": v(-90.87, -0.7) * mm, "end": v(-90.63, -1.8) * mm});
            skLineSegment(sketch, "E1520", {"start": v(-91.71, -0.2) * mm, "end": v(-90.87, -0.7) * mm});
            skLineSegment(sketch, "E1521", {"start": v(-92.08, -0.26) * mm, "end": v(-91.71, -0.2) * mm});
            skLineSegment(sketch, "E1522", {"start": v(-92.44, -0.49) * mm, "end": v(-92.08, -0.26) * mm});
            skLineSegment(sketch, "E1523", {"start": v(-41.87, -80.19) * mm, "end": v(-41.88, -80.09) * mm});
            skLineSegment(sketch, "E1524", {"start": v(-41.88, -80.09) * mm, "end": v(-41.9, -80) * mm});
            skLineSegment(sketch, "E1525", {"start": v(-41.9, -80) * mm, "end": v(-41.94, -79.92) * mm});
            skLineSegment(sketch, "E1526", {"start": v(-41.94, -79.92) * mm, "end": v(-41.99, -79.84) * mm});
            skLineSegment(sketch, "E1527", {"start": v(-41.99, -79.84) * mm, "end": v(-42.05, -79.77) * mm});
            skLineSegment(sketch, "E1528", {"start": v(-42.05, -79.77) * mm, "end": v(-42.12, -79.7) * mm});
            skLineSegment(sketch, "E1529", {"start": v(-42.12, -79.7) * mm, "end": v(-42.2, -79.63) * mm});
            skLineSegment(sketch, "E1530", {"start": v(-42.2, -79.63) * mm, "end": v(-42.3, -79.58) * mm});
            skLineSegment(sketch, "E1531", {"start": v(-42.3, -79.58) * mm, "end": v(-42.4, -79.53) * mm});
            skLineSegment(sketch, "E1532", {"start": v(-42.4, -79.53) * mm, "end": v(-42.5, -79.5) * mm});
            skLineSegment(sketch, "E1533", {"start": v(-42.5, -79.5) * mm, "end": v(-42.6, -79.47) * mm});
            skLineSegment(sketch, "E1534", {"start": v(-42.6, -79.47) * mm, "end": v(-42.7, -79.46) * mm});
            skLineSegment(sketch, "E1535", {"start": v(-42.7, -79.46) * mm, "end": v(-42.8, -79.46) * mm});
            skLineSegment(sketch, "E1536", {"start": v(-42.8, -79.46) * mm, "end": v(-42.9, -79.48) * mm});
            skLineSegment(sketch, "E1537", {"start": v(-42.9, -79.48) * mm, "end": v(-42.99, -79.5) * mm});
            skLineSegment(sketch, "E1538", {"start": v(-42.99, -79.5) * mm, "end": v(-43.08, -79.54) * mm});
            skLineSegment(sketch, "E1539", {"start": v(-43.08, -79.54) * mm, "end": v(-43.17, -79.6) * mm});
            skLineSegment(sketch, "E1540", {"start": v(-43.17, -79.6) * mm, "end": v(-43.26, -79.65) * mm});
            skLineSegment(sketch, "E1541", {"start": v(-43.26, -79.65) * mm, "end": v(-43.34, -79.72) * mm});
            skLineSegment(sketch, "E1542", {"start": v(-43.34, -79.72) * mm, "end": v(-43.42, -79.8) * mm});
            skLineSegment(sketch, "E1543", {"start": v(-43.42, -79.8) * mm, "end": v(-43.5, -79.9) * mm});
            skLineSegment(sketch, "E1544", {"start": v(-43.5, -79.9) * mm, "end": v(-43.58, -80.01) * mm});
            skLineSegment(sketch, "E1545", {"start": v(-34.86, -86.28) * mm, "end": v(-34.3, -86.5) * mm});
            skLineSegment(sketch, "E1546", {"start": v(-34.86, -86.28) * mm, "end": v(-34.98, -86.24) * mm});
            skLineSegment(sketch, "E1547", {"start": v(-34.98, -86.24) * mm, "end": v(-35.1, -86.21) * mm});
            skLineSegment(sketch, "E1548", {"start": v(-35.1, -86.21) * mm, "end": v(-35.2, -86.2) * mm});
            skLineSegment(sketch, "E1549", {"start": v(-35.2, -86.2) * mm, "end": v(-35.28, -86.2) * mm});
            skLineSegment(sketch, "E1550", {"start": v(-35.28, -86.2) * mm, "end": v(-35.35, -86.21) * mm});
            skLineSegment(sketch, "E1551", {"start": v(-35.35, -86.21) * mm, "end": v(-35.42, -86.23) * mm});
            skLineSegment(sketch, "E1552", {"start": v(-35.42, -86.23) * mm, "end": v(-35.5, -86.27) * mm});
            skLineSegment(sketch, "E1553", {"start": v(-35.5, -86.27) * mm, "end": v(-35.59, -86.32) * mm});
            skLineSegment(sketch, "E1554", {"start": v(-35.59, -86.32) * mm, "end": v(-35.65, -86.39) * mm});
            skLineSegment(sketch, "E1555", {"start": v(-35.65, -86.39) * mm, "end": v(-35.7, -86.45) * mm});
            skLineSegment(sketch, "E1556", {"start": v(-35.7, -86.45) * mm, "end": v(-35.74, -86.52) * mm});
            skLineSegment(sketch, "E1557", {"start": v(-35.74, -86.52) * mm, "end": v(-35.78, -86.6) * mm});
            skLineSegment(sketch, "E1558", {"start": v(-35.78, -86.6) * mm, "end": v(-35.8, -86.7) * mm});
            skLineSegment(sketch, "E1559", {"start": v(-35.8, -86.7) * mm, "end": v(-35.82, -86.78) * mm});
            skLineSegment(sketch, "E1560", {"start": v(-35.82, -86.78) * mm, "end": v(-35.8, -86.87) * mm});
            skLineSegment(sketch, "E1561", {"start": v(-35.8, -86.87) * mm, "end": v(-35.8, -86.94) * mm});
            skLineSegment(sketch, "E1562", {"start": v(-35.8, -86.94) * mm, "end": v(-35.76, -87) * mm});
            skLineSegment(sketch, "E1563", {"start": v(-35.76, -87) * mm, "end": v(-35.72, -87.07) * mm});
            skLineSegment(sketch, "E1564", {"start": v(-35.72, -87.07) * mm, "end": v(-35.65, -87.14) * mm});
            skLineSegment(sketch, "E1565", {"start": v(-35.65, -87.14) * mm, "end": v(-35.57, -87.22) * mm});
            skLineSegment(sketch, "E1566", {"start": v(-35.57, -87.22) * mm, "end": v(-35.47, -87.3) * mm});
            skLineSegment(sketch, "E1567", {"start": v(-35.47, -87.3) * mm, "end": v(-35.38, -87.34) * mm});
            skLineSegment(sketch, "E1568", {"start": v(-35.38, -87.34) * mm, "end": v(-35.27, -87.4) * mm});
            skLineSegment(sketch, "E1569", {"start": v(-35.27, -87.4) * mm, "end": v(-35.16, -87.44) * mm});
            skLineSegment(sketch, "E1570", {"start": v(-35.16, -87.44) * mm, "end": v(-35, -87.5) * mm});
            skLineSegment(sketch, "E1571", {"start": v(-35, -87.5) * mm, "end": v(-34.85, -87.55) * mm});
            skLineSegment(sketch, "E1572", {"start": v(-34.85, -87.55) * mm, "end": v(-34.7, -87.59) * mm});
            skLineSegment(sketch, "E1573", {"start": v(-34.7, -87.59) * mm, "end": v(-34.57, -87.61) * mm});
            skLineSegment(sketch, "E1574", {"start": v(-34.57, -87.61) * mm, "end": v(-34.45, -87.63) * mm});
            skLineSegment(sketch, "E1575", {"start": v(-34.45, -87.63) * mm, "end": v(-34.33, -87.63) * mm});
            skLineSegment(sketch, "E1576", {"start": v(-34.33, -87.63) * mm, "end": v(-34.22, -87.62) * mm});
            skLineSegment(sketch, "E1577", {"start": v(-34.22, -87.62) * mm, "end": v(-34.12, -87.6) * mm});
            skLineSegment(sketch, "E1578", {"start": v(-34.12, -87.6) * mm, "end": v(-34.04, -87.56) * mm});
            skLineSegment(sketch, "E1579", {"start": v(-34.04, -87.56) * mm, "end": v(-33.96, -87.52) * mm});
            skLineSegment(sketch, "E1580", {"start": v(-33.96, -87.52) * mm, "end": v(-33.9, -87.47) * mm});
            skLineSegment(sketch, "E1581", {"start": v(-33.9, -87.47) * mm, "end": v(-33.83, -87.4) * mm});
            skLineSegment(sketch, "E1582", {"start": v(-33.83, -87.4) * mm, "end": v(-33.78, -87.33) * mm});
            skLineSegment(sketch, "E1583", {"start": v(-33.78, -87.33) * mm, "end": v(-33.74, -87.25) * mm});
            skLineSegment(sketch, "E1584", {"start": v(-33.74, -87.25) * mm, "end": v(-33.7, -87.16) * mm});
            skLineSegment(sketch, "E1585", {"start": v(-33.7, -87.16) * mm, "end": v(-33.7, -87.07) * mm});
            skLineSegment(sketch, "E1586", {"start": v(-33.7, -87.07) * mm, "end": v(-33.7, -87) * mm});
            skLineSegment(sketch, "E1587", {"start": v(-33.7, -87) * mm, "end": v(-33.7, -86.94) * mm});
            skLineSegment(sketch, "E1588", {"start": v(-33.7, -86.94) * mm, "end": v(-33.72, -86.89) * mm});
            skLineSegment(sketch, "E1589", {"start": v(-33.72, -86.89) * mm, "end": v(-33.75, -86.84) * mm});
            skLineSegment(sketch, "E1590", {"start": v(-33.75, -86.84) * mm, "end": v(-33.8, -86.8) * mm});
            skLineSegment(sketch, "E1591", {"start": v(-33.8, -86.8) * mm, "end": v(-33.84, -86.75) * mm});
            skLineSegment(sketch, "E1592", {"start": v(-33.84, -86.75) * mm, "end": v(-33.9, -86.7) * mm});
            skLineSegment(sketch, "E1593", {"start": v(-33.9, -86.7) * mm, "end": v(-33.98, -86.65) * mm});
            skLineSegment(sketch, "E1594", {"start": v(-33.98, -86.65) * mm, "end": v(-34.08, -86.6) * mm});
            skLineSegment(sketch, "E1595", {"start": v(-34.08, -86.6) * mm, "end": v(-34.18, -86.56) * mm});
            skLineSegment(sketch, "E1596", {"start": v(-34.18, -86.56) * mm, "end": v(-34.3, -86.5) * mm});
            skLineSegment(sketch, "E1597", {"start": v(-34.04, -85.01) * mm, "end": v(-33.91, -85.05) * mm});
            skLineSegment(sketch, "E1598", {"start": v(-33.91, -85.05) * mm, "end": v(-33.8, -85.08) * mm});
            skLineSegment(sketch, "E1599", {"start": v(-33.8, -85.08) * mm, "end": v(-33.68, -85.1) * mm});
            skLineSegment(sketch, "E1600", {"start": v(-33.68, -85.1) * mm, "end": v(-33.58, -85.08) * mm});
            skLineSegment(sketch, "E1601", {"start": v(-33.58, -85.08) * mm, "end": v(-33.49, -85.06) * mm});
            skLineSegment(sketch, "E1602", {"start": v(-33.49, -85.06) * mm, "end": v(-33.4, -85.02) * mm});
            skLineSegment(sketch, "E1603", {"start": v(-33.4, -85.02) * mm, "end": v(-33.32, -84.97) * mm});
            skLineSegment(sketch, "E1604", {"start": v(-33.32, -84.97) * mm, "end": v(-33.25, -84.9) * mm});
            skLineSegment(sketch, "E1605", {"start": v(-33.25, -84.9) * mm, "end": v(-33.19, -84.82) * mm});
            skLineSegment(sketch, "E1606", {"start": v(-33.19, -84.82) * mm, "end": v(-33.13, -84.73) * mm});
            skLineSegment(sketch, "E1607", {"start": v(-33.13, -84.73) * mm, "end": v(-33.08, -84.62) * mm});
            skLineSegment(sketch, "E1608", {"start": v(-33.08, -84.62) * mm, "end": v(-33.04, -84.5) * mm});
            skLineSegment(sketch, "E1609", {"start": v(-33.04, -84.5) * mm, "end": v(-33.02, -84.4) * mm});
            skLineSegment(sketch, "E1610", {"start": v(-33.02, -84.4) * mm, "end": v(-33, -84.3) * mm});
            skLineSegment(sketch, "E1611", {"start": v(-33, -84.3) * mm, "end": v(-33, -84.21) * mm});
            skLineSegment(sketch, "E1612", {"start": v(-33, -84.21) * mm, "end": v(-33.01, -84.13) * mm});
            skLineSegment(sketch, "E1613", {"start": v(-33.01, -84.13) * mm, "end": v(-33.04, -84.04) * mm});
            skLineSegment(sketch, "E1614", {"start": v(-33.04, -84.04) * mm, "end": v(-33.07, -83.97) * mm});
            skLineSegment(sketch, "E1615", {"start": v(-33.07, -83.97) * mm, "end": v(-33.13, -83.89) * mm});
            skLineSegment(sketch, "E1616", {"start": v(-33.13, -83.89) * mm, "end": v(-33.2, -83.82) * mm});
            skLineSegment(sketch, "E1617", {"start": v(-33.2, -83.82) * mm, "end": v(-33.28, -83.75) * mm});
            skLineSegment(sketch, "E1618", {"start": v(-33.28, -83.75) * mm, "end": v(-33.38, -83.7) * mm});
            skLineSegment(sketch, "E1619", {"start": v(-33.38, -83.7) * mm, "end": v(-33.5, -83.64) * mm});
            skLineSegment(sketch, "E1620", {"start": v(-33.5, -83.64) * mm, "end": v(-33.62, -83.6) * mm});
            skLineSegment(sketch, "E1621", {"start": v(-33.62, -83.6) * mm, "end": v(-33.73, -83.57) * mm});
            skLineSegment(sketch, "E1622", {"start": v(-33.73, -83.57) * mm, "end": v(-33.84, -83.57) * mm});
            skLineSegment(sketch, "E1623", {"start": v(-33.84, -83.57) * mm, "end": v(-33.92, -83.57) * mm});
            skLineSegment(sketch, "E1624", {"start": v(-33.92, -83.57) * mm, "end": v(-34, -83.59) * mm});
            skLineSegment(sketch, "E1625", {"start": v(-34, -83.59) * mm, "end": v(-34.08, -83.61) * mm});
            skLineSegment(sketch, "E1626", {"start": v(-34.08, -83.61) * mm, "end": v(-34.14, -83.65) * mm});
            skLineSegment(sketch, "E1627", {"start": v(-34.14, -83.65) * mm, "end": v(-34.2, -83.7) * mm});
            skLineSegment(sketch, "E1628", {"start": v(-34.2, -83.7) * mm, "end": v(-34.27, -83.75) * mm});
            skLineSegment(sketch, "E1629", {"start": v(-34.27, -83.75) * mm, "end": v(-34.32, -83.8) * mm});
            skLineSegment(sketch, "E1630", {"start": v(-34.32, -83.8) * mm, "end": v(-34.38, -83.89) * mm});
            skLineSegment(sketch, "E1631", {"start": v(-34.38, -83.89) * mm, "end": v(-34.42, -83.97) * mm});
            skLineSegment(sketch, "E1632", {"start": v(-34.42, -83.97) * mm, "end": v(-34.47, -84.07) * mm});
            skLineSegment(sketch, "E1633", {"start": v(-34.47, -84.07) * mm, "end": v(-34.5, -84.16) * mm});
            skLineSegment(sketch, "E1634", {"start": v(-34.5, -84.16) * mm, "end": v(-34.52, -84.25) * mm});
            skLineSegment(sketch, "E1635", {"start": v(-34.52, -84.25) * mm, "end": v(-34.53, -84.33) * mm});
            skLineSegment(sketch, "E1636", {"start": v(-34.53, -84.33) * mm, "end": v(-34.54, -84.4) * mm});
            skLineSegment(sketch, "E1637", {"start": v(-34.54, -84.4) * mm, "end": v(-34.53, -84.49) * mm});
            skLineSegment(sketch, "E1638", {"start": v(-34.53, -84.49) * mm, "end": v(-34.51, -84.56) * mm});
            skLineSegment(sketch, "E1639", {"start": v(-34.51, -84.56) * mm, "end": v(-34.48, -84.64) * mm});
            skLineSegment(sketch, "E1640", {"start": v(-34.48, -84.64) * mm, "end": v(-34.43, -84.72) * mm});
            skLineSegment(sketch, "E1641", {"start": v(-34.43, -84.72) * mm, "end": v(-34.37, -84.8) * mm});
            skLineSegment(sketch, "E1642", {"start": v(-34.37, -84.8) * mm, "end": v(-34.28, -84.87) * mm});
            skLineSegment(sketch, "E1643", {"start": v(-34.28, -84.87) * mm, "end": v(-34.21, -84.92) * mm});
            skLineSegment(sketch, "E1644", {"start": v(-34.21, -84.92) * mm, "end": v(-34.13, -84.97) * mm});
            skLineSegment(sketch, "E1645", {"start": v(-34.13, -84.97) * mm, "end": v(-34.04, -85.01) * mm});
            skLineSegment(sketch, "E1646", {"start": v(-24.36, -87.86) * mm, "end": v(-26.04, -87.37) * mm});
            skLineSegment(sketch, "E1647", {"start": v(-24.36, -87.86) * mm, "end": v(-24.32, -87.73) * mm});
            skLineSegment(sketch, "E1648", {"start": v(-24.32, -87.73) * mm, "end": v(-24.3, -87.61) * mm});
            skLineSegment(sketch, "E1649", {"start": v(-24.3, -87.61) * mm, "end": v(-24.3, -87.5) * mm});
            skLineSegment(sketch, "E1650", {"start": v(-24.3, -87.5) * mm, "end": v(-24.3, -87.4) * mm});
            skLineSegment(sketch, "E1651", {"start": v(-24.3, -87.4) * mm, "end": v(-24.3, -87.29) * mm});
            skLineSegment(sketch, "E1652", {"start": v(-24.3, -87.29) * mm, "end": v(-24.32, -87.19) * mm});
            skLineSegment(sketch, "E1653", {"start": v(-24.32, -87.19) * mm, "end": v(-24.36, -87.1) * mm});
            skLineSegment(sketch, "E1654", {"start": v(-24.36, -87.1) * mm, "end": v(-24.4, -87.01) * mm});
            skLineSegment(sketch, "E1655", {"start": v(-24.4, -87.01) * mm, "end": v(-24.45, -86.94) * mm});
            skLineSegment(sketch, "E1656", {"start": v(-24.45, -86.94) * mm, "end": v(-24.51, -86.87) * mm});
            skLineSegment(sketch, "E1657", {"start": v(-24.51, -86.87) * mm, "end": v(-24.59, -86.81) * mm});
            skLineSegment(sketch, "E1658", {"start": v(-24.59, -86.81) * mm, "end": v(-24.67, -86.76) * mm});
            skLineSegment(sketch, "E1659", {"start": v(-24.67, -86.76) * mm, "end": v(-24.77, -86.72) * mm});
            skLineSegment(sketch, "E1660", {"start": v(-24.77, -86.72) * mm, "end": v(-24.87, -86.68) * mm});
            skLineSegment(sketch, "E1661", {"start": v(-24.87, -86.68) * mm, "end": v(-24.98, -86.65) * mm});
            skLineSegment(sketch, "E1662", {"start": v(-24.98, -86.65) * mm, "end": v(-25.08, -86.64) * mm});
            skLineSegment(sketch, "E1663", {"start": v(-25.08, -86.64) * mm, "end": v(-25.18, -86.64) * mm});
            skLineSegment(sketch, "E1664", {"start": v(-25.18, -86.64) * mm, "end": v(-25.28, -86.65) * mm});
            skLineSegment(sketch, "E1665", {"start": v(-25.28, -86.65) * mm, "end": v(-25.38, -86.67) * mm});
            skLineSegment(sketch, "E1666", {"start": v(-25.38, -86.67) * mm, "end": v(-25.47, -86.7) * mm});
            skLineSegment(sketch, "E1667", {"start": v(-25.47, -86.7) * mm, "end": v(-25.56, -86.75) * mm});
            skLineSegment(sketch, "E1668", {"start": v(-25.56, -86.75) * mm, "end": v(-25.64, -86.8) * mm});
            skLineSegment(sketch, "E1669", {"start": v(-25.64, -86.8) * mm, "end": v(-25.72, -86.88) * mm});
            skLineSegment(sketch, "E1670", {"start": v(-25.72, -86.88) * mm, "end": v(-25.8, -86.95) * mm});
            skLineSegment(sketch, "E1671", {"start": v(-25.8, -86.95) * mm, "end": v(-25.86, -87.04) * mm});
            skLineSegment(sketch, "E1672", {"start": v(-25.86, -87.04) * mm, "end": v(-25.92, -87.14) * mm});
            skLineSegment(sketch, "E1673", {"start": v(-25.92, -87.14) * mm, "end": v(-25.98, -87.25) * mm});
            skLineSegment(sketch, "E1674", {"start": v(-25.98, -87.25) * mm, "end": v(-26.04, -87.37) * mm});
            skLineSegment(sketch, "E1675", {"start": v(-20.7, -87.78) * mm, "end": v(-20.8, -87.76) * mm});
            skLineSegment(sketch, "E1676", {"start": v(-20.8, -87.76) * mm, "end": v(-20.92, -87.75) * mm});
            skLineSegment(sketch, "E1677", {"start": v(-20.92, -87.75) * mm, "end": v(-21.03, -87.76) * mm});
            skLineSegment(sketch, "E1678", {"start": v(-21.03, -87.76) * mm, "end": v(-21.14, -87.79) * mm});
            skLineSegment(sketch, "E1679", {"start": v(-21.14, -87.79) * mm, "end": v(-21.24, -87.83) * mm});
            skLineSegment(sketch, "E1680", {"start": v(-21.24, -87.83) * mm, "end": v(-21.34, -87.89) * mm});
            skLineSegment(sketch, "E1681", {"start": v(-21.34, -87.89) * mm, "end": v(-21.43, -87.96) * mm});
            skLineSegment(sketch, "E1682", {"start": v(-21.43, -87.96) * mm, "end": v(-21.54, -88.08) * mm});
            skLineSegment(sketch, "E1683", {"start": v(-21.54, -88.08) * mm, "end": v(-21.64, -88.22) * mm});
            skLineSegment(sketch, "E1684", {"start": v(-21.64, -88.22) * mm, "end": v(-21.73, -88.38) * mm});
            skLineSegment(sketch, "E1685", {"start": v(-21.73, -88.38) * mm, "end": v(-21.79, -88.53) * mm});
            skLineSegment(sketch, "E1686", {"start": v(-21.79, -88.53) * mm, "end": v(-21.84, -88.69) * mm});
            skLineSegment(sketch, "E1687", {"start": v(-21.84, -88.69) * mm, "end": v(-21.89, -88.86) * mm});
            skLineSegment(sketch, "E1688", {"start": v(-21.89, -88.86) * mm, "end": v(-21.93, -89.03) * mm});
            skLineSegment(sketch, "E1689", {"start": v(-21.93, -89.03) * mm, "end": v(-21.95, -89.19) * mm});
            skLineSegment(sketch, "E1690", {"start": v(-21.95, -89.19) * mm, "end": v(-21.96, -89.34) * mm});
            skLineSegment(sketch, "E1691", {"start": v(-21.96, -89.34) * mm, "end": v(-21.96, -89.48) * mm});
            skLineSegment(sketch, "E1692", {"start": v(-21.96, -89.48) * mm, "end": v(-21.95, -89.61) * mm});
            skLineSegment(sketch, "E1693", {"start": v(-21.95, -89.61) * mm, "end": v(-21.92, -89.74) * mm});
            skLineSegment(sketch, "E1694", {"start": v(-21.92, -89.74) * mm, "end": v(-21.88, -89.85) * mm});
            skLineSegment(sketch, "E1695", {"start": v(-21.88, -89.85) * mm, "end": v(-21.84, -89.95) * mm});
            skLineSegment(sketch, "E1696", {"start": v(-21.84, -89.95) * mm, "end": v(-21.78, -90.04) * mm});
            skLineSegment(sketch, "E1697", {"start": v(-21.78, -90.04) * mm, "end": v(-21.7, -90.12) * mm});
            skLineSegment(sketch, "E1698", {"start": v(-21.7, -90.12) * mm, "end": v(-21.62, -90.19) * mm});
            skLineSegment(sketch, "E1699", {"start": v(-21.62, -90.19) * mm, "end": v(-21.52, -90.25) * mm});
            skLineSegment(sketch, "E1700", {"start": v(-21.52, -90.25) * mm, "end": v(-21.41, -90.3) * mm});
            skLineSegment(sketch, "E1701", {"start": v(-21.41, -90.3) * mm, "end": v(-21.29, -90.33) * mm});
            skLineSegment(sketch, "E1702", {"start": v(-21.29, -90.33) * mm, "end": v(-21.15, -90.36) * mm});
            skLineSegment(sketch, "E1703", {"start": v(-21.15, -90.36) * mm, "end": v(-21.02, -90.37) * mm});
            skLineSegment(sketch, "E1704", {"start": v(-21.02, -90.37) * mm, "end": v(-20.9, -90.37) * mm});
            skLineSegment(sketch, "E1705", {"start": v(-20.9, -90.37) * mm, "end": v(-20.8, -90.36) * mm});
            skLineSegment(sketch, "E1706", {"start": v(-20.8, -90.36) * mm, "end": v(-20.68, -90.33) * mm});
            skLineSegment(sketch, "E1707", {"start": v(-20.68, -90.33) * mm, "end": v(-20.58, -90.29) * mm});
            skLineSegment(sketch, "E1708", {"start": v(-20.58, -90.29) * mm, "end": v(-20.5, -90.23) * mm});
            skLineSegment(sketch, "E1709", {"start": v(-20.5, -90.23) * mm, "end": v(-20.41, -90.16) * mm});
            skLineSegment(sketch, "E1710", {"start": v(-20.41, -90.16) * mm, "end": v(-20.34, -90.08) * mm});
            skLineSegment(sketch, "E1711", {"start": v(-20.34, -90.08) * mm, "end": v(-20.27, -89.98) * mm});
            skLineSegment(sketch, "E1712", {"start": v(-20.27, -89.98) * mm, "end": v(-20.21, -89.86) * mm});
            skLineSegment(sketch, "E1713", {"start": v(-20.21, -89.86) * mm, "end": v(-20.15, -89.72) * mm});
            skLineSegment(sketch, "E1714", {"start": v(-20.15, -89.72) * mm, "end": v(-20.1, -89.57) * mm});
            skLineSegment(sketch, "E1715", {"start": v(-20.1, -89.57) * mm, "end": v(-20.05, -89.4) * mm});
            skLineSegment(sketch, "E1716", {"start": v(-20.03, -89.3) * mm, "end": v(-20.05, -89.4) * mm});
            skLineSegment(sketch, "E1717", {"start": v(-20.03, -89.3) * mm, "end": v(-20, -89.1) * mm});
            skLineSegment(sketch, "E1718", {"start": v(-20, -89.1) * mm, "end": v(-19.96, -88.93) * mm});
            skLineSegment(sketch, "E1719", {"start": v(-19.96, -88.93) * mm, "end": v(-19.95, -88.77) * mm});
            skLineSegment(sketch, "E1720", {"start": v(-19.95, -88.77) * mm, "end": v(-19.95, -88.63) * mm});
            skLineSegment(sketch, "E1721", {"start": v(-19.95, -88.63) * mm, "end": v(-19.96, -88.49) * mm});
            skLineSegment(sketch, "E1722", {"start": v(-19.96, -88.49) * mm, "end": v(-19.99, -88.36) * mm});
            skLineSegment(sketch, "E1723", {"start": v(-19.99, -88.36) * mm, "end": v(-20.03, -88.25) * mm});
            skLineSegment(sketch, "E1724", {"start": v(-20.03, -88.25) * mm, "end": v(-20.08, -88.16) * mm});
            skLineSegment(sketch, "E1725", {"start": v(-20.08, -88.16) * mm, "end": v(-20.14, -88.07) * mm});
            skLineSegment(sketch, "E1726", {"start": v(-20.14, -88.07) * mm, "end": v(-20.22, -88) * mm});
            skLineSegment(sketch, "E1727", {"start": v(-20.22, -88) * mm, "end": v(-20.31, -87.93) * mm});
            skLineSegment(sketch, "E1728", {"start": v(-20.31, -87.93) * mm, "end": v(-20.42, -87.87) * mm});
            skLineSegment(sketch, "E1729", {"start": v(-20.42, -87.87) * mm, "end": v(-20.55, -87.82) * mm});
            skLineSegment(sketch, "E1730", {"start": v(-20.55, -87.82) * mm, "end": v(-20.7, -87.78) * mm});
            skLineSegment(sketch, "E1731", {"start": v(-13.84, -90.5) * mm, "end": v(-14, -90.5) * mm});
            skLineSegment(sketch, "E1732", {"start": v(-14, -90.5) * mm, "end": v(-14.15, -90.48) * mm});
            skLineSegment(sketch, "E1733", {"start": v(-14.15, -90.48) * mm, "end": v(-14.29, -90.48) * mm});
            skLineSegment(sketch, "E1734", {"start": v(-14.29, -90.48) * mm, "end": v(-14.41, -90.49) * mm});
            skLineSegment(sketch, "E1735", {"start": v(-14.41, -90.49) * mm, "end": v(-14.53, -90.5) * mm});
            skLineSegment(sketch, "E1736", {"start": v(-14.53, -90.5) * mm, "end": v(-14.63, -90.53) * mm});
            skLineSegment(sketch, "E1737", {"start": v(-14.63, -90.53) * mm, "end": v(-14.73, -90.56) * mm});
            skLineSegment(sketch, "E1738", {"start": v(-14.73, -90.56) * mm, "end": v(-14.8, -90.6) * mm});
            skLineSegment(sketch, "E1739", {"start": v(-14.8, -90.6) * mm, "end": v(-14.87, -90.65) * mm});
            skLineSegment(sketch, "E1740", {"start": v(-14.87, -90.65) * mm, "end": v(-14.93, -90.7) * mm});
            skLineSegment(sketch, "E1741", {"start": v(-14.93, -90.7) * mm, "end": v(-14.98, -90.77) * mm});
            skLineSegment(sketch, "E1742", {"start": v(-14.98, -90.77) * mm, "end": v(-15.02, -90.84) * mm});
            skLineSegment(sketch, "E1743", {"start": v(-15.02, -90.84) * mm, "end": v(-15.05, -90.93) * mm});
            skLineSegment(sketch, "E1744", {"start": v(-15.05, -90.93) * mm, "end": v(-15.07, -91.03) * mm});
            skLineSegment(sketch, "E1745", {"start": v(-15.07, -91.03) * mm, "end": v(-15.08, -91.13) * mm});
            skLineSegment(sketch, "E1746", {"start": v(-15.08, -91.13) * mm, "end": v(-15.08, -91.22) * mm});
            skLineSegment(sketch, "E1747", {"start": v(-15.08, -91.22) * mm, "end": v(-15.06, -91.3) * mm});
            skLineSegment(sketch, "E1748", {"start": v(-15.06, -91.3) * mm, "end": v(-15.04, -91.36) * mm});
            skLineSegment(sketch, "E1749", {"start": v(-15.04, -91.36) * mm, "end": v(-15, -91.42) * mm});
            skLineSegment(sketch, "E1750", {"start": v(-15, -91.42) * mm, "end": v(-14.97, -91.47) * mm});
            skLineSegment(sketch, "E1751", {"start": v(-14.97, -91.47) * mm, "end": v(-14.91, -91.53) * mm});
            skLineSegment(sketch, "E1752", {"start": v(-14.91, -91.53) * mm, "end": v(-14.84, -91.57) * mm});
            skLineSegment(sketch, "E1753", {"start": v(-14.84, -91.57) * mm, "end": v(-14.76, -91.62) * mm});
            skLineSegment(sketch, "E1754", {"start": v(-36.24, -82.14) * mm, "end": v(-37.6, -85.2) * mm});
            skLineSegment(sketch, "E1755", {"start": v(-14.76, -91.62) * mm, "end": v(-14.7, -91.64) * mm});
            skLineSegment(sketch, "E1756", {"start": v(-35.78, -82.34) * mm, "end": v(-36.24, -82.14) * mm});
            skLineSegment(sketch, "E1757", {"start": v(-14.7, -91.64) * mm, "end": v(-14.62, -91.66) * mm});
            skLineSegment(sketch, "E1758", {"start": v(-37.13, -85.4) * mm, "end": v(-35.78, -82.34) * mm});
            skLineSegment(sketch, "E1759", {"start": v(-14.62, -91.66) * mm, "end": v(-14.53, -91.68) * mm});
            skLineSegment(sketch, "E1760", {"start": v(-37.6, -85.2) * mm, "end": v(-37.13, -85.4) * mm});
            skLineSegment(sketch, "E1761", {"start": v(-14.53, -91.68) * mm, "end": v(-14.4, -91.7) * mm});
            skLineSegment(sketch, "E1762", {"start": v(-42.56, -82.64) * mm, "end": v(-42.34, -82.25) * mm});
            skLineSegment(sketch, "E1763", {"start": v(-14.4, -91.7) * mm, "end": v(-14.28, -91.7) * mm});
            skLineSegment(sketch, "E1764", {"start": v(-42.56, -82.64) * mm, "end": v(-42.86, -82.6) * mm});
            skLineSegment(sketch, "E1765", {"start": v(-14.28, -91.7) * mm, "end": v(-14.17, -91.7) * mm});
            skLineSegment(sketch, "E1766", {"start": v(-42.86, -82.6) * mm, "end": v(-43.08, -82.55) * mm});
            skLineSegment(sketch, "E1767", {"start": v(-14.17, -91.7) * mm, "end": v(-14.06, -91.67) * mm});
            skLineSegment(sketch, "E1768", {"start": v(-14.06, -91.67) * mm, "end": v(-13.95, -91.64) * mm});
            skLineSegment(sketch, "E1769", {"start": v(-13.95, -91.64) * mm, "end": v(-13.85, -91.6) * mm});
            skLineSegment(sketch, "E1770", {"start": v(-13.85, -91.6) * mm, "end": v(-13.76, -91.54) * mm});
            skLineSegment(sketch, "E1771", {"start": v(-13.76, -91.54) * mm, "end": v(-13.68, -91.48) * mm});
            skLineSegment(sketch, "E1772", {"start": v(-13.68, -91.48) * mm, "end": v(-13.6, -91.4) * mm});
            skLineSegment(sketch, "E1773", {"start": v(-13.6, -91.4) * mm, "end": v(-13.54, -91.32) * mm});
            skLineSegment(sketch, "E1774", {"start": v(-13.54, -91.32) * mm, "end": v(-13.49, -91.22) * mm});
            skLineSegment(sketch, "E1775", {"start": v(-13.49, -91.22) * mm, "end": v(-13.44, -91.11) * mm});
            skLineSegment(sketch, "E1776", {"start": v(-13.44, -91.11) * mm, "end": v(-13.4, -91) * mm});
            skLineSegment(sketch, "E1777", {"start": v(-13.4, -91) * mm, "end": v(-13.38, -90.87) * mm});
            skLineSegment(sketch, "E1778", {"start": v(-13.33, -90.57) * mm, "end": v(-13.38, -90.87) * mm});
            skLineSegment(sketch, "E1779", {"start": v(-13.84, -90.5) * mm, "end": v(-13.33, -90.57) * mm});
            skLineSegment(sketch, "E1780", {"start": v(1.24, -91.53) * mm, "end": v(1.23, -91.35) * mm});
            skLineSegment(sketch, "E1781", {"start": v(1.23, -91.35) * mm, "end": v(1.21, -91.2) * mm});
            skLineSegment(sketch, "E1782", {"start": v(1.21, -91.2) * mm, "end": v(1.19, -91.05) * mm});
            skLineSegment(sketch, "E1783", {"start": v(1.19, -91.05) * mm, "end": v(1.15, -90.9) * mm});
            skLineSegment(sketch, "E1784", {"start": v(1.15, -90.9) * mm, "end": v(1.1, -90.78) * mm});
            skLineSegment(sketch, "E1785", {"start": v(1.1, -90.78) * mm, "end": v(1.05, -90.66) * mm});
            skLineSegment(sketch, "E1786", {"start": v(1.05, -90.66) * mm, "end": v(0.98, -90.56) * mm});
            skLineSegment(sketch, "E1787", {"start": v(0.98, -90.56) * mm, "end": v(0.9, -90.47) * mm});
            skLineSegment(sketch, "E1788", {"start": v(0.9, -90.47) * mm, "end": v(0.81, -90.4) * mm});
            skLineSegment(sketch, "E1789", {"start": v(0.81, -90.4) * mm, "end": v(0.72, -90.34) * mm});
            skLineSegment(sketch, "E1790", {"start": v(0.72, -90.34) * mm, "end": v(0.61, -90.3) * mm});
            skLineSegment(sketch, "E1791", {"start": v(0.61, -90.3) * mm, "end": v(0.49, -90.26) * mm});
            skLineSegment(sketch, "E1792", {"start": v(0.49, -90.26) * mm, "end": v(0.36, -90.24) * mm});
            skLineSegment(sketch, "E1793", {"start": v(0.36, -90.24) * mm, "end": v(0.21, -90.23) * mm});
            skLineSegment(sketch, "E1794", {"start": v(0.21, -90.23) * mm, "end": v(0.08, -90.24) * mm});
            skLineSegment(sketch, "E1795", {"start": v(0.08, -90.24) * mm, "end": v(-0.04, -90.26) * mm});
            skLineSegment(sketch, "E1796", {"start": v(-0.04, -90.26) * mm, "end": v(-0.16, -90.29) * mm});
            skLineSegment(sketch, "E1797", {"start": v(-0.16, -90.29) * mm, "end": v(-0.27, -90.33) * mm});
            skLineSegment(sketch, "E1798", {"start": v(-0.27, -90.33) * mm, "end": v(-0.37, -90.4) * mm});
            skLineSegment(sketch, "E1799", {"start": v(-0.37, -90.4) * mm, "end": v(-0.46, -90.47) * mm});
            skLineSegment(sketch, "E1800", {"start": v(-0.46, -90.47) * mm, "end": v(-0.54, -90.56) * mm});
            skLineSegment(sketch, "E1801", {"start": v(-0.54, -90.56) * mm, "end": v(-0.6, -90.66) * mm});
            skLineSegment(sketch, "E1802", {"start": v(-0.6, -90.66) * mm, "end": v(-0.66, -90.77) * mm});
            skLineSegment(sketch, "E1803", {"start": v(-0.66, -90.77) * mm, "end": v(-0.7, -90.89) * mm});
            skLineSegment(sketch, "E1804", {"start": v(-0.7, -90.89) * mm, "end": v(-0.74, -91.02) * mm});
            skLineSegment(sketch, "E1805", {"start": v(-0.74, -91.02) * mm, "end": v(-0.77, -91.18) * mm});
            skLineSegment(sketch, "E1806", {"start": v(-0.77, -91.18) * mm, "end": v(-0.78, -91.35) * mm});
            skLineSegment(sketch, "E1807", {"start": v(-0.78, -91.35) * mm, "end": v(-0.79, -91.53) * mm});
            skLineSegment(sketch, "E1808", {"start": v(-0.79, -91.53) * mm, "end": v(-0.78, -91.7) * mm});
            skLineSegment(sketch, "E1809", {"start": v(-0.78, -91.7) * mm, "end": v(-0.77, -91.87) * mm});
            skLineSegment(sketch, "E1810", {"start": v(-0.77, -91.87) * mm, "end": v(-0.74, -92.02) * mm});
            skLineSegment(sketch, "E1811", {"start": v(-0.74, -92.02) * mm, "end": v(-0.7, -92.15) * mm});
            skLineSegment(sketch, "E1812", {"start": v(-0.7, -92.15) * mm, "end": v(-0.66, -92.28) * mm});
            skLineSegment(sketch, "E1813", {"start": v(-0.66, -92.28) * mm, "end": v(-0.6, -92.4) * mm});
            skLineSegment(sketch, "E1814", {"start": v(-0.6, -92.4) * mm, "end": v(-0.53, -92.5) * mm});
            skLineSegment(sketch, "E1815", {"start": v(-0.53, -92.5) * mm, "end": v(-0.45, -92.6) * mm});
            skLineSegment(sketch, "E1816", {"start": v(-0.45, -92.6) * mm, "end": v(-0.37, -92.67) * mm});
            skLineSegment(sketch, "E1817", {"start": v(-0.37, -92.67) * mm, "end": v(-0.27, -92.73) * mm});
            skLineSegment(sketch, "E1818", {"start": v(-0.27, -92.73) * mm, "end": v(-0.17, -92.78) * mm});
            skLineSegment(sketch, "E1819", {"start": v(-0.17, -92.78) * mm, "end": v(-0.05, -92.81) * mm});
            skLineSegment(sketch, "E1820", {"start": v(-0.05, -92.81) * mm, "end": v(0.08, -92.83) * mm});
            skLineSegment(sketch, "E1821", {"start": v(0.08, -92.83) * mm, "end": v(0.22, -92.84) * mm});
            skLineSegment(sketch, "E1822", {"start": v(0.22, -92.84) * mm, "end": v(0.36, -92.83) * mm});
            skLineSegment(sketch, "E1823", {"start": v(0.36, -92.83) * mm, "end": v(0.48, -92.81) * mm});
            skLineSegment(sketch, "E1824", {"start": v(0.48, -92.81) * mm, "end": v(0.6, -92.78) * mm});
            skLineSegment(sketch, "E1825", {"start": v(0.6, -92.78) * mm, "end": v(0.7, -92.74) * mm});
            skLineSegment(sketch, "E1826", {"start": v(0.7, -92.74) * mm, "end": v(0.8, -92.67) * mm});
            skLineSegment(sketch, "E1827", {"start": v(0.8, -92.67) * mm, "end": v(0.9, -92.6) * mm});
            skLineSegment(sketch, "E1828", {"start": v(0.9, -92.6) * mm, "end": v(0.98, -92.5) * mm});
            skLineSegment(sketch, "E1829", {"start": v(0.98, -92.5) * mm, "end": v(1.05, -92.4) * mm});
            skLineSegment(sketch, "E1830", {"start": v(1.05, -92.4) * mm, "end": v(1.1, -92.3) * mm});
            skLineSegment(sketch, "E1831", {"start": v(1.1, -92.3) * mm, "end": v(1.15, -92.17) * mm});
            skLineSegment(sketch, "E1832", {"start": v(1.15, -92.17) * mm, "end": v(1.19, -92.03) * mm});
            skLineSegment(sketch, "E1833", {"start": v(1.19, -92.03) * mm, "end": v(1.21, -91.88) * mm});
            skLineSegment(sketch, "E1834", {"start": v(1.21, -91.88) * mm, "end": v(1.23, -91.7) * mm});
            skLineSegment(sketch, "E1835", {"start": v(1.23, -91.7) * mm, "end": v(1.24, -91.53) * mm});
            skLineSegment(sketch, "E1836", {"start": v(13.64, -90.2) * mm, "end": v(11.91, -90.44) * mm});
            skLineSegment(sketch, "E1837", {"start": v(13.64, -90.2) * mm, "end": v(13.62, -90.07) * mm});
            skLineSegment(sketch, "E1838", {"start": v(13.62, -90.07) * mm, "end": v(13.6, -89.95) * mm});
            skLineSegment(sketch, "E1839", {"start": v(13.6, -89.95) * mm, "end": v(13.56, -89.85) * mm});
            skLineSegment(sketch, "E1840", {"start": v(13.56, -89.85) * mm, "end": v(13.51, -89.75) * mm});
            skLineSegment(sketch, "E1841", {"start": v(13.51, -89.75) * mm, "end": v(13.46, -89.66) * mm});
            skLineSegment(sketch, "E1842", {"start": v(13.46, -89.66) * mm, "end": v(13.4, -89.57) * mm});
            skLineSegment(sketch, "E1843", {"start": v(13.4, -89.57) * mm, "end": v(13.33, -89.5) * mm});
            skLineSegment(sketch, "E1844", {"start": v(13.33, -89.5) * mm, "end": v(13.26, -89.45) * mm});
            skLineSegment(sketch, "E1845", {"start": v(13.26, -89.45) * mm, "end": v(13.18, -89.4) * mm});
            skLineSegment(sketch, "E1846", {"start": v(13.18, -89.4) * mm, "end": v(13.1, -89.37) * mm});
            skLineSegment(sketch, "E1847", {"start": v(13.1, -89.37) * mm, "end": v(13, -89.34) * mm});
            skLineSegment(sketch, "E1848", {"start": v(13, -89.34) * mm, "end": v(12.9, -89.33) * mm});
            skLineSegment(sketch, "E1849", {"start": v(12.9, -89.33) * mm, "end": v(12.8, -89.33) * mm});
            skLineSegment(sketch, "E1850", {"start": v(12.8, -89.33) * mm, "end": v(12.7, -89.34) * mm});
            skLineSegment(sketch, "E1851", {"start": v(12.7, -89.34) * mm, "end": v(12.58, -89.36) * mm});
            skLineSegment(sketch, "E1852", {"start": v(12.58, -89.36) * mm, "end": v(12.48, -89.39) * mm});
            skLineSegment(sketch, "E1853", {"start": v(12.48, -89.39) * mm, "end": v(12.4, -89.43) * mm});
            skLineSegment(sketch, "E1854", {"start": v(12.4, -89.43) * mm, "end": v(12.3, -89.47) * mm});
            skLineSegment(sketch, "E1855", {"start": v(12.3, -89.47) * mm, "end": v(12.23, -89.53) * mm});
            skLineSegment(sketch, "E1856", {"start": v(12.23, -89.53) * mm, "end": v(12.15, -89.6) * mm});
            skLineSegment(sketch, "E1857", {"start": v(12.15, -89.6) * mm, "end": v(12.1, -89.69) * mm});
            skLineSegment(sketch, "E1858", {"start": v(12.1, -89.69) * mm, "end": v(12.04, -89.77) * mm});
            skLineSegment(sketch, "E1859", {"start": v(12.04, -89.77) * mm, "end": v(12, -89.86) * mm});
            skLineSegment(sketch, "E1860", {"start": v(12, -89.86) * mm, "end": v(11.96, -89.96) * mm});
            skLineSegment(sketch, "E1861", {"start": v(11.96, -89.96) * mm, "end": v(11.94, -90.07) * mm});
            skLineSegment(sketch, "E1862", {"start": v(11.94, -90.07) * mm, "end": v(11.92, -90.19) * mm});
            skLineSegment(sketch, "E1863", {"start": v(11.92, -90.19) * mm, "end": v(11.91, -90.31) * mm});
            skLineSegment(sketch, "E1864", {"start": v(11.91, -90.31) * mm, "end": v(11.91, -90.44) * mm});
            skLineSegment(sketch, "E1865", {"start": v(17.7, -91.15) * mm, "end": v(17.82, -91.12) * mm});
            skLineSegment(sketch, "E1866", {"start": v(17.82, -91.12) * mm, "end": v(17.94, -91.08) * mm});
            skLineSegment(sketch, "E1867", {"start": v(17.94, -91.08) * mm, "end": v(18.03, -91.02) * mm});
            skLineSegment(sketch, "E1868", {"start": v(18.03, -91.02) * mm, "end": v(18.12, -90.96) * mm});
            skLineSegment(sketch, "E1869", {"start": v(18.12, -90.96) * mm, "end": v(18.2, -90.88) * mm});
            skLineSegment(sketch, "E1870", {"start": v(18.2, -90.88) * mm, "end": v(18.27, -90.79) * mm});
            skLineSegment(sketch, "E1871", {"start": v(18.27, -90.79) * mm, "end": v(18.32, -90.68) * mm});
            skLineSegment(sketch, "E1872", {"start": v(18.32, -90.68) * mm, "end": v(18.37, -90.53) * mm});
            skLineSegment(sketch, "E1873", {"start": v(18.37, -90.53) * mm, "end": v(18.4, -90.37) * mm});
            skLineSegment(sketch, "E1874", {"start": v(18.4, -90.37) * mm, "end": v(18.41, -90.18) * mm});
            skLineSegment(sketch, "E1875", {"start": v(18.41, -90.18) * mm, "end": v(18.4, -90.02) * mm});
            skLineSegment(sketch, "E1876", {"start": v(18.4, -90.02) * mm, "end": v(18.39, -89.86) * mm});
            skLineSegment(sketch, "E1877", {"start": v(18.39, -89.86) * mm, "end": v(18.36, -89.68) * mm});
            skLineSegment(sketch, "E1878", {"start": v(18.36, -89.68) * mm, "end": v(18.32, -89.5) * mm});
            skLineSegment(sketch, "E1879", {"start": v(18.32, -89.5) * mm, "end": v(18.28, -89.35) * mm});
            skLineSegment(sketch, "E1880", {"start": v(18.28, -89.35) * mm, "end": v(18.23, -89.2) * mm});
            skLineSegment(sketch, "E1881", {"start": v(18.23, -89.2) * mm, "end": v(18.17, -89.08) * mm});
            skLineSegment(sketch, "E1882", {"start": v(18.17, -89.08) * mm, "end": v(18.1, -88.96) * mm});
            skLineSegment(sketch, "E1883", {"start": v(18.1, -88.96) * mm, "end": v(18.03, -88.85) * mm});
            skLineSegment(sketch, "E1884", {"start": v(18.03, -88.85) * mm, "end": v(17.95, -88.77) * mm});
            skLineSegment(sketch, "E1885", {"start": v(17.95, -88.77) * mm, "end": v(17.87, -88.7) * mm});
            skLineSegment(sketch, "E1886", {"start": v(17.87, -88.7) * mm, "end": v(17.78, -88.64) * mm});
            skLineSegment(sketch, "E1887", {"start": v(17.78, -88.64) * mm, "end": v(17.68, -88.6) * mm});
            skLineSegment(sketch, "E1888", {"start": v(17.68, -88.6) * mm, "end": v(17.57, -88.58) * mm});
            skLineSegment(sketch, "E1889", {"start": v(17.57, -88.58) * mm, "end": v(17.46, -88.56) * mm});
            skLineSegment(sketch, "E1890", {"start": v(17.46, -88.56) * mm, "end": v(17.33, -88.57) * mm});
            skLineSegment(sketch, "E1891", {"start": v(17.33, -88.57) * mm, "end": v(17.2, -88.59) * mm});
            skLineSegment(sketch, "E1892", {"start": v(17.2, -88.59) * mm, "end": v(17.06, -88.62) * mm});
            skLineSegment(sketch, "E1893", {"start": v(17.06, -88.62) * mm, "end": v(16.94, -88.66) * mm});
            skLineSegment(sketch, "E1894", {"start": v(16.94, -88.66) * mm, "end": v(16.83, -88.71) * mm});
            skLineSegment(sketch, "E1895", {"start": v(16.83, -88.71) * mm, "end": v(16.73, -88.77) * mm});
            skLineSegment(sketch, "E1896", {"start": v(16.73, -88.77) * mm, "end": v(16.65, -88.84) * mm});
            skLineSegment(sketch, "E1897", {"start": v(16.65, -88.84) * mm, "end": v(16.58, -88.93) * mm});
            skLineSegment(sketch, "E1898", {"start": v(16.58, -88.93) * mm, "end": v(16.52, -89.02) * mm});
            skLineSegment(sketch, "E1899", {"start": v(16.52, -89.02) * mm, "end": v(16.48, -89.12) * mm});
            skLineSegment(sketch, "E1900", {"start": v(16.48, -89.12) * mm, "end": v(16.45, -89.24) * mm});
            skLineSegment(sketch, "E1901", {"start": v(16.45, -89.24) * mm, "end": v(16.43, -89.36) * mm});
            skLineSegment(sketch, "E1902", {"start": v(16.43, -89.36) * mm, "end": v(16.42, -89.5) * mm});
            skLineSegment(sketch, "E1903", {"start": v(16.42, -89.5) * mm, "end": v(16.43, -89.67) * mm});
            skLineSegment(sketch, "E1904", {"start": v(16.43, -89.67) * mm, "end": v(16.45, -89.85) * mm});
            skLineSegment(sketch, "E1905", {"start": v(16.45, -89.85) * mm, "end": v(16.48, -90.05) * mm});
            skLineSegment(sketch, "E1906", {"start": v(16.48, -90.05) * mm, "end": v(16.52, -90.23) * mm});
            skLineSegment(sketch, "E1907", {"start": v(16.52, -90.23) * mm, "end": v(16.57, -90.4) * mm});
            skLineSegment(sketch, "E1908", {"start": v(16.57, -90.4) * mm, "end": v(16.62, -90.55) * mm});
            skLineSegment(sketch, "E1909", {"start": v(16.62, -90.55) * mm, "end": v(16.68, -90.68) * mm});
            skLineSegment(sketch, "E1910", {"start": v(16.68, -90.68) * mm, "end": v(16.75, -90.8) * mm});
            skLineSegment(sketch, "E1911", {"start": v(16.75, -90.8) * mm, "end": v(16.82, -90.9) * mm});
            skLineSegment(sketch, "E1912", {"start": v(16.82, -90.9) * mm, "end": v(16.9, -91) * mm});
            skLineSegment(sketch, "E1913", {"start": v(16.9, -91) * mm, "end": v(17, -91.06) * mm});
            skLineSegment(sketch, "E1914", {"start": v(17, -91.06) * mm, "end": v(17.08, -91.1) * mm});
            skLineSegment(sketch, "E1915", {"start": v(17.08, -91.1) * mm, "end": v(17.19, -91.14) * mm});
            skLineSegment(sketch, "E1916", {"start": v(17.19, -91.14) * mm, "end": v(17.3, -91.17) * mm});
            skLineSegment(sketch, "E1917", {"start": v(17.3, -91.17) * mm, "end": v(17.42, -91.18) * mm});
            skLineSegment(sketch, "E1918", {"start": v(17.42, -91.18) * mm, "end": v(17.56, -91.17) * mm});
            skLineSegment(sketch, "E1919", {"start": v(17.56, -91.17) * mm, "end": v(17.7, -91.15) * mm});
            skLineSegment(sketch, "E1920", {"start": v(41.83, -80.77) * mm, "end": v(41.71, -80.55) * mm});
            skLineSegment(sketch, "E1921", {"start": v(41.71, -80.55) * mm, "end": v(41.6, -80.34) * mm});
            skLineSegment(sketch, "E1922", {"start": v(41.6, -80.34) * mm, "end": v(41.47, -80.15) * mm});
            skLineSegment(sketch, "E1923", {"start": v(41.47, -80.15) * mm, "end": v(41.36, -80) * mm});
            skLineSegment(sketch, "E1924", {"start": v(41.36, -80) * mm, "end": v(41.24, -79.84) * mm});
            skLineSegment(sketch, "E1925", {"start": v(41.24, -79.84) * mm, "end": v(41.11, -79.72) * mm});
            skLineSegment(sketch, "E1926", {"start": v(41.11, -79.72) * mm, "end": v(41, -79.62) * mm});
            skLineSegment(sketch, "E1927", {"start": v(41, -79.62) * mm, "end": v(40.88, -79.55) * mm});
            skLineSegment(sketch, "E1928", {"start": v(40.88, -79.55) * mm, "end": v(40.76, -79.5) * mm});
            skLineSegment(sketch, "E1929", {"start": v(40.76, -79.5) * mm, "end": v(40.65, -79.47) * mm});
            skLineSegment(sketch, "E1930", {"start": v(40.65, -79.47) * mm, "end": v(40.53, -79.45) * mm});
            skLineSegment(sketch, "E1931", {"start": v(40.53, -79.45) * mm, "end": v(40.4, -79.46) * mm});
            skLineSegment(sketch, "E1932", {"start": v(40.4, -79.46) * mm, "end": v(40.27, -79.5) * mm});
            skLineSegment(sketch, "E1933", {"start": v(40.27, -79.5) * mm, "end": v(40.14, -79.55) * mm});
            skLineSegment(sketch, "E1934", {"start": v(40.14, -79.55) * mm, "end": v(40.02, -79.62) * mm});
            skLineSegment(sketch, "E1935", {"start": v(40.02, -79.62) * mm, "end": v(39.92, -79.7) * mm});
            skLineSegment(sketch, "E1936", {"start": v(39.92, -79.7) * mm, "end": v(39.84, -79.8) * mm});
            skLineSegment(sketch, "E1937", {"start": v(39.84, -79.8) * mm, "end": v(39.78, -79.9) * mm});
            skLineSegment(sketch, "E1938", {"start": v(39.78, -79.9) * mm, "end": v(39.73, -80) * mm});
            skLineSegment(sketch, "E1939", {"start": v(39.73, -80) * mm, "end": v(39.7, -80.14) * mm});
            skLineSegment(sketch, "E1940", {"start": v(39.7, -80.14) * mm, "end": v(39.69, -80.28) * mm});
            skLineSegment(sketch, "E1941", {"start": v(39.69, -80.28) * mm, "end": v(39.7, -80.42) * mm});
            skLineSegment(sketch, "E1942", {"start": v(39.7, -80.42) * mm, "end": v(39.72, -80.58) * mm});
            skLineSegment(sketch, "E1943", {"start": v(39.72, -80.58) * mm, "end": v(39.76, -80.76) * mm});
            skLineSegment(sketch, "E1944", {"start": v(39.76, -80.76) * mm, "end": v(39.82, -80.95) * mm});
            skLineSegment(sketch, "E1945", {"start": v(39.82, -80.95) * mm, "end": v(39.9, -81.16) * mm});
            skLineSegment(sketch, "E1946", {"start": v(39.9, -81.16) * mm, "end": v(40, -81.4) * mm});
            skLineSegment(sketch, "E1947", {"start": v(40, -81.4) * mm, "end": v(40.12, -81.64) * mm});
            skLineSegment(sketch, "E1948", {"start": v(40.12, -81.64) * mm, "end": v(40.25, -81.87) * mm});
            skLineSegment(sketch, "E1949", {"start": v(40.25, -81.87) * mm, "end": v(40.37, -82.08) * mm});
            skLineSegment(sketch, "E1950", {"start": v(40.37, -82.08) * mm, "end": v(40.49, -82.27) * mm});
            skLineSegment(sketch, "E1951", {"start": v(40.49, -82.27) * mm, "end": v(40.6, -82.43) * mm});
            skLineSegment(sketch, "E1952", {"start": v(40.6, -82.43) * mm, "end": v(40.73, -82.58) * mm});
            skLineSegment(sketch, "E1953", {"start": v(40.73, -82.58) * mm, "end": v(40.85, -82.7) * mm});
            skLineSegment(sketch, "E1954", {"start": v(40.85, -82.7) * mm, "end": v(40.97, -82.8) * mm});
            skLineSegment(sketch, "E1955", {"start": v(40.97, -82.8) * mm, "end": v(41.08, -82.87) * mm});
            skLineSegment(sketch, "E1956", {"start": v(41.08, -82.87) * mm, "end": v(41.2, -82.93) * mm});
            skLineSegment(sketch, "E1957", {"start": v(41.2, -82.93) * mm, "end": v(41.32, -82.96) * mm});
            skLineSegment(sketch, "E1958", {"start": v(41.32, -82.96) * mm, "end": v(41.44, -82.97) * mm});
            skLineSegment(sketch, "E1959", {"start": v(41.44, -82.97) * mm, "end": v(41.56, -82.96) * mm});
            skLineSegment(sketch, "E1960", {"start": v(41.56, -82.96) * mm, "end": v(41.69, -82.92) * mm});
            skLineSegment(sketch, "E1961", {"start": v(41.69, -82.92) * mm, "end": v(41.82, -82.87) * mm});
            skLineSegment(sketch, "E1962", {"start": v(41.82, -82.87) * mm, "end": v(41.94, -82.8) * mm});
            skLineSegment(sketch, "E1963", {"start": v(41.94, -82.8) * mm, "end": v(42.04, -82.72) * mm});
            skLineSegment(sketch, "E1964", {"start": v(42.04, -82.72) * mm, "end": v(42.12, -82.63) * mm});
            skLineSegment(sketch, "E1965", {"start": v(42.12, -82.63) * mm, "end": v(42.18, -82.53) * mm});
            skLineSegment(sketch, "E1966", {"start": v(42.18, -82.53) * mm, "end": v(42.23, -82.4) * mm});
            skLineSegment(sketch, "E1967", {"start": v(42.23, -82.4) * mm, "end": v(42.26, -82.28) * mm});
            skLineSegment(sketch, "E1968", {"start": v(42.26, -82.28) * mm, "end": v(42.27, -82.14) * mm});
            skLineSegment(sketch, "E1969", {"start": v(42.27, -82.14) * mm, "end": v(42.26, -81.99) * mm});
            skLineSegment(sketch, "E1970", {"start": v(42.26, -81.99) * mm, "end": v(42.24, -81.83) * mm});
            skLineSegment(sketch, "E1971", {"start": v(42.24, -81.83) * mm, "end": v(42.2, -81.65) * mm});
            skLineSegment(sketch, "E1972", {"start": v(42.2, -81.65) * mm, "end": v(42.13, -81.46) * mm});
            skLineSegment(sketch, "E1973", {"start": v(42.13, -81.46) * mm, "end": v(42.05, -81.25) * mm});
            skLineSegment(sketch, "E1974", {"start": v(42.05, -81.25) * mm, "end": v(41.95, -81.02) * mm});
            skLineSegment(sketch, "E1975", {"start": v(41.95, -81.02) * mm, "end": v(41.83, -80.77) * mm});
            skLineSegment(sketch, "E1976", {"start": v(-21.17, -87.32) * mm, "end": v(-20.65, -87.36) * mm});
            skLineSegment(sketch, "E1977", {"start": v(-20.65, -87.36) * mm, "end": v(-20.04, -87.66) * mm});
            skLineSegment(sketch, "E1978", {"start": v(-20.04, -87.66) * mm, "end": v(-19.75, -88.08) * mm});
            skLineSegment(sketch, "E1979", {"start": v(-19.7, -88.09) * mm, "end": v(-19.75, -88.08) * mm});
            skLineSegment(sketch, "E1980", {"start": v(-19.67, -87.85) * mm, "end": v(-19.7, -88.09) * mm});
            skLineSegment(sketch, "E1981", {"start": v(-19.63, -87.62) * mm, "end": v(-19.67, -87.85) * mm});
            skLineSegment(sketch, "E1982", {"start": v(-19.32, -86.3) * mm, "end": v(-19.63, -87.62) * mm});
            skLineSegment(sketch, "E1983", {"start": v(-18.83, -86.4) * mm, "end": v(-19.32, -86.3) * mm});
            skLineSegment(sketch, "E1984", {"start": v(-10.78, -91.57) * mm, "end": v(-10.55, -89.62) * mm});
            skLineSegment(sketch, "E1985", {"start": v(-10.78, -91.57) * mm, "end": v(-10.77, -91.87) * mm});
            skLineSegment(sketch, "E1986", {"start": v(-10.77, -91.87) * mm, "end": v(-10.7, -92.05) * mm});
            skLineSegment(sketch, "E1987", {"start": v(-10.7, -92.05) * mm, "end": v(-10.52, -92.2) * mm});
            skLineSegment(sketch, "E1988", {"start": v(-10.52, -92.2) * mm, "end": v(-10.32, -92.26) * mm});
            skLineSegment(sketch, "E1989", {"start": v(-10.32, -92.26) * mm, "end": v(-10.17, -92.27) * mm});
            skLineSegment(sketch, "E1990", {"start": v(-10.17, -92.27) * mm, "end": v(-10.06, -92.27) * mm});
            skLineSegment(sketch, "E1991", {"start": v(-10.06, -92.27) * mm, "end": v(-9.94, -92.26) * mm});
            skLineSegment(sketch, "E1992", {"start": v(-9.94, -92.26) * mm, "end": v(-9.86, -92.25) * mm});
            skLineSegment(sketch, "E1993", {"start": v(-9.9, -92.64) * mm, "end": v(-9.86, -92.25) * mm});
            skLineSegment(sketch, "E1994", {"start": v(-9.9, -92.64) * mm, "end": v(-10.02, -92.66) * mm});
            skLineSegment(sketch, "E1995", {"start": v(-10.02, -92.66) * mm, "end": v(-10.15, -92.67) * mm});
            skLineSegment(sketch, "E1996", {"start": v(-10.15, -92.67) * mm, "end": v(-10.32, -92.67) * mm});
            skLineSegment(sketch, "E1997", {"start": v(-10.32, -92.67) * mm, "end": v(-10.44, -92.67) * mm});
            skLineSegment(sketch, "E1998", {"start": v(-10.44, -92.67) * mm, "end": v(-11.18, -92.26) * mm});
            skLineSegment(sketch, "E1999", {"start": v(-11.18, -92.26) * mm, "end": v(-11.29, -91.54) * mm});
            skLineSegment(sketch, "E2000", {"start": v(-11.05, -89.56) * mm, "end": v(-11.29, -91.54) * mm});
            skLineSegment(sketch, "E2001", {"start": v(-11.53, -89.5) * mm, "end": v(-11.05, -89.56) * mm});
            skLineSegment(sketch, "E2002", {"start": v(-11.5, -89.26) * mm, "end": v(-11.53, -89.5) * mm});
            skLineSegment(sketch, "E2003", {"start": v(-11, -89.1) * mm, "end": v(-11.5, -89.26) * mm});
            skLineSegment(sketch, "E2004", {"start": v(-10.7, -88.43) * mm, "end": v(-11, -89.1) * mm});
            skLineSegment(sketch, "E2005", {"start": v(-10.41, -88.46) * mm, "end": v(-10.7, -88.43) * mm});
            skLineSegment(sketch, "E2006", {"start": v(-10.5, -89.23) * mm, "end": v(-10.41, -88.46) * mm});
            skLineSegment(sketch, "E2007", {"start": v(-9.54, -89.34) * mm, "end": v(-10.5, -89.23) * mm});
            skLineSegment(sketch, "E2008", {"start": v(-9.59, -89.73) * mm, "end": v(-9.54, -89.34) * mm});
            skLineSegment(sketch, "E2009", {"start": v(-10.55, -89.62) * mm, "end": v(-9.59, -89.73) * mm});
            skLineSegment(sketch, "E2010", {"start": v(-3, -91.25) * mm, "end": v(-2.99, -90.8) * mm});
            skLineSegment(sketch, "E2011", {"start": v(-4.86, -91.16) * mm, "end": v(-3, -91.25) * mm});
            skLineSegment(sketch, "E2012", {"start": v(-4.95, -93.07) * mm, "end": v(-4.86, -91.16) * mm});
            skLineSegment(sketch, "E2013", {"start": v(-5.47, -93.04) * mm, "end": v(-4.95, -93.07) * mm});
            skLineSegment(sketch, "E2014", {"start": v(-5.25, -88.59) * mm, "end": v(-5.47, -93.04) * mm});
            skLineSegment(sketch, "E2015", {"start": v(-2.77, -88.7) * mm, "end": v(-5.25, -88.59) * mm});
            skLineSegment(sketch, "E2016", {"start": v(-2.8, -89.17) * mm, "end": v(-2.77, -88.7) * mm});
            skLineSegment(sketch, "E2017", {"start": v(-4.76, -89.07) * mm, "end": v(-2.8, -89.17) * mm});
            skLineSegment(sketch, "E2018", {"start": v(-4.83, -90.7) * mm, "end": v(-4.76, -89.07) * mm});
            skLineSegment(sketch, "E2019", {"start": v(-2.99, -90.8) * mm, "end": v(-4.83, -90.7) * mm});
            skLineSegment(sketch, "E2020", {"start": v(3.91, -90.4) * mm, "end": v(3.89, -90.4) * mm});
            skLineSegment(sketch, "E2021", {"start": v(3.91, -90.4) * mm, "end": v(4.13, -90.07) * mm});
            skLineSegment(sketch, "E2022", {"start": v(4.13, -90.07) * mm, "end": v(4.34, -89.88) * mm});
            skLineSegment(sketch, "E2023", {"start": v(4.34, -89.88) * mm, "end": v(4.64, -89.72) * mm});
            skLineSegment(sketch, "E2024", {"start": v(4.64, -89.72) * mm, "end": v(4.9, -89.67) * mm});
            skLineSegment(sketch, "E2025", {"start": v(4.9, -89.67) * mm, "end": v(5.14, -89.67) * mm});
            skLineSegment(sketch, "E2026", {"start": v(5.14, -89.67) * mm, "end": v(5.3, -89.7) * mm});
            skLineSegment(sketch, "E2027", {"start": v(5.26, -90.16) * mm, "end": v(5.3, -89.7) * mm});
            skLineSegment(sketch, "E2028", {"start": v(5.26, -90.16) * mm, "end": v(5.04, -90.14) * mm});
            skLineSegment(sketch, "E2029", {"start": v(5.04, -90.14) * mm, "end": v(4.9, -90.13) * mm});
            skLineSegment(sketch, "E2030", {"start": v(4.9, -90.13) * mm, "end": v(4.48, -90.26) * mm});
            skLineSegment(sketch, "E2031", {"start": v(4.48, -90.26) * mm, "end": v(4.21, -90.5) * mm});
            skLineSegment(sketch, "E2032", {"start": v(4.21, -90.5) * mm, "end": v(4, -90.93) * mm});
            skLineSegment(sketch, "E2033", {"start": v(4, -90.93) * mm, "end": v(3.96, -91.33) * mm});
            skLineSegment(sketch, "E2034", {"start": v(4.05, -93.12) * mm, "end": v(3.96, -91.33) * mm});
            skLineSegment(sketch, "E2035", {"start": v(3.54, -93.14) * mm, "end": v(4.05, -93.12) * mm});
            skLineSegment(sketch, "E2036", {"start": v(3.38, -89.8) * mm, "end": v(3.54, -93.14) * mm});
            skLineSegment(sketch, "E2037", {"start": v(3.8, -89.79) * mm, "end": v(3.38, -89.8) * mm});
            skLineSegment(sketch, "E2038", {"start": v(3.89, -90.4) * mm, "end": v(3.8, -89.79) * mm});
            skLineSegment(sketch, "E2039", {"start": v(14.3, -91.96) * mm, "end": v(14.23, -91.51) * mm});
            skLineSegment(sketch, "E2040", {"start": v(14.3, -91.96) * mm, "end": v(14.02, -92.11) * mm});
            skLineSegment(sketch, "E2041", {"start": v(14.02, -92.11) * mm, "end": v(13.82, -92.2) * mm});
            skLineSegment(sketch, "E2042", {"start": v(13.82, -92.2) * mm, "end": v(13.53, -92.28) * mm});
            skLineSegment(sketch, "E2043", {"start": v(13.53, -92.28) * mm, "end": v(13.25, -92.33) * mm});
            skLineSegment(sketch, "E2044", {"start": v(13.25, -92.33) * mm, "end": v(12.5, -92.3) * mm});
            skLineSegment(sketch, "E2045", {"start": v(12.5, -92.3) * mm, "end": v(12.03, -92.05) * mm});
            skLineSegment(sketch, "E2046", {"start": v(12.03, -92.05) * mm, "end": v(11.6, -91.48) * mm});
            skLineSegment(sketch, "E2047", {"start": v(11.6, -91.48) * mm, "end": v(11.43, -90.86) * mm});
            skLineSegment(sketch, "E2048", {"start": v(11.43, -90.86) * mm, "end": v(11.44, -90.05) * mm});
            skLineSegment(sketch, "E2049", {"start": v(11.44, -90.05) * mm, "end": v(11.64, -89.54) * mm});
            skLineSegment(sketch, "E2050", {"start": v(11.64, -89.54) * mm, "end": v(12.12, -89.08) * mm});
            skLineSegment(sketch, "E2051", {"start": v(12.12, -89.08) * mm, "end": v(12.64, -88.91) * mm});
            skLineSegment(sketch, "E2052", {"start": v(12.64, -88.91) * mm, "end": v(13.27, -88.96) * mm});
            skLineSegment(sketch, "E2053", {"start": v(13.27, -88.96) * mm, "end": v(13.68, -89.18) * mm});
            skLineSegment(sketch, "E2054", {"start": v(13.68, -89.18) * mm, "end": v(14.05, -89.68) * mm});
            skLineSegment(sketch, "E2055", {"start": v(14.05, -89.68) * mm, "end": v(14.2, -90.21) * mm});
            skLineSegment(sketch, "E2056", {"start": v(14.24, -90.53) * mm, "end": v(14.2, -90.21) * mm});
            skLineSegment(sketch, "E2057", {"start": v(11.96, -90.85) * mm, "end": v(14.24, -90.53) * mm});
            skLineSegment(sketch, "E2058", {"start": v(11.96, -90.85) * mm, "end": v(12.14, -91.4) * mm});
            skLineSegment(sketch, "E2059", {"start": v(12.14, -91.4) * mm, "end": v(12.38, -91.7) * mm});
            skLineSegment(sketch, "E2060", {"start": v(12.38, -91.7) * mm, "end": v(12.8, -91.89) * mm});
            skLineSegment(sketch, "E2061", {"start": v(12.8, -91.89) * mm, "end": v(13.2, -91.89) * mm});
            skLineSegment(sketch, "E2062", {"start": v(13.2, -91.89) * mm, "end": v(13.8, -91.73) * mm});
            skLineSegment(sketch, "E2063", {"start": v(13.8, -91.73) * mm, "end": v(14.23, -91.51) * mm});
            skLineSegment(sketch, "E2064", {"start": v(26.82, -85.77) * mm, "end": v(27.83, -88.96) * mm});
            skLineSegment(sketch, "E2065", {"start": v(27.3, -85.62) * mm, "end": v(26.82, -85.77) * mm});
            skLineSegment(sketch, "E2066", {"start": v(28.31, -88.8) * mm, "end": v(27.3, -85.62) * mm});
            skLineSegment(sketch, "E2067", {"start": v(27.83, -88.96) * mm, "end": v(28.31, -88.8) * mm});
            skLineSegment(sketch, "E2068", {"start": v(36.93, -85.07) * mm, "end": v(36.92, -85.05) * mm});
            skLineSegment(sketch, "E2069", {"start": v(39.02, -84.14) * mm, "end": v(36.93, -85.07) * mm});
            skLineSegment(sketch, "E2070", {"start": v(39.21, -84.56) * mm, "end": v(39.02, -84.14) * mm});
            skLineSegment(sketch, "E2071", {"start": v(36.53, -85.76) * mm, "end": v(39.21, -84.56) * mm});
            skLineSegment(sketch, "E2072", {"start": v(36.36, -85.36) * mm, "end": v(36.53, -85.76) * mm});
            skLineSegment(sketch, "E2073", {"start": v(36.95, -83.8) * mm, "end": v(36.36, -85.36) * mm});
            skLineSegment(sketch, "E2074", {"start": v(36.95, -83.8) * mm, "end": v(37.18, -83.14) * mm});
            skLineSegment(sketch, "E2075", {"start": v(37.18, -83.14) * mm, "end": v(37.28, -82.8) * mm});
            skLineSegment(sketch, "E2076", {"start": v(37.28, -82.8) * mm, "end": v(37.32, -82.5) * mm});
            skLineSegment(sketch, "E2077", {"start": v(37.32, -82.5) * mm, "end": v(37.33, -82.3) * mm});
            skLineSegment(sketch, "E2078", {"start": v(37.33, -82.3) * mm, "end": v(37.29, -82.03) * mm});
            skLineSegment(sketch, "E2079", {"start": v(37.29, -82.03) * mm, "end": v(37.21, -81.82) * mm});
            skLineSegment(sketch, "E2080", {"start": v(37.21, -81.82) * mm, "end": v(37, -81.53) * mm});
            skLineSegment(sketch, "E2081", {"start": v(37, -81.53) * mm, "end": v(36.78, -81.4) * mm});
            skLineSegment(sketch, "E2082", {"start": v(36.78, -81.4) * mm, "end": v(36.44, -81.36) * mm});
            skLineSegment(sketch, "E2083", {"start": v(36.44, -81.36) * mm, "end": v(36.15, -81.45) * mm});
            skLineSegment(sketch, "E2084", {"start": v(36.15, -81.45) * mm, "end": v(35.89, -81.6) * mm});
            skLineSegment(sketch, "E2085", {"start": v(35.89, -81.6) * mm, "end": v(35.7, -81.75) * mm});
            skLineSegment(sketch, "E2086", {"start": v(35.7, -81.75) * mm, "end": v(35.5, -82) * mm});
            skLineSegment(sketch, "E2087", {"start": v(35.5, -82) * mm, "end": v(35.34, -82.28) * mm});
            skLineSegment(sketch, "E2088", {"start": v(34.95, -82.07) * mm, "end": v(35.34, -82.28) * mm});
            skLineSegment(sketch, "E2089", {"start": v(34.95, -82.07) * mm, "end": v(35.44, -81.4) * mm});
            skLineSegment(sketch, "E2090", {"start": v(35.44, -81.4) * mm, "end": v(35.97, -81.06) * mm});
            skLineSegment(sketch, "E2091", {"start": v(35.97, -81.06) * mm, "end": v(36.57, -80.9) * mm});
            skLineSegment(sketch, "E2092", {"start": v(36.57, -80.9) * mm, "end": v(37, -80.95) * mm});
            skLineSegment(sketch, "E2093", {"start": v(37, -80.95) * mm, "end": v(37.44, -81.22) * mm});
            skLineSegment(sketch, "E2094", {"start": v(37.44, -81.22) * mm, "end": v(37.68, -81.6) * mm});
            skLineSegment(sketch, "E2095", {"start": v(37.68, -81.6) * mm, "end": v(37.8, -82.06) * mm});
            skLineSegment(sketch, "E2096", {"start": v(37.8, -82.06) * mm, "end": v(37.8, -82.46) * mm});
            skLineSegment(sketch, "E2097", {"start": v(37.8, -82.46) * mm, "end": v(37.66, -83.1) * mm});
            skLineSegment(sketch, "E2098", {"start": v(37.66, -83.1) * mm, "end": v(37.42, -83.78) * mm});
            skLineSegment(sketch, "E2099", {"start": v(36.92, -85.05) * mm, "end": v(37.42, -83.78) * mm});
            skLineSegment(sketch, "E2100", {"start": v(47.92, -75.17) * mm, "end": v(47.7, -74.82) * mm});
            skLineSegment(sketch, "E2101", {"start": v(48.5, -79.57) * mm, "end": v(47.92, -75.17) * mm});
            skLineSegment(sketch, "E2102", {"start": v(48.02, -79.87) * mm, "end": v(48.5, -79.57) * mm});
            skLineSegment(sketch, "E2103", {"start": v(47.5, -75.5) * mm, "end": v(48.02, -79.87) * mm});
            skLineSegment(sketch, "E2104", {"start": v(45.42, -76.78) * mm, "end": v(47.5, -75.5) * mm});
            skLineSegment(sketch, "E2105", {"start": v(45.18, -76.38) * mm, "end": v(45.42, -76.78) * mm});
            skLineSegment(sketch, "E2106", {"start": v(47.7, -74.82) * mm, "end": v(45.18, -76.38) * mm});
            skLineSegment(sketch, "E2107", {"start": v(43.7, -77.23) * mm, "end": v(43.11, -78.6) * mm});
            skLineSegment(sketch, "E2108", {"start": v(44.07, -77.02) * mm, "end": v(43.7, -77.23) * mm});
            skLineSegment(sketch, "E2109", {"start": v(46.25, -80.9) * mm, "end": v(44.07, -77.02) * mm});
            skLineSegment(sketch, "E2110", {"start": v(45.82, -81.15) * mm, "end": v(46.25, -80.9) * mm});
            skLineSegment(sketch, "E2111", {"start": v(44.26, -78.38) * mm, "end": v(45.82, -81.15) * mm});
            skLineSegment(sketch, "E2112", {"start": v(44.26, -78.38) * mm, "end": v(44.06, -78) * mm});
            skLineSegment(sketch, "E2113", {"start": v(44.06, -78) * mm, "end": v(43.92, -77.71) * mm});
            skLineSegment(sketch, "E2114", {"start": v(43.92, -77.71) * mm, "end": v(43.89, -77.81) * mm});
            skLineSegment(sketch, "E2115", {"start": v(43.89, -77.81) * mm, "end": v(43.86, -77.9) * mm});
            skLineSegment(sketch, "E2116", {"start": v(-32.54, -84.27) * mm, "end": v(-32.53, -84.42) * mm});
            skLineSegment(sketch, "E2117", {"start": v(43.86, -77.9) * mm, "end": v(43.74, -78.22) * mm});
            skLineSegment(sketch, "E2118", {"start": v(-32.53, -84.42) * mm, "end": v(-32.56, -84.63) * mm});
            skLineSegment(sketch, "E2119", {"start": v(43.74, -78.22) * mm, "end": v(43.52, -78.77) * mm});
            skLineSegment(sketch, "E2120", {"start": v(-32.56, -84.63) * mm, "end": v(-32.62, -84.8) * mm});
            skLineSegment(sketch, "E2121", {"start": v(43.11, -78.6) * mm, "end": v(43.52, -78.77) * mm});
            skLineSegment(sketch, "E2122", {"start": v(-32.62, -84.8) * mm, "end": v(-32.9, -85.22) * mm});
            skLineSegment(sketch, "E2123", {"start": v(-46.3, 79.27) * mm, "end": v(-44.58, 80.24) * mm});
            skLineSegment(sketch, "E2124", {"start": v(-32.9, -85.22) * mm, "end": v(-33.22, -85.4) * mm});
            skLineSegment(sketch, "E2125", {"start": v(-46.53, 79.68) * mm, "end": v(-46.3, 79.27) * mm});
            skLineSegment(sketch, "E2126", {"start": v(-33.22, -85.4) * mm, "end": v(-33.73, -85.46) * mm});
            skLineSegment(sketch, "E2127", {"start": v(-44.36, 80.9) * mm, "end": v(-46.53, 79.68) * mm});
            skLineSegment(sketch, "E2128", {"start": v(-33.73, -85.46) * mm, "end": v(-34.18, -85.34) * mm});
            skLineSegment(sketch, "E2129", {"start": v(-42.17, 77.01) * mm, "end": v(-44.36, 80.9) * mm});
            skLineSegment(sketch, "E2130", {"start": v(-34.18, -85.34) * mm, "end": v(-34.33, -85.27) * mm});
            skLineSegment(sketch, "E2131", {"start": v(-42.62, 76.76) * mm, "end": v(-42.17, 77.01) * mm});
            skLineSegment(sketch, "E2132", {"start": v(-34.33, -85.27) * mm, "end": v(-34.43, -85.2) * mm});
            skLineSegment(sketch, "E2133", {"start": v(-44.58, 80.24) * mm, "end": v(-42.62, 76.76) * mm});
            skLineSegment(sketch, "E2134", {"start": v(-34.43, -85.2) * mm, "end": v(-34.76, -85.31) * mm});
            skCircle(sketch, "E2135", {"center": v(0.1, -0.48) * mm, "radius": 104.25 * mm});
            skLineSegment(sketch, "E2136", {"start": v(-34.76, -85.31) * mm, "end": v(-34.9, -85.49) * mm});
            skLineSegment(sketch, "E2137", {"start": v(39.67, -81.87) * mm, "end": v(39.26, -80.83) * mm});
            skLineSegment(sketch, "E2138", {"start": v(-34.9, -85.49) * mm, "end": v(-34.91, -85.62) * mm});
            skLineSegment(sketch, "E2139", {"start": v(39.26, -80.83) * mm, "end": v(39.2, -80.17) * mm});
            skLineSegment(sketch, "E2140", {"start": v(-34.91, -85.62) * mm, "end": v(-34.87, -85.72) * mm});
            skLineSegment(sketch, "E2141", {"start": v(39.2, -80.17) * mm, "end": v(39.47, -79.52) * mm});
            skLineSegment(sketch, "E2142", {"start": v(-34.87, -85.72) * mm, "end": v(-34.72, -85.83) * mm});
            skLineSegment(sketch, "E2143", {"start": v(39.47, -79.52) * mm, "end": v(39.94, -79.16) * mm});
            skLineSegment(sketch, "E2144", {"start": v(-34.72, -85.83) * mm, "end": v(-34.53, -85.92) * mm});
            skLineSegment(sketch, "E2145", {"start": v(39.94, -79.16) * mm, "end": v(40.65, -79) * mm});
            skLineSegment(sketch, "E2146", {"start": v(-33.98, -86.14) * mm, "end": v(-34.53, -85.92) * mm});
            skLineSegment(sketch, "E2147", {"start": v(40.65, -79) * mm, "end": v(41.2, -79.19) * mm});
            skLineSegment(sketch, "E2148", {"start": v(-33.98, -86.14) * mm, "end": v(-33.52, -86.4) * mm});
            skLineSegment(sketch, "E2149", {"start": v(41.2, -79.19) * mm, "end": v(41.83, -79.79) * mm});
            skLineSegment(sketch, "E2150", {"start": v(-33.52, -86.4) * mm, "end": v(-33.3, -86.67) * mm});
            skLineSegment(sketch, "E2151", {"start": v(41.83, -79.79) * mm, "end": v(42.3, -80.54) * mm});
            skLineSegment(sketch, "E2152", {"start": v(-33.3, -86.67) * mm, "end": v(-33.2, -87.05) * mm});
            skLineSegment(sketch, "E2153", {"start": v(42.3, -80.54) * mm, "end": v(42.7, -81.58) * mm});
            skLineSegment(sketch, "E2154", {"start": v(-33.2, -87.05) * mm, "end": v(-33.27, -87.4) * mm});
            skLineSegment(sketch, "E2155", {"start": v(42.7, -81.58) * mm, "end": v(42.75, -82.24) * mm});
            skLineSegment(sketch, "E2156", {"start": v(-33.27, -87.4) * mm, "end": v(-33.6, -87.84) * mm});
            skLineSegment(sketch, "E2157", {"start": v(42.75, -82.24) * mm, "end": v(42.49, -82.9) * mm});
            skLineSegment(sketch, "E2158", {"start": v(-33.6, -87.84) * mm, "end": v(-34, -88.01) * mm});
            skLineSegment(sketch, "E2159", {"start": v(42.49, -82.9) * mm, "end": v(42.02, -83.26) * mm});
            skLineSegment(sketch, "E2160", {"start": v(-34, -88.01) * mm, "end": v(-34.67, -88) * mm});
            skLineSegment(sketch, "E2161", {"start": v(42.02, -83.26) * mm, "end": v(41.31, -83.41) * mm});
            skLineSegment(sketch, "E2162", {"start": v(-34.67, -88) * mm, "end": v(-35.31, -87.8) * mm});
            skLineSegment(sketch, "E2163", {"start": v(41.31, -83.41) * mm, "end": v(40.78, -83.23) * mm});
            skLineSegment(sketch, "E2164", {"start": v(-35.31, -87.8) * mm, "end": v(-35.88, -87.49) * mm});
            skLineSegment(sketch, "E2165", {"start": v(40.78, -83.23) * mm, "end": v(40.13, -82.63) * mm});
            skLineSegment(sketch, "E2166", {"start": v(-35.88, -87.49) * mm, "end": v(-36.16, -87.2) * mm});
            skLineSegment(sketch, "E2167", {"start": v(40.13, -82.63) * mm, "end": v(39.67, -81.87) * mm});
            skLineSegment(sketch, "E2168", {"start": v(-36.16, -87.2) * mm, "end": v(-36.3, -86.78) * mm});
            skLineSegment(sketch, "E2169", {"start": v(22.2, -90.6) * mm, "end": v(21.6, -90.65) * mm});
            skLineSegment(sketch, "E2170", {"start": v(-36.3, -86.78) * mm, "end": v(-36.23, -86.42) * mm});
            skLineSegment(sketch, "E2171", {"start": v(21.6, -90.65) * mm, "end": v(21.24, -90.53) * mm});
            skLineSegment(sketch, "E2172", {"start": v(-36.23, -86.42) * mm, "end": v(-36.06, -86.15) * mm});
            skLineSegment(sketch, "E2173", {"start": v(21.24, -90.53) * mm, "end": v(20.9, -90.17) * mm});
            skLineSegment(sketch, "E2174", {"start": v(-36.06, -86.15) * mm, "end": v(-35.86, -86) * mm});
            skLineSegment(sketch, "E2175", {"start": v(20.9, -90.17) * mm, "end": v(20.72, -89.7) * mm});
            skLineSegment(sketch, "E2176", {"start": v(-35.86, -86) * mm, "end": v(-35.53, -85.92) * mm});
            skLineSegment(sketch, "E2177", {"start": v(20.2, -87.58) * mm, "end": v(20.72, -89.7) * mm});
            skLineSegment(sketch, "E2178", {"start": v(-35.53, -85.92) * mm, "end": v(-35.23, -85.93) * mm});
            skLineSegment(sketch, "E2179", {"start": v(20.7, -87.46) * mm, "end": v(20.2, -87.58) * mm});
            skLineSegment(sketch, "E2180", {"start": v(-35.23, -85.93) * mm, "end": v(-35.32, -85.8) * mm});
            skLineSegment(sketch, "E2181", {"start": v(21.22, -89.57) * mm, "end": v(20.7, -87.46) * mm});
            skLineSegment(sketch, "E2182", {"start": v(-35.32, -85.8) * mm, "end": v(-35.37, -85.68) * mm});
            skLineSegment(sketch, "E2183", {"start": v(21.22, -89.57) * mm, "end": v(21.37, -89.93) * mm});
            skLineSegment(sketch, "E2184", {"start": v(-35.37, -85.68) * mm, "end": v(-35.38, -85.52) * mm});
            skLineSegment(sketch, "E2185", {"start": v(21.37, -89.93) * mm, "end": v(21.54, -90.11) * mm});
            skLineSegment(sketch, "E2186", {"start": v(-35.38, -85.52) * mm, "end": v(-35.34, -85.39) * mm});
            skLineSegment(sketch, "E2187", {"start": v(21.54, -90.11) * mm, "end": v(21.85, -90.2) * mm});
            skLineSegment(sketch, "E2188", {"start": v(-35.34, -85.39) * mm, "end": v(-35.24, -85.22) * mm});
            skLineSegment(sketch, "E2189", {"start": v(21.85, -90.2) * mm, "end": v(22.16, -90.17) * mm});
            skLineSegment(sketch, "E2190", {"start": v(-35.24, -85.22) * mm, "end": v(-35.13, -85.13) * mm});
            skLineSegment(sketch, "E2191", {"start": v(22.16, -90.17) * mm, "end": v(22.62, -89.96) * mm});
            skLineSegment(sketch, "E2192", {"start": v(-35.13, -85.13) * mm, "end": v(-34.94, -85.04) * mm});
            skLineSegment(sketch, "E2193", {"start": v(22.62, -89.96) * mm, "end": v(22.83, -89.7) * mm});
            skLineSegment(sketch, "E2194", {"start": v(-34.94, -85.04) * mm, "end": v(-34.75, -85) * mm});
            skLineSegment(sketch, "E2195", {"start": v(22.83, -89.7) * mm, "end": v(22.92, -89.24) * mm});
            skLineSegment(sketch, "E2196", {"start": v(-34.75, -85) * mm, "end": v(-34.93, -84.74) * mm});
            skLineSegment(sketch, "E2197", {"start": v(22.92, -89.24) * mm, "end": v(22.84, -88.74) * mm});
            skLineSegment(sketch, "E2198", {"start": v(-34.93, -84.74) * mm, "end": v(-35, -84.5) * mm});
            skLineSegment(sketch, "E2199", {"start": v(22.42, -87.03) * mm, "end": v(22.84, -88.74) * mm});
            skLineSegment(sketch, "E2200", {"start": v(-35, -84.5) * mm, "end": v(-35, -84.16) * mm});
            skLineSegment(sketch, "E2201", {"start": v(22.91, -86.91) * mm, "end": v(22.42, -87.03) * mm});
            skLineSegment(sketch, "E2202", {"start": v(-35, -84.16) * mm, "end": v(-34.94, -83.9) * mm});
            skLineSegment(sketch, "E2203", {"start": v(23.71, -90.16) * mm, "end": v(22.91, -86.91) * mm});
            skLineSegment(sketch, "E2204", {"start": v(-54.71, 68.97) * mm, "end": v(-54.8, 69.12) * mm});
            skLineSegment(sketch, "E2205", {"start": v(23.3, -90.26) * mm, "end": v(23.71, -90.16) * mm});
            skLineSegment(sketch, "E2206", {"start": v(-54.8, 69.12) * mm, "end": v(-54.8, 69.23) * mm});
            skLineSegment(sketch, "E2207", {"start": v(23.13, -89.84) * mm, "end": v(23.3, -90.26) * mm});
            skLineSegment(sketch, "E2208", {"start": v(-54.8, 69.23) * mm, "end": v(-54.76, 69.35) * mm});
            skLineSegment(sketch, "E2209", {"start": v(23.1, -89.85) * mm, "end": v(23.13, -89.84) * mm});
            skLineSegment(sketch, "E2210", {"start": v(-54.76, 69.35) * mm, "end": v(-54.69, 69.42) * mm});
            skLineSegment(sketch, "E2211", {"start": v(23.1, -89.85) * mm, "end": v(22.96, -90.13) * mm});
            skLineSegment(sketch, "E2212", {"start": v(-54.69, 69.42) * mm, "end": v(-54.57, 69.48) * mm});
            skLineSegment(sketch, "E2213", {"start": v(22.96, -90.13) * mm, "end": v(22.78, -90.32) * mm});
            skLineSegment(sketch, "E2214", {"start": v(-54.57, 69.48) * mm, "end": v(-54.47, 69.5) * mm});
            skLineSegment(sketch, "E2215", {"start": v(22.78, -90.32) * mm, "end": v(22.48, -90.5) * mm});
            skLineSegment(sketch, "E2216", {"start": v(-54.47, 69.5) * mm, "end": v(-54.34, 69.44) * mm});
            skLineSegment(sketch, "E2217", {"start": v(22.48, -90.5) * mm, "end": v(22.2, -90.6) * mm});
            skLineSegment(sketch, "E2218", {"start": v(-54.34, 69.44) * mm, "end": v(-54.24, 69.34) * mm});
            skLineSegment(sketch, "E2219", {"start": v(27.08, -84.74) * mm, "end": v(27.1, -84.9) * mm});
            skLineSegment(sketch, "E2220", {"start": v(-54.24, 69.34) * mm, "end": v(-54.16, 69.2) * mm});
            skLineSegment(sketch, "E2221", {"start": v(27.1, -84.9) * mm, "end": v(27.07, -85.01) * mm});
            skLineSegment(sketch, "E2222", {"start": v(-54.16, 69.2) * mm, "end": v(-54.15, 69.09) * mm});
            skLineSegment(sketch, "E2223", {"start": v(27.07, -85.01) * mm, "end": v(27, -85.1) * mm});
            skLineSegment(sketch, "E2224", {"start": v(-54.15, 69.09) * mm, "end": v(-54.2, 68.97) * mm});
            skLineSegment(sketch, "E2225", {"start": v(27, -85.1) * mm, "end": v(26.9, -85.15) * mm});
            skLineSegment(sketch, "E2226", {"start": v(-54.2, 68.97) * mm, "end": v(-54.27, 68.9) * mm});
            skLineSegment(sketch, "E2227", {"start": v(26.9, -85.15) * mm, "end": v(26.77, -85.17) * mm});
            skLineSegment(sketch, "E2228", {"start": v(-54.27, 68.9) * mm, "end": v(-54.39, 68.84) * mm});
            skLineSegment(sketch, "E2229", {"start": v(26.77, -85.17) * mm, "end": v(26.67, -85.14) * mm});
            skLineSegment(sketch, "E2230", {"start": v(-54.39, 68.84) * mm, "end": v(-54.49, 68.83) * mm});
            skLineSegment(sketch, "E2231", {"start": v(26.67, -85.14) * mm, "end": v(26.57, -85.04) * mm});
            skLineSegment(sketch, "E2232", {"start": v(-54.49, 68.83) * mm, "end": v(-54.62, 68.88) * mm});
            skLineSegment(sketch, "E2233", {"start": v(26.57, -85.04) * mm, "end": v(26.51, -84.92) * mm});
            skLineSegment(sketch, "E2234", {"start": v(-54.62, 68.88) * mm, "end": v(-54.71, 68.97) * mm});
            skLineSegment(sketch, "E2235", {"start": v(26.51, -84.92) * mm, "end": v(26.49, -84.76) * mm});
            skLineSegment(sketch, "E2236", {"start": v(-58.57, 68.3) * mm, "end": v(-58.72, 68.3) * mm});
            skLineSegment(sketch, "E2237", {"start": v(26.49, -84.76) * mm, "end": v(26.52, -84.65) * mm});
            skLineSegment(sketch, "E2238", {"start": v(-58.72, 68.3) * mm, "end": v(-58.86, 68.28) * mm});
            skLineSegment(sketch, "E2239", {"start": v(26.52, -84.65) * mm, "end": v(26.6, -84.56) * mm});
            skLineSegment(sketch, "E2240", {"start": v(-58.86, 68.28) * mm, "end": v(-59.13, 68.2) * mm});
            skLineSegment(sketch, "E2241", {"start": v(26.6, -84.56) * mm, "end": v(26.7, -84.51) * mm});
            skLineSegment(sketch, "E2242", {"start": v(-59.13, 68.2) * mm, "end": v(-59.46, 68.09) * mm});
            skLineSegment(sketch, "E2243", {"start": v(26.7, -84.51) * mm, "end": v(26.82, -84.5) * mm});
            skLineSegment(sketch, "E2244", {"start": v(-59.46, 68.09) * mm, "end": v(-60.04, 67.92) * mm});
            skLineSegment(sketch, "E2245", {"start": v(26.82, -84.5) * mm, "end": v(26.92, -84.53) * mm});
            skLineSegment(sketch, "E2246", {"start": v(-60.04, 67.92) * mm, "end": v(-60.36, 67.9) * mm});
            skLineSegment(sketch, "E2247", {"start": v(26.92, -84.53) * mm, "end": v(27.03, -84.62) * mm});
            skLineSegment(sketch, "E2248", {"start": v(-60.36, 67.9) * mm, "end": v(-60.67, 68) * mm});
            skLineSegment(sketch, "E2249", {"start": v(27.03, -84.62) * mm, "end": v(27.08, -84.74) * mm});
            skLineSegment(sketch, "E2250", {"start": v(-60.67, 68) * mm, "end": v(-60.88, 68.17) * mm});
            skLineSegment(sketch, "E2251", {"start": v(30.23, -84.56) * mm, "end": v(30.81, -84.45) * mm});
            skLineSegment(sketch, "E2252", {"start": v(-60.88, 68.17) * mm, "end": v(-61.1, 68.59) * mm});
            skLineSegment(sketch, "E2253", {"start": v(30.81, -84.45) * mm, "end": v(31.19, -84.53) * mm});
            skLineSegment(sketch, "E2254", {"start": v(-61.1, 68.59) * mm, "end": v(-61.09, 68.94) * mm});
            skLineSegment(sketch, "E2255", {"start": v(31.19, -84.53) * mm, "end": v(31.56, -84.86) * mm});
            skLineSegment(sketch, "E2256", {"start": v(-61.09, 68.94) * mm, "end": v(-60.86, 69.41) * mm});
            skLineSegment(sketch, "E2257", {"start": v(31.56, -84.86) * mm, "end": v(31.79, -85.31) * mm});
            skLineSegment(sketch, "E2258", {"start": v(-60.86, 69.41) * mm, "end": v(-60.51, 69.78) * mm});
            skLineSegment(sketch, "E2259", {"start": v(32.52, -87.37) * mm, "end": v(31.79, -85.31) * mm});
            skLineSegment(sketch, "E2260", {"start": v(-60.51, 69.78) * mm, "end": v(-59.98, 70.15) * mm});
            skLineSegment(sketch, "E2261", {"start": v(32.04, -87.54) * mm, "end": v(32.52, -87.37) * mm});
            skLineSegment(sketch, "E2262", {"start": v(-59.98, 70.15) * mm, "end": v(-59.6, 70.3) * mm});
            skLineSegment(sketch, "E2263", {"start": v(31.31, -85.5) * mm, "end": v(32.04, -87.54) * mm});
            skLineSegment(sketch, "E2264", {"start": v(-59.28, 69.94) * mm, "end": v(-59.6, 70.3) * mm});
            skLineSegment(sketch, "E2265", {"start": v(31.31, -85.5) * mm, "end": v(31.13, -85.15) * mm});
            skLineSegment(sketch, "E2266", {"start": v(-59.28, 69.94) * mm, "end": v(-59.58, 69.85) * mm});
            skLineSegment(sketch, "E2267", {"start": v(31.13, -85.15) * mm, "end": v(30.93, -84.98) * mm});
            skLineSegment(sketch, "E2268", {"start": v(-59.58, 69.85) * mm, "end": v(-59.8, 69.75) * mm});
            skLineSegment(sketch, "E2269", {"start": v(30.93, -84.98) * mm, "end": v(30.62, -84.92) * mm});
            skLineSegment(sketch, "E2270", {"start": v(-59.8, 69.75) * mm, "end": v(-60.07, 69.6) * mm});
            skLineSegment(sketch, "E2271", {"start": v(30.62, -84.92) * mm, "end": v(30.32, -85) * mm});
            skLineSegment(sketch, "E2272", {"start": v(-60.07, 69.6) * mm, "end": v(-60.25, 69.45) * mm});
            skLineSegment(sketch, "E2273", {"start": v(30.32, -85) * mm, "end": v(29.88, -85.24) * mm});
            skLineSegment(sketch, "E2274", {"start": v(-60.25, 69.45) * mm, "end": v(-60.52, 69.17) * mm});
            skLineSegment(sketch, "E2275", {"start": v(29.88, -85.24) * mm, "end": v(29.69, -85.51) * mm});
            skLineSegment(sketch, "E2276", {"start": v(-60.52, 69.17) * mm, "end": v(-60.63, 68.96) * mm});
            skLineSegment(sketch, "E2277", {"start": v(29.69, -85.51) * mm, "end": v(29.65, -85.99) * mm});
            skLineSegment(sketch, "E2278", {"start": v(-60.63, 68.96) * mm, "end": v(-60.64, 68.7) * mm});
            skLineSegment(sketch, "E2279", {"start": v(29.65, -85.99) * mm, "end": v(29.77, -86.48) * mm});
            skLineSegment(sketch, "E2280", {"start": v(-60.64, 68.7) * mm, "end": v(-60.54, 68.52) * mm});
            skLineSegment(sketch, "E2281", {"start": v(30.36, -88.13) * mm, "end": v(29.77, -86.48) * mm});
            skLineSegment(sketch, "E2282", {"start": v(-60.54, 68.52) * mm, "end": v(-60.36, 68.4) * mm});
            skLineSegment(sketch, "E2283", {"start": v(29.88, -88.3) * mm, "end": v(30.36, -88.13) * mm});
            skLineSegment(sketch, "E2284", {"start": v(-60.36, 68.4) * mm, "end": v(-60.19, 68.38) * mm});
            skLineSegment(sketch, "E2285", {"start": v(28.76, -85.15) * mm, "end": v(29.88, -88.3) * mm});
            skLineSegment(sketch, "E2286", {"start": v(-60.19, 68.38) * mm, "end": v(-59.86, 68.44) * mm});
            skLineSegment(sketch, "E2287", {"start": v(29.15, -85.01) * mm, "end": v(28.76, -85.15) * mm});
            skLineSegment(sketch, "E2288", {"start": v(-59.86, 68.44) * mm, "end": v(-59.47, 68.57) * mm});
            skLineSegment(sketch, "E2289", {"start": v(29.38, -85.42) * mm, "end": v(29.15, -85.01) * mm});
            skLineSegment(sketch, "E2290", {"start": v(-59.47, 68.57) * mm, "end": v(-59.03, 68.72) * mm});
            skLineSegment(sketch, "E2291", {"start": v(29.4, -85.4) * mm, "end": v(29.38, -85.42) * mm});
            skLineSegment(sketch, "E2292", {"start": v(-59.03, 68.72) * mm, "end": v(-58.77, 68.77) * mm});
            skLineSegment(sketch, "E2293", {"start": v(29.4, -85.4) * mm, "end": v(29.53, -85.1) * mm});
            skLineSegment(sketch, "E2294", {"start": v(-58.77, 68.77) * mm, "end": v(-58.53, 68.78) * mm});
            skLineSegment(sketch, "E2295", {"start": v(29.53, -85.1) * mm, "end": v(29.69, -84.9) * mm});
            skLineSegment(sketch, "E2296", {"start": v(-58.53, 68.78) * mm, "end": v(-58.36, 68.74) * mm});
            skLineSegment(sketch, "E2297", {"start": v(29.69, -84.9) * mm, "end": v(29.97, -84.69) * mm});
            skLineSegment(sketch, "E2298", {"start": v(-58.36, 68.74) * mm, "end": v(-58.17, 68.64) * mm});
            skLineSegment(sketch, "E2299", {"start": v(29.97, -84.69) * mm, "end": v(30.23, -84.56) * mm});
            skLineSegment(sketch, "E2300", {"start": v(-58.17, 68.64) * mm, "end": v(-58.03, 68.5) * mm});
            skLineSegment(sketch, "E2301", {"start": v(16.12, -88.16) * mm, "end": v(15.9, -87.03) * mm});
            skLineSegment(sketch, "E2302", {"start": v(-58.03, 68.5) * mm, "end": v(-57.85, 68.13) * mm});
            skLineSegment(sketch, "E2303", {"start": v(16.12, -88.16) * mm, "end": v(16.2, -88.57) * mm});
            skLineSegment(sketch, "E2304", {"start": v(-57.85, 68.13) * mm, "end": v(-57.86, 67.8) * mm});
            skLineSegment(sketch, "E2305", {"start": v(16.2, -88.57) * mm, "end": v(16.23, -88.85) * mm});
            skLineSegment(sketch, "E2306", {"start": v(-57.86, 67.8) * mm, "end": v(-58.07, 67.36) * mm});
            skLineSegment(sketch, "E2307", {"start": v(16.25, -88.85) * mm, "end": v(16.23, -88.85) * mm});
            skLineSegment(sketch, "E2308", {"start": v(-58.07, 67.36) * mm, "end": v(-58.4, 67.02) * mm});
            skLineSegment(sketch, "E2309", {"start": v(16.25, -88.85) * mm, "end": v(16.67, -88.36) * mm});
            skLineSegment(sketch, "E2310", {"start": v(-58.4, 67.02) * mm, "end": v(-58.9, 66.69) * mm});
            skLineSegment(sketch, "E2311", {"start": v(16.67, -88.36) * mm, "end": v(17.19, -88.16) * mm});
            skLineSegment(sketch, "E2312", {"start": v(-58.9, 66.69) * mm, "end": v(-59.34, 66.5) * mm});
            skLineSegment(sketch, "E2313", {"start": v(17.19, -88.16) * mm, "end": v(17.85, -88.17) * mm});
            skLineSegment(sketch, "E2314", {"start": v(-59.47, 66.93) * mm, "end": v(-59.34, 66.5) * mm});
            skLineSegment(sketch, "E2315", {"start": v(17.85, -88.17) * mm, "end": v(18.28, -88.4) * mm});
            skLineSegment(sketch, "E2316", {"start": v(-59.47, 66.93) * mm, "end": v(-58.96, 67.15) * mm});
            skLineSegment(sketch, "E2317", {"start": v(18.28, -88.4) * mm, "end": v(18.68, -88.96) * mm});
            skLineSegment(sketch, "E2318", {"start": v(18.68, -88.96) * mm, "end": v(18.88, -89.59) * mm});
            skLineSegment(sketch, "E2319", {"start": v(18.88, -89.59) * mm, "end": v(18.92, -90.4) * mm});
            skLineSegment(sketch, "E2320", {"start": v(18.92, -90.4) * mm, "end": v(18.76, -90.91) * mm});
            skLineSegment(sketch, "E2321", {"start": v(18.76, -90.91) * mm, "end": v(18.34, -91.37) * mm});
            skLineSegment(sketch, "E2322", {"start": v(18.34, -91.37) * mm, "end": v(17.84, -91.55) * mm});
            skLineSegment(sketch, "E2323", {"start": v(17.84, -91.55) * mm, "end": v(17.5, -91.58) * mm});
            skLineSegment(sketch, "E2324", {"start": v(17.5, -91.58) * mm, "end": v(17.23, -91.55) * mm});
            skLineSegment(sketch, "E2325", {"start": v(17.23, -91.55) * mm, "end": v(16.93, -91.43) * mm});
            skLineSegment(sketch, "E2326", {"start": v(16.93, -91.43) * mm, "end": v(16.72, -91.27) * mm});
            skLineSegment(sketch, "E2327", {"start": v(16.68, -91.28) * mm, "end": v(16.72, -91.27) * mm});
            skLineSegment(sketch, "E2328", {"start": v(16.66, -91.72) * mm, "end": v(16.68, -91.28) * mm});
            skLineSegment(sketch, "E2329", {"start": v(16.3, -91.79) * mm, "end": v(16.66, -91.72) * mm});
            skLineSegment(sketch, "E2330", {"start": v(15.4, -87.13) * mm, "end": v(16.3, -91.79) * mm});
            skLineSegment(sketch, "E2331", {"start": v(15.9, -87.03) * mm, "end": v(15.4, -87.13) * mm});
            skLineSegment(sketch, "E2332", {"start": v(8.49, -89.4) * mm, "end": v(9.08, -89.44) * mm});
            skLineSegment(sketch, "E2333", {"start": v(9.08, -89.44) * mm, "end": v(9.42, -89.61) * mm});
            skLineSegment(sketch, "E2334", {"start": v(9.42, -89.61) * mm, "end": v(9.7, -90.02) * mm});
            skLineSegment(sketch, "E2335", {"start": v(9.7, -90.02) * mm, "end": v(9.8, -90.51) * mm});
            skLineSegment(sketch, "E2336", {"start": v(10, -92.68) * mm, "end": v(9.8, -90.51) * mm});
            skLineSegment(sketch, "E2337", {"start": v(9.5, -92.73) * mm, "end": v(10, -92.68) * mm});
            skLineSegment(sketch, "E2338", {"start": v(9.3, -90.58) * mm, "end": v(9.5, -92.73) * mm});
            skLineSegment(sketch, "E2339", {"start": v(9.3, -90.58) * mm, "end": v(9.21, -90.2) * mm});
            skLineSegment(sketch, "E2340", {"start": v(9.21, -90.2) * mm, "end": v(9.07, -89.99) * mm});
            skLineSegment(sketch, "E2341", {"start": v(9.07, -89.99) * mm, "end": v(8.78, -89.85) * mm});
            skLineSegment(sketch, "E2342", {"start": v(8.78, -89.85) * mm, "end": v(8.47, -89.84) * mm});
            skLineSegment(sketch, "E2343", {"start": v(8.47, -89.84) * mm, "end": v(7.98, -89.97) * mm});
            skLineSegment(sketch, "E2344", {"start": v(7.98, -89.97) * mm, "end": v(7.73, -90.2) * mm});
            skLineSegment(sketch, "E2345", {"start": v(7.73, -90.2) * mm, "end": v(7.57, -90.64) * mm});
            skLineSegment(sketch, "E2346", {"start": v(7.57, -90.64) * mm, "end": v(7.57, -91.15) * mm});
            skLineSegment(sketch, "E2347", {"start": v(7.73, -92.9) * mm, "end": v(7.57, -91.15) * mm});
            skLineSegment(sketch, "E2348", {"start": v(7.22, -92.94) * mm, "end": v(7.73, -92.9) * mm});
            skLineSegment(sketch, "E2349", {"start": v(6.92, -89.61) * mm, "end": v(7.22, -92.94) * mm});
            skLineSegment(sketch, "E2350", {"start": v(7.33, -89.57) * mm, "end": v(6.92, -89.61) * mm});
            skLineSegment(sketch, "E2351", {"start": v(7.45, -90.02) * mm, "end": v(7.33, -89.57) * mm});
            skLineSegment(sketch, "E2352", {"start": v(7.48, -90.02) * mm, "end": v(7.45, -90.02) * mm});
            skLineSegment(sketch, "E2353", {"start": v(7.48, -90.02) * mm, "end": v(7.67, -89.76) * mm});
            skLineSegment(sketch, "E2354", {"start": v(7.67, -89.76) * mm, "end": v(7.88, -89.6) * mm});
            skLineSegment(sketch, "E2355", {"start": v(7.88, -89.6) * mm, "end": v(8.2, -89.46) * mm});
            skLineSegment(sketch, "E2356", {"start": v(8.2, -89.46) * mm, "end": v(8.49, -89.4) * mm});
            skLineSegment(sketch, "E2357", {"start": v(-1.31, -91.53) * mm, "end": v(-1.19, -90.73) * mm});
            skLineSegment(sketch, "E2358", {"start": v(-1.19, -90.73) * mm, "end": v(-0.9, -90.26) * mm});
            skLineSegment(sketch, "E2359", {"start": v(-0.9, -90.26) * mm, "end": v(-0.35, -89.89) * mm});
            skLineSegment(sketch, "E2360", {"start": v(-0.35, -89.89) * mm, "end": v(0.23, -89.8) * mm});
            skLineSegment(sketch, "E2361", {"start": v(0.23, -89.8) * mm, "end": v(0.92, -89.94) * mm});
            skLineSegment(sketch, "E2362", {"start": v(0.92, -89.94) * mm, "end": v(1.34, -90.26) * mm});
            skLineSegment(sketch, "E2363", {"start": v(1.34, -90.26) * mm, "end": v(1.68, -90.89) * mm});
            skLineSegment(sketch, "E2364", {"start": v(1.68, -90.89) * mm, "end": v(1.76, -91.53) * mm});
            skLineSegment(sketch, "E2365", {"start": v(1.76, -91.53) * mm, "end": v(1.63, -92.33) * mm});
            skLineSegment(sketch, "E2366", {"start": v(1.63, -92.33) * mm, "end": v(1.35, -92.8) * mm});
            skLineSegment(sketch, "E2367", {"start": v(1.35, -92.8) * mm, "end": v(0.8, -93.18) * mm});
            skLineSegment(sketch, "E2368", {"start": v(0.8, -93.18) * mm, "end": v(0.21, -93.27) * mm});
            skLineSegment(sketch, "E2369", {"start": v(0.21, -93.27) * mm, "end": v(-0.26, -93.2) * mm});
            skLineSegment(sketch, "E2370", {"start": v(-0.26, -93.2) * mm, "end": v(-0.58, -93.06) * mm});
            skLineSegment(sketch, "E2371", {"start": v(-0.58, -93.06) * mm, "end": v(-0.92, -92.76) * mm});
            skLineSegment(sketch, "E2372", {"start": v(-0.92, -92.76) * mm, "end": v(-1.12, -92.45) * mm});
            skLineSegment(sketch, "E2373", {"start": v(-1.12, -92.45) * mm, "end": v(-1.27, -91.97) * mm});
            skLineSegment(sketch, "E2374", {"start": v(-1.27, -91.97) * mm, "end": v(-1.31, -91.53) * mm});
            skLineSegment(sketch, "E2375", {"start": v(-13.72, -88.73) * mm, "end": v(-13.17, -88.9) * mm});
            skLineSegment(sketch, "E2376", {"start": v(-13.17, -88.9) * mm, "end": v(-12.89, -89.13) * mm});
            skLineSegment(sketch, "E2377", {"start": v(-12.89, -89.13) * mm, "end": v(-12.72, -89.56) * mm});
            skLineSegment(sketch, "E2378", {"start": v(-12.72, -89.56) * mm, "end": v(-12.73, -90.02) * mm});
            skLineSegment(sketch, "E2379", {"start": v(-13.09, -92.27) * mm, "end": v(-12.73, -90.02) * mm});
            skLineSegment(sketch, "E2380", {"start": v(-13.46, -92.21) * mm, "end": v(-13.09, -92.27) * mm});
            skLineSegment(sketch, "E2381", {"start": v(-13.48, -91.73) * mm, "end": v(-13.46, -92.21) * mm});
            skLineSegment(sketch, "E2382", {"start": v(-13.5, -91.72) * mm, "end": v(-13.48, -91.73) * mm});
            skLineSegment(sketch, "E2383", {"start": v(-13.5, -91.72) * mm, "end": v(-13.83, -91.96) * mm});
            skLineSegment(sketch, "E2384", {"start": v(-13.83, -91.96) * mm, "end": v(-14.07, -92.07) * mm});
            skLineSegment(sketch, "E2385", {"start": v(-14.07, -92.07) * mm, "end": v(-14.4, -92.1) * mm});
            skLineSegment(sketch, "E2386", {"start": v(-14.4, -92.1) * mm, "end": v(-14.7, -92.08) * mm});
            skLineSegment(sketch, "E2387", {"start": v(-14.7, -92.08) * mm, "end": v(-15.17, -91.92) * mm});
            skLineSegment(sketch, "E2388", {"start": v(-15.17, -91.92) * mm, "end": v(-15.43, -91.7) * mm});
            skLineSegment(sketch, "E2389", {"start": v(-15.43, -91.7) * mm, "end": v(-15.6, -91.32) * mm});
            skLineSegment(sketch, "E2390", {"start": v(-15.6, -91.32) * mm, "end": v(-15.6, -90.94) * mm});
            skLineSegment(sketch, "E2391", {"start": v(-15.6, -90.94) * mm, "end": v(-14.96, -90.2) * mm});
            skLineSegment(sketch, "E2392", {"start": v(-14.96, -90.2) * mm, "end": v(-13.83, -90.14) * mm});
            skLineSegment(sketch, "E2393", {"start": v(-13.26, -90.21) * mm, "end": v(-13.83, -90.14) * mm});
            skLineSegment(sketch, "E2394", {"start": v(-13.23, -90) * mm, "end": v(-13.26, -90.21) * mm});
            skLineSegment(sketch, "E2395", {"start": v(-13.23, -90) * mm, "end": v(-13.23, -89.63) * mm});
            skLineSegment(sketch, "E2396", {"start": v(-13.23, -89.63) * mm, "end": v(-13.3, -89.4) * mm});
            skLineSegment(sketch, "E2397", {"start": v(-13.3, -89.4) * mm, "end": v(-13.54, -89.22) * mm});
            skLineSegment(sketch, "E2398", {"start": v(-13.54, -89.22) * mm, "end": v(-13.81, -89.14) * mm});
            skLineSegment(sketch, "E2399", {"start": v(-13.81, -89.14) * mm, "end": v(-14.32, -89.14) * mm});
            skLineSegment(sketch, "E2400", {"start": v(-14.32, -89.14) * mm, "end": v(-14.79, -89.24) * mm});
            skLineSegment(sketch, "E2401", {"start": v(-14.88, -88.84) * mm, "end": v(-14.79, -89.24) * mm});
            skLineSegment(sketch, "E2402", {"start": v(-14.88, -88.84) * mm, "end": v(-14.57, -88.75) * mm});
            skLineSegment(sketch, "E2403", {"start": v(-14.57, -88.75) * mm, "end": v(-14.31, -88.71) * mm});
            skLineSegment(sketch, "E2404", {"start": v(-14.31, -88.71) * mm, "end": v(-13.98, -88.7) * mm});
            skLineSegment(sketch, "E2405", {"start": v(-13.98, -88.7) * mm, "end": v(-13.72, -88.73) * mm});
            skLineSegment(sketch, "E2406", {"start": v(-28.74, -85.02) * mm, "end": v(-28.22, -85.3) * mm});
            skLineSegment(sketch, "E2407", {"start": v(-28.22, -85.3) * mm, "end": v(-27.98, -85.59) * mm});
            skLineSegment(sketch, "E2408", {"start": v(-27.98, -85.59) * mm, "end": v(-27.88, -86.08) * mm});
            skLineSegment(sketch, "E2409", {"start": v(-27.88, -86.08) * mm, "end": v(-28, -86.57) * mm});
            skLineSegment(sketch, "E2410", {"start": v(-28.7, -88.63) * mm, "end": v(-28, -86.57) * mm});
            skLineSegment(sketch, "E2411", {"start": v(-29.18, -88.47) * mm, "end": v(-28.7, -88.63) * mm});
            skLineSegment(sketch, "E2412", {"start": v(-28.48, -86.42) * mm, "end": v(-29.18, -88.47) * mm});
            skLineSegment(sketch, "E2413", {"start": v(-28.48, -86.42) * mm, "end": v(-28.4, -86.03) * mm});
            skLineSegment(sketch, "E2414", {"start": v(-28.4, -86.03) * mm, "end": v(-28.45, -85.78) * mm});
            skLineSegment(sketch, "E2415", {"start": v(-28.45, -85.78) * mm, "end": v(-28.66, -85.54) * mm});
            skLineSegment(sketch, "E2416", {"start": v(-28.66, -85.54) * mm, "end": v(-28.94, -85.4) * mm});
            skLineSegment(sketch, "E2417", {"start": v(-28.94, -85.4) * mm, "end": v(-29.44, -85.32) * mm});
            skLineSegment(sketch, "E2418", {"start": v(-29.44, -85.32) * mm, "end": v(-29.76, -85.42) * mm});
            skLineSegment(sketch, "E2419", {"start": v(-29.76, -85.42) * mm, "end": v(-30.08, -85.77) * mm});
            skLineSegment(sketch, "E2420", {"start": v(-30.08, -85.77) * mm, "end": v(-30.3, -86.23) * mm});
            skLineSegment(sketch, "E2421", {"start": v(-30.86, -87.89) * mm, "end": v(-30.3, -86.23) * mm});
            skLineSegment(sketch, "E2422", {"start": v(-31.34, -87.72) * mm, "end": v(-30.86, -87.89) * mm});
            skLineSegment(sketch, "E2423", {"start": v(-30.25, -84.56) * mm, "end": v(-31.34, -87.72) * mm});
            skLineSegment(sketch, "E2424", {"start": v(-29.86, -84.7) * mm, "end": v(-30.25, -84.56) * mm});
            skLineSegment(sketch, "E2425", {"start": v(-29.94, -85.15) * mm, "end": v(-29.86, -84.7) * mm});
            skLineSegment(sketch, "E2426", {"start": v(-29.91, -85.16) * mm, "end": v(-29.94, -85.15) * mm});
            skLineSegment(sketch, "E2427", {"start": v(-29.91, -85.16) * mm, "end": v(-29.63, -85) * mm});
            skLineSegment(sketch, "E2428", {"start": v(-29.63, -85) * mm, "end": v(-29.38, -84.94) * mm});
            skLineSegment(sketch, "E2429", {"start": v(-29.38, -84.94) * mm, "end": v(-29.02, -84.95) * mm});
            skLineSegment(sketch, "E2430", {"start": v(-29.02, -84.95) * mm, "end": v(-28.74, -85.02) * mm});
            skLineSegment(sketch, "E2431", {"start": v(-34.94, -83.9) * mm, "end": v(-34.64, -83.44) * mm});
            skLineSegment(sketch, "E2432", {"start": v(-34.64, -83.44) * mm, "end": v(-34.32, -83.23) * mm});
            skLineSegment(sketch, "E2433", {"start": v(-34.32, -83.23) * mm, "end": v(-33.8, -83.18) * mm});
            skLineSegment(sketch, "E2434", {"start": v(-33.8, -83.18) * mm, "end": v(-33.34, -83.3) * mm});
            skLineSegment(sketch, "E2435", {"start": v(-33.34, -83.3) * mm, "end": v(-33.09, -83.43) * mm});
            skLineSegment(sketch, "E2436", {"start": v(-33.09, -83.43) * mm, "end": v(-32.92, -83.54) * mm});
            skLineSegment(sketch, "E2437", {"start": v(-31.85, -83.97) * mm, "end": v(-32.92, -83.54) * mm});
            skLineSegment(sketch, "E2438", {"start": v(-31.97, -84.27) * mm, "end": v(-31.85, -83.97) * mm});
            skLineSegment(sketch, "E2439", {"start": v(-32.57, -84.1) * mm, "end": v(-31.97, -84.27) * mm});
            skLineSegment(sketch, "E2440", {"start": v(-32.57, -84.1) * mm, "end": v(-32.54, -84.27) * mm});
            skSolve(sketch);
        }
        {
            var Q0;
            Q0=makeQuery(id+"F2.imprint","IMPRINT",FACE,{"disambiguationData":[TD([[makeQuery(id+"F2.imprint","IMPRINT",EDGE,{"derivedFrom":sQuery(id+"F2.wireOp",EDGE,"E2123")}),1.0]])]});
            var Q1;
            Q1=makeQuery(id+"F2.imprint","IMPRINT",FACE,{"disambiguationData":[TD([[makeQuery(id+"F2.imprint","IMPRINT",EDGE,{"derivedFrom":sQuery(id+"F2.wireOp",EDGE,"E2100")}),1.0]])]});
            var Q2;
            Q2=makeQuery(id+"F2.imprint","IMPRINT",FACE,{"disambiguationData":[TD([[makeQuery(id+"F2.imprint","IMPRINT",EDGE,{"derivedFrom":sQuery(id+"F2.wireOp",EDGE,"E619")}),1.0]])]});
            var Q3;
            Q3=makeQuery(id+"F2.imprint","IMPRINT",FACE,{"disambiguationData":[TD([[makeQuery(id+"F2.imprint","IMPRINT",EDGE,{"derivedFrom":sQuery(id+"F2.wireOp",EDGE,"E2251")}),-1.0]])]});
            var Q4;
            Q4=makeQuery(id+"F2.imprint","IMPRINT",FACE,{"disambiguationData":[TD([[makeQuery(id+"F2.imprint","IMPRINT",EDGE,{"derivedFrom":sQuery(id+"F2.wireOp",EDGE,"E533")}),1.0]])]});
            var Q5;
            Q5=makeQuery(id+"F2.imprint","IMPRINT",FACE,{"disambiguationData":[TD([[makeQuery(id+"F2.imprint","IMPRINT",EDGE,{"derivedFrom":sQuery(id+"F2.wireOp",EDGE,"E2010")}),1.0]])]});
            var Q6;
            Q6=makeQuery(id+"F2.imprint","IMPRINT",FACE,{"disambiguationData":[TD([[makeQuery(id+"F2.imprint","IMPRINT",EDGE,{"derivedFrom":sQuery(id+"F2.wireOp",EDGE,"E623")}),1.0]])]});
            var Q7;
            Q7=makeQuery(id+"F2.imprint","IMPRINT",FACE,{"disambiguationData":[TD([[makeQuery(id+"F2.imprint","IMPRINT",EDGE,{"derivedFrom":sQuery(id+"F2.wireOp",EDGE,"E2068")}),1.0]])]});
            var Q8;
            Q8=makeQuery(id+"F2.imprint","IMPRINT",FACE,{"disambiguationData":[TD([[makeQuery(id+"F2.imprint","IMPRINT",EDGE,{"derivedFrom":sQuery(id+"F2.wireOp",EDGE,"E646")}),-1.0]])]});
            var Q9;
            Q9=makeQuery(id+"F2.imprint","IMPRINT",FACE,{"disambiguationData":[TD([[makeQuery(id+"F2.imprint","IMPRINT",EDGE,{"derivedFrom":sQuery(id+"F2.wireOp",EDGE,"E1060")}),-1.0]])]});
            var Q10;
            Q10=makeQuery(id+"F2.imprint","IMPRINT",FACE,{"disambiguationData":[TD([[makeQuery(id+"F2.imprint","IMPRINT",EDGE,{"derivedFrom":sQuery(id+"F2.wireOp",EDGE,"E2107")}),1.0]])]});
            var Q11;
            Q11=makeQuery(id+"F2.imprint","IMPRINT",FACE,{"disambiguationData":[TD([[makeQuery(id+"F2.imprint","IMPRINT",EDGE,{"derivedFrom":sQuery(id+"F2.wireOp",EDGE,"E1035")}),-1.0]])]});
            var Q12;
            Q12=makeQuery(id+"F2.imprint","IMPRINT",FACE,{"disambiguationData":[TD([[makeQuery(id+"F2.imprint","IMPRINT",EDGE,{"derivedFrom":sQuery(id+"F2.wireOp",EDGE,"E529")}),1.0]])]});
            var Q13;
            Q13=makeQuery(id+"F2.imprint","IMPRINT",FACE,{"disambiguationData":[TD([[makeQuery(id+"F2.imprint","IMPRINT",EDGE,{"derivedFrom":sQuery(id+"F2.wireOp",EDGE,"E2020")}),1.0]])]});
            var Q14;
            Q14=makeQuery(id+"F2.imprint","IMPRINT",FACE,{"disambiguationData":[TD([[makeQuery(id+"F2.imprint","IMPRINT",EDGE,{"derivedFrom":sQuery(id+"F2.wireOp",EDGE,"E2064")}),1.0]])]});
            var Q15;
            Q15=makeQuery(id+"F2.imprint","IMPRINT",FACE,{"disambiguationData":[TD([[makeQuery(id+"F2.imprint","IMPRINT",EDGE,{"derivedFrom":sQuery(id+"F2.wireOp",EDGE,"E668")}),1.0]])]});
            var Q16;
            Q16=makeQuery(id+"F2.imprint","IMPRINT",FACE,{"disambiguationData":[TD([[makeQuery(id+"F2.imprint","IMPRINT",EDGE,{"derivedFrom":sQuery(id+"F2.wireOp",EDGE,"E545")}),1.0]])]});
            var Q17;
            Q17=makeQuery(id+"F2.imprint","IMPRINT",FACE,{"disambiguationData":[TD([[makeQuery(id+"F2.imprint","IMPRINT",EDGE,{"derivedFrom":sQuery(id+"F2.wireOp",EDGE,"E2169")}),-1.0]])]});
            var Q18;
            Q18=makeQuery(id+"F2.imprint","IMPRINT",FACE,{"disambiguationData":[TD([[makeQuery(id+"F2.imprint","IMPRINT",EDGE,{"derivedFrom":sQuery(id+"F2.wireOp",EDGE,"E977")}),-1.0]])]});
            var Q19;
            Q19=makeQuery(id+"F2.imprint","IMPRINT",FACE,{"disambiguationData":[TD([[makeQuery(id+"F2.imprint","IMPRINT",EDGE,{"derivedFrom":sQuery(id+"F2.wireOp",EDGE,"E593")}),1.0]])]});
            var Q20;
            Q20=makeQuery(id+"F2.imprint","IMPRINT",FACE,{"disambiguationData":[TD([[makeQuery(id+"F2.imprint","IMPRINT",EDGE,{"derivedFrom":sQuery(id+"F2.wireOp",EDGE,"E2219")}),-1.0]])]});
            var Q21;
            Q21=makeQuery(id+"F2.imprint","IMPRINT",FACE,{"disambiguationData":[TD([[makeQuery(id+"F2.imprint","IMPRINT",EDGE,{"derivedFrom":sQuery(id+"F2.wireOp",EDGE,"E627")}),1.0]])]});
            var Q22;
            Q22=makeQuery(id+"F2.imprint","IMPRINT",FACE,{"disambiguationData":[TD([[makeQuery(id+"F2.imprint","IMPRINT",EDGE,{"derivedFrom":sQuery(id+"F2.wireOp",EDGE,"E2332")}),-1.0]])]});
            var Q23;
            Q23=makeQuery(id+"F2.imprint","IMPRINT",FACE,{"disambiguationData":[TD([[makeQuery(id+"F2.imprint","IMPRINT",EDGE,{"derivedFrom":sQuery(id+"F2.wireOp",EDGE,"E521")}),1.0]])]});
            var Q24;
            Q24=makeQuery(id+"F2.imprint","IMPRINT",FACE,{"disambiguationData":[TD([[makeQuery(id+"F2.imprint","IMPRINT",EDGE,{"derivedFrom":sQuery(id+"F2.wireOp",EDGE,"E1984")}),1.0]])]});
            var Q25;
            Q25=makeQuery(id+"F2.imprint","IMPRINT",FACE,{"disambiguationData":[TD([[makeQuery(id+"F2.imprint","IMPRINT",EDGE,{"derivedFrom":sQuery(id+"F2.wireOp",EDGE,"E708")}),-1.0]])]});
            var Q26;
            Q26=makeQuery(id+"F2.imprint","IMPRINT",FACE,{"disambiguationData":[TD([[makeQuery(id+"F2.imprint","IMPRINT",EDGE,{"derivedFrom":sQuery(id+"F2.wireOp",EDGE,"E916")}),-1.0]])]});
            var Q27;
            Q27=makeQuery(id+"F2.imprint","IMPRINT",FACE,{"disambiguationData":[TD([[makeQuery(id+"F2.imprint","IMPRINT",EDGE,{"derivedFrom":sQuery(id+"F2.wireOp",EDGE,"E1012")}),-1.0]])]});
            var Q28;
            Q28=makeQuery(id+"F2.imprint","IMPRINT",FACE,{"disambiguationData":[TD([[makeQuery(id+"F2.imprint","IMPRINT",EDGE,{"derivedFrom":sQuery(id+"F2.wireOp",EDGE,"E525")}),1.0]])]});
            var Q29;
            Q29=makeQuery(id+"F2.imprint","IMPRINT",FACE,{"disambiguationData":[TD([[makeQuery(id+"F2.imprint","IMPRINT",EDGE,{"derivedFrom":sQuery(id+"F2.wireOp",EDGE,"E564")}),1.0]])]});
            var Q30;
            Q30=makeQuery(id+"F2.imprint","IMPRINT",FACE,{"disambiguationData":[TD([[makeQuery(id+"F2.imprint","IMPRINT",EDGE,{"derivedFrom":sQuery(id+"F2.wireOp",EDGE,"E2406")}),-1.0]])]});
            var Q31;
            Q31=makeQuery(id+"F2.imprint","IMPRINT",FACE,{"disambiguationData":[TD([[makeQuery(id+"F2.imprint","IMPRINT",EDGE,{"derivedFrom":sQuery(id+"F2.wireOp",EDGE,"E1019")}),-1.0]])]});
            var Q32;
            Q32=makeQuery(id+"F2.imprint","IMPRINT",FACE,{"disambiguationData":[TD([[makeQuery(id+"F2.imprint","IMPRINT",EDGE,{"derivedFrom":sQuery(id+"F2.wireOp",EDGE,"E1836")}),1.0]])]});
            var Q33;
            Q33=makeQuery(id+"F2.imprint","IMPRINT",FACE,{"disambiguationData":[TD([[makeQuery(id+"F2.imprint","IMPRINT",EDGE,{"derivedFrom":sQuery(id+"F2.wireOp",EDGE,"E1865")}),-1.0]])]});
            var Q34;
            Q34=makeQuery(id+"F2.imprint","IMPRINT",FACE,{"disambiguationData":[TD([[makeQuery(id+"F2.imprint","IMPRINT",EDGE,{"derivedFrom":sQuery(id+"F2.wireOp",EDGE,"E959")}),-1.0]])]});
            var Q35;
            Q35=makeQuery(id+"F2.imprint","IMPRINT",FACE,{"disambiguationData":[TD([[makeQuery(id+"F2.imprint","IMPRINT",EDGE,{"derivedFrom":sQuery(id+"F2.wireOp",EDGE,"E1002")}),-1.0]])]});
            var Q36;
            Q36=makeQuery(id+"F2.imprint","IMPRINT",FACE,{"disambiguationData":[TD([[makeQuery(id+"F2.imprint","IMPRINT",EDGE,{"derivedFrom":sQuery(id+"F2.wireOp",EDGE,"E2204")}),-1.0]])]});
            var Q37;
            Q37=makeQuery(id+"F2.imprint","IMPRINT",FACE,{"disambiguationData":[TD([[makeQuery(id+"F2.imprint","IMPRINT",EDGE,{"derivedFrom":sQuery(id+"F2.wireOp",EDGE,"E1920")}),-1.0]])]});
            var Q38;
            Q38=makeQuery(id+"F2.imprint","IMPRINT",FACE,{"disambiguationData":[TD([[makeQuery(id+"F2.imprint","IMPRINT",EDGE,{"derivedFrom":sQuery(id+"F2.wireOp",EDGE,"E1458")}),-1.0]])]});
            var Q39;
            Q39=makeQuery(id+"F2.imprint","IMPRINT",FACE,{"disambiguationData":[TD([[makeQuery(id+"F2.imprint","IMPRINT",EDGE,{"derivedFrom":sQuery(id+"F2.wireOp",EDGE,"E496")}),-1.0]])]});
            var Q40;
            Q40=makeQuery(id+"F2.imprint","IMPRINT",FACE,{"disambiguationData":[TD([[makeQuery(id+"F2.imprint","IMPRINT",EDGE,{"derivedFrom":sQuery(id+"F2.wireOp",EDGE,"E1780")}),-1.0]])]});
            var Q41;
            Q41=makeQuery(id+"F2.imprint","IMPRINT",FACE,{"disambiguationData":[TD([[makeQuery(id+"F2.imprint","IMPRINT",EDGE,{"derivedFrom":sQuery(id+"F2.wireOp",EDGE,"E1836")}),-1.0]])]});
            var Q42;
            Q42=makeQuery(id+"F2.imprint","IMPRINT",FACE,{"disambiguationData":[TD([[makeQuery(id+"F2.imprint","IMPRINT",EDGE,{"derivedFrom":sQuery(id+"F2.wireOp",EDGE,"E679")}),-1.0]])]});
            var Q43;
            Q43=makeQuery(id+"F2.imprint","IMPRINT",FACE,{"disambiguationData":[TD([[makeQuery(id+"F2.imprint","IMPRINT",EDGE,{"derivedFrom":sQuery(id+"F2.wireOp",EDGE,"E891")}),-1.0]])]});
            var Q44;
            Q44=makeQuery(id+"F2.imprint","IMPRINT",FACE,{"disambiguationData":[TD([[makeQuery(id+"F2.imprint","IMPRINT",EDGE,{"derivedFrom":sQuery(id+"F2.wireOp",EDGE,"E1920")}),1.0]])]});
            var Q45;
            Q45=makeQuery(id+"F2.imprint","IMPRINT",FACE,{"disambiguationData":[TD([[makeQuery(id+"F2.imprint","IMPRINT",EDGE,{"derivedFrom":sQuery(id+"F2.wireOp",EDGE,"E483")}),-1.0]])]});
            var Q46;
            Q46=makeQuery(id+"F2.imprint","IMPRINT",FACE,{"disambiguationData":[TD([[makeQuery(id+"F2.imprint","IMPRINT",EDGE,{"derivedFrom":sQuery(id+"F2.wireOp",EDGE,"E1359")}),1.0]])]});
            var Q47;
            Q47=makeQuery(id+"F2.imprint","IMPRINT",FACE,{"disambiguationData":[TD([[makeQuery(id+"F2.imprint","IMPRINT",EDGE,{"derivedFrom":sQuery(id+"F2.wireOp",EDGE,"E1646")}),-1.0]])]});
            var Q48;
            Q48=makeQuery(id+"F2.imprint","IMPRINT",FACE,{"disambiguationData":[TD([[makeQuery(id+"F2.imprint","IMPRINT",EDGE,{"derivedFrom":sQuery(id+"F2.wireOp",EDGE,"E568")}),-1.0]])]});
            var Q49;
            Q49=makeQuery(id+"F2.imprint","IMPRINT",FACE,{"disambiguationData":[TD([[makeQuery(id+"F2.imprint","IMPRINT",EDGE,{"derivedFrom":sQuery(id+"F2.wireOp",EDGE,"E1865")}),1.0]])]});
            var Q50;
            Q50=makeQuery(id+"F2.imprint","IMPRINT",FACE,{"disambiguationData":[TD([[makeQuery(id+"F2.imprint","IMPRINT",EDGE,{"derivedFrom":sQuery(id+"F2.wireOp",EDGE,"E860")}),-1.0]])]});
            var Q51;
            Q51=makeQuery(id+"F2.imprint","IMPRINT",FACE,{"disambiguationData":[TD([[makeQuery(id+"F2.imprint","IMPRINT",EDGE,{"derivedFrom":sQuery(id+"F2.wireOp",EDGE,"E1780")}),1.0]])]});
            var Q52;
            Q52=makeQuery(id+"F2.imprint","IMPRINT",FACE,{"disambiguationData":[TD([[makeQuery(id+"F2.imprint","IMPRINT",EDGE,{"derivedFrom":sQuery(id+"F2.wireOp",EDGE,"E1115")}),1.0]])]});
            var Q53;
            Q53=makeQuery(id+"F2.imprint","IMPRINT",FACE,{"disambiguationData":[TD([[makeQuery(id+"F2.imprint","IMPRINT",EDGE,{"derivedFrom":sQuery(id+"F2.wireOp",EDGE,"E1731")}),-1.0]])]});
            var Q54;
            Q54=makeQuery(id+"F2.imprint","IMPRINT",FACE,{"disambiguationData":[TD([[makeQuery(id+"F2.imprint","IMPRINT",EDGE,{"derivedFrom":sQuery(id+"F2.wireOp",EDGE,"E739")}),1.0]])]});
            var Q55;
            Q55=makeQuery(id+"F2.imprint","IMPRINT",FACE,{"disambiguationData":[TD([[makeQuery(id+"F2.imprint","IMPRINT",EDGE,{"derivedFrom":sQuery(id+"F2.wireOp",EDGE,"E1085")}),-1.0]])]});
            var Q56;
            Q56=makeQuery(id+"F2.imprint","IMPRINT",FACE,{"disambiguationData":[TD([[makeQuery(id+"F2.imprint","IMPRINT",EDGE,{"derivedFrom":sQuery(id+"F2.wireOp",EDGE,"E701")}),1.0]])]});
            var Q57;
            Q57=makeQuery(id+"F2.imprint","IMPRINT",FACE,{"disambiguationData":[TD([[makeQuery(id+"F2.imprint","IMPRINT",EDGE,{"derivedFrom":sQuery(id+"F2.wireOp",EDGE,"E781")}),-1.0]])]});
            var Q58;
            Q58=makeQuery(id+"F2.imprint","IMPRINT",FACE,{"disambiguationData":[TD([[makeQuery(id+"F2.imprint","IMPRINT",EDGE,{"derivedFrom":sQuery(id+"F2.wireOp",EDGE,"E835")}),-1.0]])]});
            var Q59;
            Q59=makeQuery(id+"F2.imprint","IMPRINT",FACE,{"disambiguationData":[TD([[makeQuery(id+"F2.imprint","IMPRINT",EDGE,{"derivedFrom":sQuery(id+"F2.wireOp",EDGE,"E1125")}),1.0]])]});
            var Q60;
            Q60=makeQuery(id+"F2.imprint","IMPRINT",FACE,{"disambiguationData":[TD([[makeQuery(id+"F2.imprint","IMPRINT",EDGE,{"derivedFrom":sQuery(id+"F2.wireOp",EDGE,"E1180")}),1.0]])]});
            var Q61;
            Q61=makeQuery(id+"F2.imprint","IMPRINT",FACE,{"disambiguationData":[TD([[makeQuery(id+"F2.imprint","IMPRINT",EDGE,{"derivedFrom":sQuery(id+"F2.wireOp",EDGE,"E1675")}),1.0]])]});
            var Q62;
            Q62=makeQuery(id+"F2.imprint","IMPRINT",FACE,{"disambiguationData":[TD([[makeQuery(id+"F2.imprint","IMPRINT",EDGE,{"derivedFrom":sQuery(id+"F2.wireOp",EDGE,"E781")}),1.0]])]});
            var Q63;
            Q63=makeQuery(id+"F2.imprint","IMPRINT",FACE,{"disambiguationData":[TD([[makeQuery(id+"F2.imprint","IMPRINT",EDGE,{"derivedFrom":sQuery(id+"F2.wireOp",EDGE,"E1413")}),1.0]])]});
            var Q64;
            Q64=makeQuery(id+"F2.imprint","IMPRINT",FACE,{"disambiguationData":[TD([[makeQuery(id+"F2.imprint","IMPRINT",EDGE,{"derivedFrom":sQuery(id+"F2.wireOp",EDGE,"E1731")}),1.0]])]});
            var Q65;
            Q65=makeQuery(id+"F2.imprint","IMPRINT",FACE,{"disambiguationData":[TD([[makeQuery(id+"F2.imprint","IMPRINT",EDGE,{"derivedFrom":sQuery(id+"F2.wireOp",EDGE,"E739")}),-1.0]])]});
            var Q66;
            Q66=makeQuery(id+"F2.imprint","IMPRINT",FACE,{"disambiguationData":[TD([[makeQuery(id+"F2.imprint","IMPRINT",EDGE,{"derivedFrom":sQuery(id+"F2.wireOp",EDGE,"E1217")}),1.0]])]});
            var Q67;
            Q67=makeQuery(id+"F2.imprint","IMPRINT",FACE,{"disambiguationData":[TD([[makeQuery(id+"F2.imprint","IMPRINT",EDGE,{"derivedFrom":sQuery(id+"F2.wireOp",EDGE,"E1754")}),1.0]])]});
            var Q68;
            Q68=makeQuery(id+"F2.imprint","IMPRINT",FACE,{"disambiguationData":[TD([[makeQuery(id+"F2.imprint","IMPRINT",EDGE,{"derivedFrom":sQuery(id+"F2.wireOp",EDGE,"E1545")}),1.0]])]});
            var Q69;
            Q69=makeQuery(id+"F2.imprint","IMPRINT",FACE,{"disambiguationData":[TD([[makeQuery(id+"F2.imprint","IMPRINT",EDGE,{"derivedFrom":sQuery(id+"F2.wireOp",EDGE,"E1597")}),1.0]])]});
            var Q70;
            Q70=makeQuery(id+"F2.imprint","IMPRINT",FACE,{"disambiguationData":[TD([[makeQuery(id+"F2.imprint","IMPRINT",EDGE,{"derivedFrom":sQuery(id+"F2.wireOp",EDGE,"E1442")}),-1.0]])]});
            var Q71;
            Q71=makeQuery(id+"F2.imprint","IMPRINT",FACE,{"disambiguationData":[TD([[makeQuery(id+"F2.imprint","IMPRINT",EDGE,{"derivedFrom":sQuery(id+"F2.wireOp",EDGE,"E1545")}),-1.0]])]});
            extrude(context, id + "F3", {"entities" : qUnion([Q0, Q1, Q2, Q3, Q4, Q5, Q6, Q7, Q8, Q9, Q10, Q11, Q12, Q13, Q14, Q15, Q16, Q17, Q18, Q19, Q20, Q21, Q22, Q23, Q24, Q25, Q26, Q27, Q28, Q29, Q30, Q31, Q32, Q33, Q34, Q35, Q36, Q37, Q38, Q39, Q40, Q41, Q42, Q43, Q44, Q45, Q46, Q47, Q48, Q49, Q50, Q51, Q52, Q53, Q54, Q55, Q56, Q57, Q58, Q59, Q60, Q61, Q62, Q63, Q64, Q65, Q66, Q67, Q68, Q69, Q70, Q71]), "operationType" : NewBodyOperationType.REMOVE, "oppositeDirection" : true, "depth" : 2 * mm, "offsetDistance" : 25 * mm});
        }
    });
